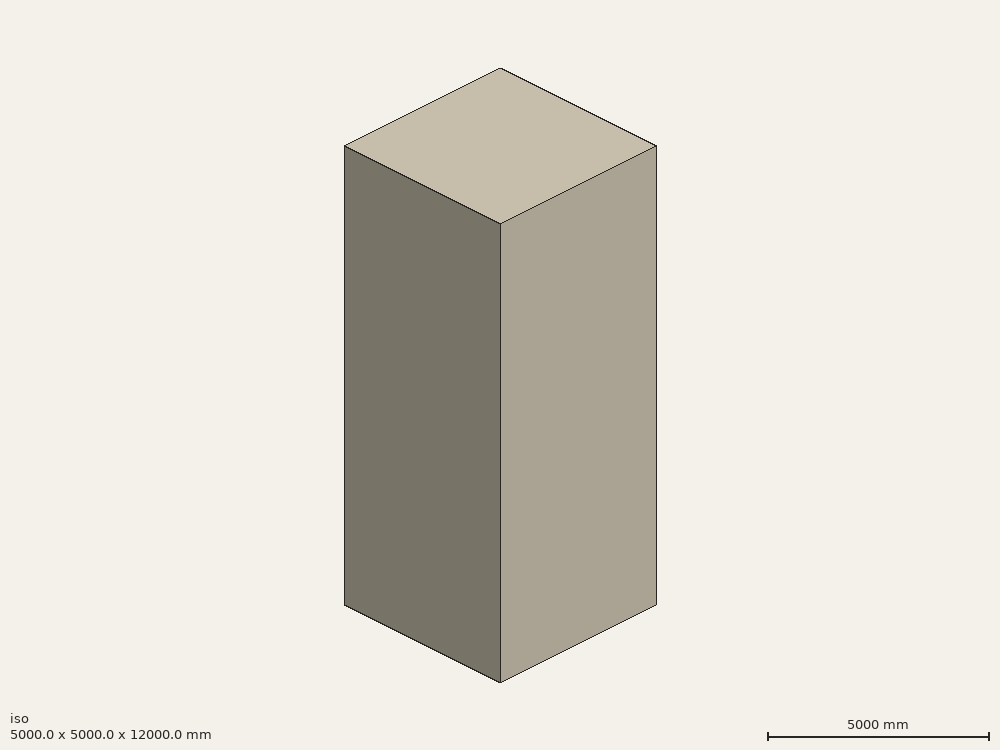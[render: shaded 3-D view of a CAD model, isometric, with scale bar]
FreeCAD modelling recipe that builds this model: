
FCSTD DOCUMENT  (FreeCAD 0.21R33694 (Git))
Label: revolveTester-7
License: All rights reserved
LicenseURL: http://en.wikipedia.org/wiki/All_rights_reserved
objects: App::DocumentObjectGroupPython×1248, Part::FeaturePython×2, App::Part×2, Sketcher::SketchObject×1, Part::Revolution×1, Part::Cylinder×1, Part::Mirroring×1, Part::Cut×1
note: 7 computed .brp shape members not serialized (recipe doc carries the construction recipe); baked Part::Feature solids carry a one-line shape summary decoded from their .brp

FEATURE [App::DocumentObjectGroupPython] HALFPI  # scripted group (container) (typed FeaturePython)
  name = HALFPI
  value = pi/2.
FEATURE [App::DocumentObjectGroupPython] PI  # scripted group (container) (typed FeaturePython)
  name = PI
  value = 1.*pi
FEATURE [App::DocumentObjectGroupPython] TWOPI  # scripted group (container) (typed FeaturePython)
  name = TWOPI
  value = 2.*pi
FEATURE [App::DocumentObjectGroupPython] Constants  # scripted group (container) (typed FeaturePython)
  Group = -> [HALFPI,PI,TWOPI]
FEATURE [App::DocumentObjectGroupPython] Variables  # scripted group (container) (typed FeaturePython)
FEATURE [App::DocumentObjectGroupPython] Quantities  # scripted group (container) (typed FeaturePython)
FEATURE [App::DocumentObjectGroupPython] Isotopes  # scripted group (container) (typed FeaturePython)
FEATURE [App::DocumentObjectGroupPython] Elements  # scripted group (container) (typed FeaturePython)
FEATURE [App::DocumentObjectGroupPython] G4Isotopes  # scripted group (container) (typed FeaturePython)
FEATURE [App::DocumentObjectGroupPython] H_element  # scripted group (container) (typed FeaturePython)
  Z = 1
  atom_value = 1.008
  formula = H
  name = H_element
FEATURE [App::DocumentObjectGroupPython] He_element  # scripted group (container) (typed FeaturePython)
  Z = 2
  atom_value = 4.0026
  formula = He
  name = He_element
FEATURE [App::DocumentObjectGroupPython] Li_element  # scripted group (container) (typed FeaturePython)
  Z = 3
  atom_value = 6.94
  formula = Li
  name = Li_element
FEATURE [App::DocumentObjectGroupPython] Be_element  # scripted group (container) (typed FeaturePython)
  Z = 4
  atom_value = 9.01218
  formula = Be
  name = Be_element
FEATURE [App::DocumentObjectGroupPython] B_element  # scripted group (container) (typed FeaturePython)
  Z = 5
  atom_value = 10.81
  formula = B
  name = B_element
FEATURE [App::DocumentObjectGroupPython] C_element  # scripted group (container) (typed FeaturePython)
  Z = 6
  atom_value = 12.011
  formula = C
  name = C_element
FEATURE [App::DocumentObjectGroupPython] N_element  # scripted group (container) (typed FeaturePython)
  Z = 7
  atom_value = 14.007
  formula = N
  name = N_element
FEATURE [App::DocumentObjectGroupPython] O_element  # scripted group (container) (typed FeaturePython)
  Z = 8
  atom_value = 15.999
  formula = O
  name = O_element
FEATURE [App::DocumentObjectGroupPython] F_element  # scripted group (container) (typed FeaturePython)
  Z = 9
  atom_value = 18.9984
  formula = F
  name = F_element
FEATURE [App::DocumentObjectGroupPython] Ne_element  # scripted group (container) (typed FeaturePython)
  Z = 10
  atom_value = 20.1797
  formula = Ne
  name = Ne_element
FEATURE [App::DocumentObjectGroupPython] Na_element  # scripted group (container) (typed FeaturePython)
  Z = 11
  atom_value = 22.9898
  formula = Na
  name = Na_element
FEATURE [App::DocumentObjectGroupPython] Mg_element  # scripted group (container) (typed FeaturePython)
  Z = 12
  atom_value = 24.305
  formula = Mg
  name = Mg_element
FEATURE [App::DocumentObjectGroupPython] Al_element  # scripted group (container) (typed FeaturePython)
  Z = 13
  atom_value = 26.9815
  formula = Al
  name = Al_element
FEATURE [App::DocumentObjectGroupPython] Si_element  # scripted group (container) (typed FeaturePython)
  Z = 14
  atom_value = 28.085
  formula = Si
  name = Si_element
FEATURE [App::DocumentObjectGroupPython] P_element  # scripted group (container) (typed FeaturePython)
  Z = 15
  atom_value = 30.9738
  formula = P
  name = P_element
FEATURE [App::DocumentObjectGroupPython] S_element  # scripted group (container) (typed FeaturePython)
  Z = 16
  atom_value = 32.06
  formula = S
  name = S_element
FEATURE [App::DocumentObjectGroupPython] Cl_element  # scripted group (container) (typed FeaturePython)
  Z = 17
  atom_value = 35.45
  formula = Cl
  name = Cl_element
FEATURE [App::DocumentObjectGroupPython] Ar_element  # scripted group (container) (typed FeaturePython)
  Z = 18
  atom_value = 39.95
  formula = Ar
  name = Ar_element
FEATURE [App::DocumentObjectGroupPython] K_element  # scripted group (container) (typed FeaturePython)
  Z = 19
  atom_value = 39.0983
  formula = K
  name = K_element
FEATURE [App::DocumentObjectGroupPython] Ca_element  # scripted group (container) (typed FeaturePython)
  Z = 20
  atom_value = 40.078
  formula = Ca
  name = Ca_element
FEATURE [App::DocumentObjectGroupPython] Sc_element  # scripted group (container) (typed FeaturePython)
  Z = 21
  atom_value = 44.9559
  formula = Sc
  name = Sc_element
FEATURE [App::DocumentObjectGroupPython] Ti_element  # scripted group (container) (typed FeaturePython)
  Z = 22
  atom_value = 47.867
  formula = Ti
  name = Ti_element
FEATURE [App::DocumentObjectGroupPython] V_element  # scripted group (container) (typed FeaturePython)
  Z = 23
  atom_value = 50.9415
  formula = V
  name = V_element
FEATURE [App::DocumentObjectGroupPython] Cr_element  # scripted group (container) (typed FeaturePython)
  Z = 24
  atom_value = 51.9961
  formula = Cr
  name = Cr_element
FEATURE [App::DocumentObjectGroupPython] Mn_element  # scripted group (container) (typed FeaturePython)
  Z = 25
  atom_value = 54.938
  formula = Mn
  name = Mn_element
FEATURE [App::DocumentObjectGroupPython] Fe_element  # scripted group (container) (typed FeaturePython)
  Z = 26
  atom_value = 55.845
  formula = Fe
  name = Fe_element
FEATURE [App::DocumentObjectGroupPython] Co_element  # scripted group (container) (typed FeaturePython)
  Z = 27
  atom_value = 58.9332
  formula = Co
  name = Co_element
FEATURE [App::DocumentObjectGroupPython] Ni_element  # scripted group (container) (typed FeaturePython)
  Z = 28
  atom_value = 58.6934
  formula = Ni
  name = Ni_element
FEATURE [App::DocumentObjectGroupPython] Cu_element  # scripted group (container) (typed FeaturePython)
  Z = 29
  atom_value = 63.546
  formula = Cu
  name = Cu_element
FEATURE [App::DocumentObjectGroupPython] Zn_element  # scripted group (container) (typed FeaturePython)
  Z = 30
  atom_value = 65.38
  formula = Zn
  name = Zn_element
FEATURE [App::DocumentObjectGroupPython] Ga_element  # scripted group (container) (typed FeaturePython)
  Z = 31
  atom_value = 69.723
  formula = Ga
  name = Ga_element
FEATURE [App::DocumentObjectGroupPython] Ge_element  # scripted group (container) (typed FeaturePython)
  Z = 32
  atom_value = 72.63
  formula = Ge
  name = Ge_element
FEATURE [App::DocumentObjectGroupPython] As_element  # scripted group (container) (typed FeaturePython)
  Z = 33
  atom_value = 74.9216
  formula = As
  name = As_element
FEATURE [App::DocumentObjectGroupPython] Se_element  # scripted group (container) (typed FeaturePython)
  Z = 34
  atom_value = 78.971
  formula = Se
  name = Se_element
FEATURE [App::DocumentObjectGroupPython] Br_element  # scripted group (container) (typed FeaturePython)
  Z = 35
  atom_value = 79.904
  formula = Br
  name = Br_element
FEATURE [App::DocumentObjectGroupPython] Kr_element  # scripted group (container) (typed FeaturePython)
  Z = 36
  atom_value = 83.798
  formula = Kr
  name = Kr_element
FEATURE [App::DocumentObjectGroupPython] Rb_element  # scripted group (container) (typed FeaturePython)
  Z = 37
  atom_value = 85.4678
  formula = Rb
  name = Rb_element
FEATURE [App::DocumentObjectGroupPython] Sr_element  # scripted group (container) (typed FeaturePython)
  Z = 38
  atom_value = 87.62
  formula = Sr
  name = Sr_element
FEATURE [App::DocumentObjectGroupPython] Y_element  # scripted group (container) (typed FeaturePython)
  Z = 39
  atom_value = 88.9058
  formula = Y
  name = Y_element
FEATURE [App::DocumentObjectGroupPython] Zr_element  # scripted group (container) (typed FeaturePython)
  Z = 40
  atom_value = 91.224
  formula = Zr
  name = Zr_element
FEATURE [App::DocumentObjectGroupPython] Nb_element  # scripted group (container) (typed FeaturePython)
  Z = 41
  atom_value = 92.9064
  formula = Nb
  name = Nb_element
FEATURE [App::DocumentObjectGroupPython] Mo_element  # scripted group (container) (typed FeaturePython)
  Z = 42
  atom_value = 95.95
  formula = Mo
  name = Mo_element
FEATURE [App::DocumentObjectGroupPython] Tc_element  # scripted group (container) (typed FeaturePython)
  Z = 43
  atom_value = 97
  formula = Tc
  name = Tc_element
FEATURE [App::DocumentObjectGroupPython] Ru_element  # scripted group (container) (typed FeaturePython)
  Z = 44
  atom_value = 101.07
  formula = Ru
  name = Ru_element
FEATURE [App::DocumentObjectGroupPython] Rh_element  # scripted group (container) (typed FeaturePython)
  Z = 45
  atom_value = 102.905
  formula = Rh
  name = Rh_element
FEATURE [App::DocumentObjectGroupPython] Pd_element  # scripted group (container) (typed FeaturePython)
  Z = 46
  atom_value = 106.42
  formula = Pd
  name = Pd_element
FEATURE [App::DocumentObjectGroupPython] Ag_element  # scripted group (container) (typed FeaturePython)
  Z = 47
  atom_value = 107.868
  formula = Ag
  name = Ag_element
FEATURE [App::DocumentObjectGroupPython] Cd_element  # scripted group (container) (typed FeaturePython)
  Z = 48
  atom_value = 112.414
  formula = Cd
  name = Cd_element
FEATURE [App::DocumentObjectGroupPython] In_element  # scripted group (container) (typed FeaturePython)
  Z = 49
  atom_value = 114.818
  formula = In
  name = In_element
FEATURE [App::DocumentObjectGroupPython] Sn_element  # scripted group (container) (typed FeaturePython)
  Z = 50
  atom_value = 118.71
  formula = Sn
  name = Sn_element
FEATURE [App::DocumentObjectGroupPython] Sb_element  # scripted group (container) (typed FeaturePython)
  Z = 51
  atom_value = 121.76
  formula = Sb
  name = Sb_element
FEATURE [App::DocumentObjectGroupPython] Te_element  # scripted group (container) (typed FeaturePython)
  Z = 52
  atom_value = 127.6
  formula = Te
  name = Te_element
FEATURE [App::DocumentObjectGroupPython] I_element  # scripted group (container) (typed FeaturePython)
  Z = 53
  atom_value = 126.904
  formula = I
  name = I_element
FEATURE [App::DocumentObjectGroupPython] Xe_element  # scripted group (container) (typed FeaturePython)
  Z = 54
  atom_value = 131.293
  formula = Xe
  name = Xe_element
FEATURE [App::DocumentObjectGroupPython] Cs_element  # scripted group (container) (typed FeaturePython)
  Z = 55
  atom_value = 132.905
  formula = Cs
  name = Cs_element
FEATURE [App::DocumentObjectGroupPython] Ba_element  # scripted group (container) (typed FeaturePython)
  Z = 56
  atom_value = 137.327
  formula = Ba
  name = Ba_element
FEATURE [App::DocumentObjectGroupPython] La_element  # scripted group (container) (typed FeaturePython)
  Z = 57
  atom_value = 138.905
  formula = La
  name = La_element
FEATURE [App::DocumentObjectGroupPython] Ce_element  # scripted group (container) (typed FeaturePython)
  Z = 58
  atom_value = 140.116
  formula = Ce
  name = Ce_element
FEATURE [App::DocumentObjectGroupPython] Pr_element  # scripted group (container) (typed FeaturePython)
  Z = 59
  atom_value = 140.908
  formula = Pr
  name = Pr_element
FEATURE [App::DocumentObjectGroupPython] Nd_element  # scripted group (container) (typed FeaturePython)
  Z = 60
  atom_value = 144.242
  formula = Nd
  name = Nd_element
FEATURE [App::DocumentObjectGroupPython] Pm_element  # scripted group (container) (typed FeaturePython)
  Z = 61
  atom_value = 145
  formula = Pm
  name = Pm_element
FEATURE [App::DocumentObjectGroupPython] Sm_element  # scripted group (container) (typed FeaturePython)
  Z = 62
  atom_value = 150.36
  formula = Sm
  name = Sm_element
FEATURE [App::DocumentObjectGroupPython] Eu_element  # scripted group (container) (typed FeaturePython)
  Z = 63
  atom_value = 151.964
  formula = Eu
  name = Eu_element
FEATURE [App::DocumentObjectGroupPython] Gd_element  # scripted group (container) (typed FeaturePython)
  Z = 64
  atom_value = 157.25
  formula = Gd
  name = Gd_element
FEATURE [App::DocumentObjectGroupPython] Tb_element  # scripted group (container) (typed FeaturePython)
  Z = 65
  atom_value = 158.925
  formula = Tb
  name = Tb_element
FEATURE [App::DocumentObjectGroupPython] Dy_element  # scripted group (container) (typed FeaturePython)
  Z = 66
  atom_value = 162.5
  formula = Dy
  name = Dy_element
FEATURE [App::DocumentObjectGroupPython] Ho_element  # scripted group (container) (typed FeaturePython)
  Z = 67
  atom_value = 164.93
  formula = Ho
  name = Ho_element
FEATURE [App::DocumentObjectGroupPython] Er_element  # scripted group (container) (typed FeaturePython)
  Z = 68
  atom_value = 167.259
  formula = Er
  name = Er_element
FEATURE [App::DocumentObjectGroupPython] Tm_element  # scripted group (container) (typed FeaturePython)
  Z = 69
  atom_value = 168.934
  formula = Tm
  name = Tm_element
FEATURE [App::DocumentObjectGroupPython] Yb_element  # scripted group (container) (typed FeaturePython)
  Z = 70
  atom_value = 173.045
  formula = Yb
  name = Yb_element
FEATURE [App::DocumentObjectGroupPython] Lu_element  # scripted group (container) (typed FeaturePython)
  Z = 71
  atom_value = 174.967
  formula = Lu
  name = Lu_element
FEATURE [App::DocumentObjectGroupPython] Hf_element  # scripted group (container) (typed FeaturePython)
  Z = 72
  atom_value = 178.49
  formula = Hf
  name = Hf_element
FEATURE [App::DocumentObjectGroupPython] Ta_element  # scripted group (container) (typed FeaturePython)
  Z = 73
  atom_value = 180.948
  formula = Ta
  name = Ta_element
FEATURE [App::DocumentObjectGroupPython] W_element  # scripted group (container) (typed FeaturePython)
  Z = 74
  atom_value = 183.84
  formula = W
  name = W_element
FEATURE [App::DocumentObjectGroupPython] Re_element  # scripted group (container) (typed FeaturePython)
  Z = 75
  atom_value = 186.207
  formula = Re
  name = Re_element
FEATURE [App::DocumentObjectGroupPython] Os_element  # scripted group (container) (typed FeaturePython)
  Z = 76
  atom_value = 190.23
  formula = Os
  name = Os_element
FEATURE [App::DocumentObjectGroupPython] Ir_element  # scripted group (container) (typed FeaturePython)
  Z = 77
  atom_value = 192.217
  formula = Ir
  name = Ir_element
FEATURE [App::DocumentObjectGroupPython] Pt_element  # scripted group (container) (typed FeaturePython)
  Z = 78
  atom_value = 195.084
  formula = Pt
  name = Pt_element
FEATURE [App::DocumentObjectGroupPython] Au_element  # scripted group (container) (typed FeaturePython)
  Z = 79
  atom_value = 196.967
  formula = Au
  name = Au_element
FEATURE [App::DocumentObjectGroupPython] Hg_element  # scripted group (container) (typed FeaturePython)
  Z = 80
  atom_value = 200.592
  formula = Hg
  name = Hg_element
FEATURE [App::DocumentObjectGroupPython] Tl_element  # scripted group (container) (typed FeaturePython)
  Z = 81
  atom_value = 204.38
  formula = Tl
  name = Tl_element
FEATURE [App::DocumentObjectGroupPython] Pb_element  # scripted group (container) (typed FeaturePython)
  Z = 82
  atom_value = 207.2
  formula = Pb
  name = Pb_element
FEATURE [App::DocumentObjectGroupPython] Bi_element  # scripted group (container) (typed FeaturePython)
  Z = 83
  atom_value = 208.98
  formula = Bi
  name = Bi_element
FEATURE [App::DocumentObjectGroupPython] Po_element  # scripted group (container) (typed FeaturePython)
  Z = 84
  atom_value = 209
  formula = Po
  name = Po_element
FEATURE [App::DocumentObjectGroupPython] At_element  # scripted group (container) (typed FeaturePython)
  Z = 85
  atom_value = 210
  formula = At
  name = At_element
FEATURE [App::DocumentObjectGroupPython] Rn_element  # scripted group (container) (typed FeaturePython)
  Z = 86
  atom_value = 222
  formula = Rn
  name = Rn_element
FEATURE [App::DocumentObjectGroupPython] Fr_element  # scripted group (container) (typed FeaturePython)
  Z = 87
  atom_value = 223
  formula = Fr
  name = Fr_element
FEATURE [App::DocumentObjectGroupPython] Ra_element  # scripted group (container) (typed FeaturePython)
  Z = 88
  atom_value = 226
  formula = Ra
  name = Ra_element
FEATURE [App::DocumentObjectGroupPython] Ac_element  # scripted group (container) (typed FeaturePython)
  Z = 89
  atom_value = 227
  formula = Ac
  name = Ac_element
FEATURE [App::DocumentObjectGroupPython] Th_element  # scripted group (container) (typed FeaturePython)
  Z = 90
  atom_value = 232.038
  formula = Th
  name = Th_element
FEATURE [App::DocumentObjectGroupPython] Pa_element  # scripted group (container) (typed FeaturePython)
  Z = 91
  atom_value = 231.036
  formula = Pa
  name = Pa_element
FEATURE [App::DocumentObjectGroupPython] U_element  # scripted group (container) (typed FeaturePython)
  Z = 92
  atom_value = 238.029
  formula = U
  name = U_element
FEATURE [App::DocumentObjectGroupPython] Np_element  # scripted group (container) (typed FeaturePython)
  Z = 93
  atom_value = 237
  formula = Np
  name = Np_element
FEATURE [App::DocumentObjectGroupPython] Pu_element  # scripted group (container) (typed FeaturePython)
  Z = 94
  atom_value = 244
  formula = Pu
  name = Pu_element
FEATURE [App::DocumentObjectGroupPython] Am_element  # scripted group (container) (typed FeaturePython)
  Z = 95
  atom_value = 243
  formula = Am
  name = Am_element
FEATURE [App::DocumentObjectGroupPython] Cm_element  # scripted group (container) (typed FeaturePython)
  Z = 96
  atom_value = 247
  formula = Cm
  name = Cm_element
FEATURE [App::DocumentObjectGroupPython] Bk_element  # scripted group (container) (typed FeaturePython)
  Z = 97
  atom_value = 247
  formula = Bk
  name = Bk_element
FEATURE [App::DocumentObjectGroupPython] Cf_element  # scripted group (container) (typed FeaturePython)
  Z = 98
  atom_value = 251
  formula = Cf
  name = Cf_element
FEATURE [App::DocumentObjectGroupPython] G4Elements  # scripted group (container) (typed FeaturePython)
  Group = -> [H_element,He_element,Li_element,Be_element,B_element,C_element,N_element,O_element,F_element,Ne_element,Na_element,Mg_element,Al_element,Si_element,P_element,S_element,Cl_element,Ar_element,K_element,Ca_element,Sc_element,Ti_element,V_element,Cr_element,Mn_element,Fe_element,Co_element,Ni_element,Cu_element,Zn_element,Ga_element,Ge_element,As_element,Se_element,Br_element,Kr_element,Rb_element,+61 more]
FEATURE [App::DocumentObjectGroupPython] H_element001  label="H_element : 0.101"  # scripted group (container) (typed FeaturePython)
  n = 0.101327
FEATURE [App::DocumentObjectGroupPython] C_element001  label="C_element : 0.775"  # scripted group (container) (typed FeaturePython)
  n = 0.7755
FEATURE [App::DocumentObjectGroupPython] N_element001  label="N_element : 0.035"  # scripted group (container) (typed FeaturePython)
  n = 0.035057
FEATURE [App::DocumentObjectGroupPython] O_element001  label="O_element : 0.052"  # scripted group (container) (typed FeaturePython)
  n = 0.0523159
FEATURE [App::DocumentObjectGroupPython] F_element001  label="F_element : 0.017"  # scripted group (container) (typed FeaturePython)
  n = 0.017422
FEATURE [App::DocumentObjectGroupPython] Ca_element001  label="Ca_element : 0.018"  # scripted group (container) (typed FeaturePython)
  n = 0.018378
FEATURE [App::DocumentObjectGroupPython] G4_A_150_TISSUE  label="G4_A-150_TISSUE"  # scripted group (container) (typed FeaturePython)
  Dunit = g/cm3
  Dvalue = 1.127
  Group = -> [H_element001,C_element001,N_element001,O_element001,F_element001,Ca_element001]
  conduct = 2
  density = 1
  expand = 3
  formula = G4_A-150_TISSUE
  name = G4_A-150_TISSUE
  specific = 4
FEATURE [App::DocumentObjectGroupPython] C_element002  label="C_element : 3"  # scripted group (container) (typed FeaturePython)
  n = 3
  ref = C_element
FEATURE [App::DocumentObjectGroupPython] H_element002  label="H_element : 6"  # scripted group (container) (typed FeaturePython)
  n = 6
  ref = H_element
FEATURE [App::DocumentObjectGroupPython] O_element002  label="O_element : 1"  # scripted group (container) (typed FeaturePython)
  n = 1
  ref = O_element
FEATURE [App::DocumentObjectGroupPython] G4_ACETONE  # scripted group (container) (typed FeaturePython)
  Dunit = g/cm3
  Dvalue = 0.7899
  Group = -> [C_element002,H_element002,O_element002]
  conduct = 2
  density = 1
  expand = 3
  formula = G4_ACETONE
  name = G4_ACETONE
  specific = 4
FEATURE [App::DocumentObjectGroupPython] C_element003  label="C_element : 2"  # scripted group (container) (typed FeaturePython)
  n = 2
  ref = C_element
FEATURE [App::DocumentObjectGroupPython] H_element003  label="H_element : 2"  # scripted group (container) (typed FeaturePython)
  n = 2
  ref = H_element
FEATURE [App::DocumentObjectGroupPython] G4_ACETYLENE  # scripted group (container) (typed FeaturePython)
  Dunit = g/cm3
  Dvalue = 0.0010967
  Group = -> [C_element003,H_element003]
  conduct = 2
  density = 1
  expand = 3
  formula = G4_ACETYLENE
  name = G4_ACETYLENE
  specific = 4
FEATURE [App::DocumentObjectGroupPython] C_element004  label="C_element : 5"  # scripted group (container) (typed FeaturePython)
  n = 5
  ref = C_element
FEATURE [App::DocumentObjectGroupPython] H_element004  label="H_element : 5"  # scripted group (container) (typed FeaturePython)
  n = 5
  ref = H_element
FEATURE [App::DocumentObjectGroupPython] N_element002  label="N_element : 5"  # scripted group (container) (typed FeaturePython)
  n = 5
  ref = N_element
FEATURE [App::DocumentObjectGroupPython] G4_ADENINE  # scripted group (container) (typed FeaturePython)
  Dunit = g/cm3
  Dvalue = 1.6
  Group = -> [C_element004,H_element004,N_element002]
  conduct = 2
  density = 1
  expand = 3
  formula = G4_ADENINE
  name = G4_ADENINE
  specific = 4
FEATURE [App::DocumentObjectGroupPython] H_element005  label="H_element : 0.114"  # scripted group (container) (typed FeaturePython)
  n = 0.114
FEATURE [App::DocumentObjectGroupPython] C_element005  label="C_element : 0.598"  # scripted group (container) (typed FeaturePython)
  n = 0.598
FEATURE [App::DocumentObjectGroupPython] N_element003  label="N_element : 0.007"  # scripted group (container) (typed FeaturePython)
  n = 0.007
FEATURE [App::DocumentObjectGroupPython] O_element003  label="O_element : 0.278"  # scripted group (container) (typed FeaturePython)
  n = 0.278
FEATURE [App::DocumentObjectGroupPython] Na_element001  label="Na_element : 0.001"  # scripted group (container) (typed FeaturePython)
  n = 0.001
FEATURE [App::DocumentObjectGroupPython] S_element001  label="S_element : 0.001"  # scripted group (container) (typed FeaturePython)
  n = 0.001
FEATURE [App::DocumentObjectGroupPython] Cl_element001  label="Cl_element : 0.001"  # scripted group (container) (typed FeaturePython)
  n = 0.001
FEATURE [App::DocumentObjectGroupPython] G4_ADIPOSE_TISSUE_ICRP  # scripted group (container) (typed FeaturePython)
  Dunit = g/cm3
  Dvalue = 0.95
  Group = -> [H_element005,C_element005,N_element003,O_element003,Na_element001,S_element001,Cl_element001]
  conduct = 2
  density = 1
  expand = 3
  formula = G4_ADIPOSE_TISSUE_ICRP
  name = G4_ADIPOSE_TISSUE_ICRP
  specific = 4
FEATURE [App::DocumentObjectGroupPython] C_element006  label="C_element : 0.000"  # scripted group (container) (typed FeaturePython)
  n = 0.000124
FEATURE [App::DocumentObjectGroupPython] N_element004  label="N_element : 0.755"  # scripted group (container) (typed FeaturePython)
  n = 0.755268
FEATURE [App::DocumentObjectGroupPython] O_element004  label="O_element : 0.232"  # scripted group (container) (typed FeaturePython)
  n = 0.231781
FEATURE [App::DocumentObjectGroupPython] Ar_element001  label="Ar_element : 0.013"  # scripted group (container) (typed FeaturePython)
  n = 0.012827
FEATURE [App::DocumentObjectGroupPython] G4_AIR  # scripted group (container) (typed FeaturePython)
  Dunit = g/cm3
  Dvalue = 0.00120479
  Group = -> [C_element006,N_element004,O_element004,Ar_element001]
  conduct = 2
  density = 1
  expand = 3
  formula = G4_AIR
  name = G4_AIR
  specific = 4
FEATURE [App::DocumentObjectGroupPython] C_element007  label="C_element : 006"  # scripted group (container) (typed FeaturePython)
  n = 3
  ref = C_element
FEATURE [App::DocumentObjectGroupPython] H_element006  label="H_element : 7"  # scripted group (container) (typed FeaturePython)
  n = 7
  ref = H_element
FEATURE [App::DocumentObjectGroupPython] N_element005  label="N_element : 1"  # scripted group (container) (typed FeaturePython)
  n = 1
  ref = N_element
FEATURE [App::DocumentObjectGroupPython] O_element005  label="O_element : 2"  # scripted group (container) (typed FeaturePython)
  n = 2
  ref = O_element
FEATURE [App::DocumentObjectGroupPython] G4_ALANINE  # scripted group (container) (typed FeaturePython)
  Dunit = g/cm3
  Dvalue = 1.42
  Group = -> [C_element007,H_element006,N_element005,O_element005]
  conduct = 2
  density = 1
  expand = 3
  formula = G4_ALANINE
  name = G4_ALANINE
  specific = 4
FEATURE [App::DocumentObjectGroupPython] Al_element001  label="Al_element : 2"  # scripted group (container) (typed FeaturePython)
  n = 2
  ref = Al_element
FEATURE [App::DocumentObjectGroupPython] O_element006  label="O_element : 3"  # scripted group (container) (typed FeaturePython)
  n = 3
  ref = O_element
FEATURE [App::DocumentObjectGroupPython] G4_ALUMINUM_OXIDE  # scripted group (container) (typed FeaturePython)
  Dunit = g/cm3
  Dvalue = 3.97
  Group = -> [Al_element001,O_element006]
  conduct = 2
  density = 1
  expand = 3
  formula = G4_ALUMINUM_OXIDE
  name = G4_ALUMINUM_OXIDE
  specific = 4
FEATURE [App::DocumentObjectGroupPython] H_element007  label="H_element : 0.106"  # scripted group (container) (typed FeaturePython)
  n = 0.10593
FEATURE [App::DocumentObjectGroupPython] C_element008  label="C_element : 0.789"  # scripted group (container) (typed FeaturePython)
  n = 0.788974
FEATURE [App::DocumentObjectGroupPython] O_element007  label="O_element : 0.105"  # scripted group (container) (typed FeaturePython)
  n = 0.105096
FEATURE [App::DocumentObjectGroupPython] G4_AMBER  # scripted group (container) (typed FeaturePython)
  Dunit = g/cm3
  Dvalue = 1.1
  Group = -> [H_element007,C_element008,O_element007]
  conduct = 2
  density = 1
  expand = 3
  formula = G4_AMBER
  name = G4_AMBER
  specific = 4
FEATURE [App::DocumentObjectGroupPython] N_element006  label="N_element : 006"  # scripted group (container) (typed FeaturePython)
  n = 1
  ref = N_element
FEATURE [App::DocumentObjectGroupPython] H_element008  label="H_element : 3"  # scripted group (container) (typed FeaturePython)
  n = 3
  ref = H_element
FEATURE [App::DocumentObjectGroupPython] G4_AMMONIA  # scripted group (container) (typed FeaturePython)
  Dunit = g/cm3
  Dvalue = 0.000826019
  Group = -> [N_element006,H_element008]
  conduct = 2
  density = 1
  expand = 3
  formula = G4_AMMONIA
  name = G4_AMMONIA
  specific = 4
FEATURE [App::DocumentObjectGroupPython] C_element009  label="C_element : 6"  # scripted group (container) (typed FeaturePython)
  n = 6
  ref = C_element
FEATURE [App::DocumentObjectGroupPython] H_element009  label="H_element : 008"  # scripted group (container) (typed FeaturePython)
  n = 7
  ref = H_element
FEATURE [App::DocumentObjectGroupPython] N_element007  label="N_element : 007"  # scripted group (container) (typed FeaturePython)
  n = 1
  ref = N_element
FEATURE [App::DocumentObjectGroupPython] G4_ANILINE  # scripted group (container) (typed FeaturePython)
  Dunit = g/cm3
  Dvalue = 1.0235
  Group = -> [C_element009,H_element009,N_element007]
  conduct = 2
  density = 1
  expand = 3
  formula = G4_ANILINE
  name = G4_ANILINE
  specific = 4
FEATURE [App::DocumentObjectGroupPython] C_element010  label="C_element : 14"  # scripted group (container) (typed FeaturePython)
  n = 14
  ref = C_element
FEATURE [App::DocumentObjectGroupPython] H_element010  label="H_element : 10"  # scripted group (container) (typed FeaturePython)
  n = 10
  ref = H_element
FEATURE [App::DocumentObjectGroupPython] G4_ANTHRACENE  # scripted group (container) (typed FeaturePython)
  Dunit = g/cm3
  Dvalue = 1.283
  Group = -> [C_element010,H_element010]
  conduct = 2
  density = 1
  expand = 3
  formula = G4_ANTHRACENE
  name = G4_ANTHRACENE
  specific = 4
FEATURE [App::DocumentObjectGroupPython] H_element011  label="H_element : 0.065"  # scripted group (container) (typed FeaturePython)
  n = 0.0654709
FEATURE [App::DocumentObjectGroupPython] C_element011  label="C_element : 0.537"  # scripted group (container) (typed FeaturePython)
  n = 0.536944
FEATURE [App::DocumentObjectGroupPython] N_element008  label="N_element : 0.021"  # scripted group (container) (typed FeaturePython)
  n = 0.0215
FEATURE [App::DocumentObjectGroupPython] O_element008  label="O_element : 0.032"  # scripted group (container) (typed FeaturePython)
  n = 0.032085
FEATURE [App::DocumentObjectGroupPython] F_element002  label="F_element : 0.167"  # scripted group (container) (typed FeaturePython)
  n = 0.167411
FEATURE [App::DocumentObjectGroupPython] Ca_element002  label="Ca_element : 0.177"  # scripted group (container) (typed FeaturePython)
  n = 0.176589
FEATURE [App::DocumentObjectGroupPython] G4_B_100_BONE  label="G4_B-100_BONE"  # scripted group (container) (typed FeaturePython)
  Dunit = g/cm3
  Dvalue = 1.45
  Group = -> [H_element011,C_element011,N_element008,O_element008,F_element002,Ca_element002]
  conduct = 2
  density = 1
  expand = 3
  formula = G4_B-100_BONE
  name = G4_B-100_BONE
  specific = 4
FEATURE [App::DocumentObjectGroupPython] H_element012  label="H_element : 0.057"  # scripted group (container) (typed FeaturePython)
  n = 0.057441
FEATURE [App::DocumentObjectGroupPython] C_element012  label="C_element : 0.790"  # scripted group (container) (typed FeaturePython)
  n = 0.774591
FEATURE [App::DocumentObjectGroupPython] O_element009  label="O_element : 0.168"  # scripted group (container) (typed FeaturePython)
  n = 0.167968
FEATURE [App::DocumentObjectGroupPython] G4_BAKELITE  # scripted group (container) (typed FeaturePython)
  Dunit = g/cm3
  Dvalue = 1.25
  Group = -> [H_element012,C_element012,O_element009]
  conduct = 2
  density = 1
  expand = 3
  formula = G4_BAKELITE
  name = G4_BAKELITE
  specific = 4
FEATURE [App::DocumentObjectGroupPython] Ba_element001  label="Ba_element : 1"  # scripted group (container) (typed FeaturePython)
  n = 1
  ref = Ba_element
FEATURE [App::DocumentObjectGroupPython] F_element003  label="F_element : 2"  # scripted group (container) (typed FeaturePython)
  n = 2
  ref = F_element
FEATURE [App::DocumentObjectGroupPython] G4_BARIUM_FLUORIDE  # scripted group (container) (typed FeaturePython)
  Dunit = g/cm3
  Dvalue = 4.89
  Group = -> [Ba_element001,F_element003]
  conduct = 2
  density = 1
  expand = 3
  formula = G4_BARIUM_FLUORIDE
  name = G4_BARIUM_FLUORIDE
  specific = 4
FEATURE [App::DocumentObjectGroupPython] Ba_element002  label="Ba_element : 002"  # scripted group (container) (typed FeaturePython)
  n = 1
  ref = Ba_element
FEATURE [App::DocumentObjectGroupPython] S_element002  label="S_element : 1"  # scripted group (container) (typed FeaturePython)
  n = 1
  ref = S_element
FEATURE [App::DocumentObjectGroupPython] O_element010  label="O_element : 4"  # scripted group (container) (typed FeaturePython)
  n = 4
  ref = O_element
FEATURE [App::DocumentObjectGroupPython] G4_BARIUM_SULFATE  # scripted group (container) (typed FeaturePython)
  Dunit = g/cm3
  Dvalue = 4.5
  Group = -> [Ba_element002,S_element002,O_element010]
  conduct = 2
  density = 1
  expand = 3
  formula = G4_BARIUM_SULFATE
  name = G4_BARIUM_SULFATE
  specific = 4
FEATURE [App::DocumentObjectGroupPython] C_element013  label="C_element : 007"  # scripted group (container) (typed FeaturePython)
  n = 6
  ref = C_element
FEATURE [App::DocumentObjectGroupPython] H_element013  label="H_element : 009"  # scripted group (container) (typed FeaturePython)
  n = 6
  ref = H_element
FEATURE [App::DocumentObjectGroupPython] G4_BENZENE  # scripted group (container) (typed FeaturePython)
  Dunit = g/cm3
  Dvalue = 0.87865
  Group = -> [C_element013,H_element013]
  conduct = 2
  density = 1
  expand = 3
  formula = G4_BENZENE
  name = G4_BENZENE
  specific = 4
FEATURE [App::DocumentObjectGroupPython] Be_element001  label="Be_element : 1"  # scripted group (container) (typed FeaturePython)
  n = 1
  ref = Be_element
FEATURE [App::DocumentObjectGroupPython] O_element011  label="O_element : 005"  # scripted group (container) (typed FeaturePython)
  n = 1
  ref = O_element
FEATURE [App::DocumentObjectGroupPython] G4_BERYLLIUM_OXIDE  # scripted group (container) (typed FeaturePython)
  Dunit = g/cm3
  Dvalue = 3.01
  Group = -> [Be_element001,O_element011]
  conduct = 2
  density = 1
  expand = 3
  formula = G4_BERYLLIUM_OXIDE
  name = G4_BERYLLIUM_OXIDE
  specific = 4
FEATURE [App::DocumentObjectGroupPython] Bi_element001  label="Bi_element : 4"  # scripted group (container) (typed FeaturePython)
  n = 4
  ref = Bi_element
FEATURE [App::DocumentObjectGroupPython] Ge_element001  label="Ge_element : 3"  # scripted group (container) (typed FeaturePython)
  n = 3
  ref = Ge_element
FEATURE [App::DocumentObjectGroupPython] O_element012  label="O_element : 12"  # scripted group (container) (typed FeaturePython)
  n = 12
  ref = O_element
FEATURE [App::DocumentObjectGroupPython] G4_BGO  # scripted group (container) (typed FeaturePython)
  Dunit = g/cm3
  Dvalue = 7.13
  Group = -> [Bi_element001,Ge_element001,O_element012]
  conduct = 2
  density = 1
  expand = 3
  formula = G4_BGO
  name = G4_BGO
  specific = 4
FEATURE [App::DocumentObjectGroupPython] H_element014  label="H_element : 0.102"  # scripted group (container) (typed FeaturePython)
  n = 0.102
FEATURE [App::DocumentObjectGroupPython] C_element014  label="C_element : 0.110"  # scripted group (container) (typed FeaturePython)
  n = 0.11
FEATURE [App::DocumentObjectGroupPython] N_element009  label="N_element : 0.033"  # scripted group (container) (typed FeaturePython)
  n = 0.033
FEATURE [App::DocumentObjectGroupPython] O_element013  label="O_element : 0.745"  # scripted group (container) (typed FeaturePython)
  n = 0.745
FEATURE [App::DocumentObjectGroupPython] Na_element002  label="Na_element : 0.002"  # scripted group (container) (typed FeaturePython)
  n = 0.001
FEATURE [App::DocumentObjectGroupPython] P_element001  label="P_element : 0.001"  # scripted group (container) (typed FeaturePython)
  n = 0.001
FEATURE [App::DocumentObjectGroupPython] S_element003  label="S_element : 0.002"  # scripted group (container) (typed FeaturePython)
  n = 0.002
FEATURE [App::DocumentObjectGroupPython] Cl_element002  label="Cl_element : 0.003"  # scripted group (container) (typed FeaturePython)
  n = 0.003
FEATURE [App::DocumentObjectGroupPython] K_element001  label="K_element : 0.002"  # scripted group (container) (typed FeaturePython)
  n = 0.002
FEATURE [App::DocumentObjectGroupPython] Fe_element001  label="Fe_element : 0.001"  # scripted group (container) (typed FeaturePython)
  n = 0.001
FEATURE [App::DocumentObjectGroupPython] G4_BLOOD_ICRP  # scripted group (container) (typed FeaturePython)
  Dunit = g/cm3
  Dvalue = 1.06
  Group = -> [H_element014,C_element014,N_element009,O_element013,Na_element002,P_element001,S_element003,Cl_element002,K_element001,Fe_element001]
  conduct = 2
  density = 1
  expand = 3
  formula = G4_BLOOD_ICRP
  name = G4_BLOOD_ICRP
  specific = 4
FEATURE [App::DocumentObjectGroupPython] H_element015  label="H_element : 0.064"  # scripted group (container) (typed FeaturePython)
  n = 0.064
FEATURE [App::DocumentObjectGroupPython] C_element015  label="C_element : 0.278"  # scripted group (container) (typed FeaturePython)
  n = 0.278
FEATURE [App::DocumentObjectGroupPython] N_element010  label="N_element : 0.027"  # scripted group (container) (typed FeaturePython)
  n = 0.027
FEATURE [App::DocumentObjectGroupPython] O_element014  label="O_element : 0.410"  # scripted group (container) (typed FeaturePython)
  n = 0.41
FEATURE [App::DocumentObjectGroupPython] Mg_element001  label="Mg_element : 0.002"  # scripted group (container) (typed FeaturePython)
  n = 0.002
FEATURE [App::DocumentObjectGroupPython] P_element002  label="P_element : 0.070"  # scripted group (container) (typed FeaturePython)
  n = 0.07
FEATURE [App::DocumentObjectGroupPython] S_element004  label="S_element : 0.003"  # scripted group (container) (typed FeaturePython)
  n = 0.002
FEATURE [App::DocumentObjectGroupPython] Ca_element003  label="Ca_element : 0.147"  # scripted group (container) (typed FeaturePython)
  n = 0.147
FEATURE [App::DocumentObjectGroupPython] G4_BONE_COMPACT_ICRU  # scripted group (container) (typed FeaturePython)
  Dunit = g/cm3
  Dvalue = 1.85
  Group = -> [H_element015,C_element015,N_element010,O_element014,Mg_element001,P_element002,S_element004,Ca_element003]
  conduct = 2
  density = 1
  expand = 3
  formula = G4_BONE_COMPACT_ICRU
  name = G4_BONE_COMPACT_ICRU
  specific = 4
FEATURE [App::DocumentObjectGroupPython] H_element016  label="H_element : 0.034"  # scripted group (container) (typed FeaturePython)
  n = 0.034
FEATURE [App::DocumentObjectGroupPython] C_element016  label="C_element : 0.155"  # scripted group (container) (typed FeaturePython)
  n = 0.155
FEATURE [App::DocumentObjectGroupPython] N_element011  label="N_element : 0.042"  # scripted group (container) (typed FeaturePython)
  n = 0.042
FEATURE [App::DocumentObjectGroupPython] O_element015  label="O_element : 0.435"  # scripted group (container) (typed FeaturePython)
  n = 0.435
FEATURE [App::DocumentObjectGroupPython] Na_element003  label="Na_element : 0.003"  # scripted group (container) (typed FeaturePython)
  n = 0.001
FEATURE [App::DocumentObjectGroupPython] Mg_element002  label="Mg_element : 0.003"  # scripted group (container) (typed FeaturePython)
  n = 0.002
FEATURE [App::DocumentObjectGroupPython] P_element003  label="P_element : 0.103"  # scripted group (container) (typed FeaturePython)
  n = 0.103
FEATURE [App::DocumentObjectGroupPython] S_element005  label="S_element : 0.004"  # scripted group (container) (typed FeaturePython)
  n = 0.003
FEATURE [App::DocumentObjectGroupPython] Ca_element004  label="Ca_element : 0.225"  # scripted group (container) (typed FeaturePython)
  n = 0.225
FEATURE [App::DocumentObjectGroupPython] G4_BONE_CORTICAL_ICRP  # scripted group (container) (typed FeaturePython)
  Dunit = g/cm3
  Dvalue = 1.92
  Group = -> [H_element016,C_element016,N_element011,O_element015,Na_element003,Mg_element002,P_element003,S_element005,Ca_element004]
  conduct = 2
  density = 1
  expand = 3
  formula = G4_BONE_CORTICAL_ICRP
  name = G4_BONE_CORTICAL_ICRP
  specific = 4
FEATURE [App::DocumentObjectGroupPython] B_element001  label="B_element : 4"  # scripted group (container) (typed FeaturePython)
  n = 4
  ref = B_element
FEATURE [App::DocumentObjectGroupPython] C_element017  label="C_element : 1"  # scripted group (container) (typed FeaturePython)
  n = 1
  ref = C_element
FEATURE [App::DocumentObjectGroupPython] G4_BORON_CARBIDE  # scripted group (container) (typed FeaturePython)
  Dunit = g/cm3
  Dvalue = 2.52
  Group = -> [B_element001,C_element017]
  conduct = 2
  density = 1
  expand = 3
  formula = G4_BORON_CARBIDE
  name = G4_BORON_CARBIDE
  specific = 4
FEATURE [App::DocumentObjectGroupPython] B_element002  label="B_element : 2"  # scripted group (container) (typed FeaturePython)
  n = 2
  ref = B_element
FEATURE [App::DocumentObjectGroupPython] O_element016  label="O_element : 006"  # scripted group (container) (typed FeaturePython)
  n = 3
  ref = O_element
FEATURE [App::DocumentObjectGroupPython] G4_BORON_OXIDE  # scripted group (container) (typed FeaturePython)
  Dunit = g/cm3
  Dvalue = 1.812
  Group = -> [B_element002,O_element016]
  conduct = 2
  density = 1
  expand = 3
  formula = G4_BORON_OXIDE
  name = G4_BORON_OXIDE
  specific = 4
FEATURE [App::DocumentObjectGroupPython] H_element017  label="H_element : 0.107"  # scripted group (container) (typed FeaturePython)
  n = 0.107
FEATURE [App::DocumentObjectGroupPython] C_element018  label="C_element : 0.145"  # scripted group (container) (typed FeaturePython)
  n = 0.145
FEATURE [App::DocumentObjectGroupPython] N_element012  label="N_element : 0.022"  # scripted group (container) (typed FeaturePython)
  n = 0.022
FEATURE [App::DocumentObjectGroupPython] O_element017  label="O_element : 0.712"  # scripted group (container) (typed FeaturePython)
  n = 0.712
FEATURE [App::DocumentObjectGroupPython] Na_element004  label="Na_element : 0.004"  # scripted group (container) (typed FeaturePython)
  n = 0.002
FEATURE [App::DocumentObjectGroupPython] P_element004  label="P_element : 0.004"  # scripted group (container) (typed FeaturePython)
  n = 0.004
FEATURE [App::DocumentObjectGroupPython] S_element006  label="S_element : 0.005"  # scripted group (container) (typed FeaturePython)
  n = 0.002
FEATURE [App::DocumentObjectGroupPython] Cl_element003  label="Cl_element : 0.004"  # scripted group (container) (typed FeaturePython)
  n = 0.003
FEATURE [App::DocumentObjectGroupPython] K_element002  label="K_element : 0.003"  # scripted group (container) (typed FeaturePython)
  n = 0.003
FEATURE [App::DocumentObjectGroupPython] G4_BRAIN_ICRP  # scripted group (container) (typed FeaturePython)
  Dunit = g/cm3
  Dvalue = 1.04
  Group = -> [H_element017,C_element018,N_element012,O_element017,Na_element004,P_element004,S_element006,Cl_element003,K_element002]
  conduct = 2
  density = 1
  expand = 3
  formula = G4_BRAIN_ICRP
  name = G4_BRAIN_ICRP
  specific = 4
FEATURE [App::DocumentObjectGroupPython] C_element019  label="C_element : 4"  # scripted group (container) (typed FeaturePython)
  n = 4
  ref = C_element
FEATURE [App::DocumentObjectGroupPython] H_element018  label="H_element : 010"  # scripted group (container) (typed FeaturePython)
  n = 10
  ref = H_element
FEATURE [App::DocumentObjectGroupPython] G4_BUTANE  # scripted group (container) (typed FeaturePython)
  Dunit = g/cm3
  Dvalue = 0.00249343
  Group = -> [C_element019,H_element018]
  conduct = 2
  density = 1
  expand = 3
  formula = G4_BUTANE
  name = G4_BUTANE
  specific = 4
FEATURE [App::DocumentObjectGroupPython] C_element020  label="C_element : 008"  # scripted group (container) (typed FeaturePython)
  n = 4
  ref = C_element
FEATURE [App::DocumentObjectGroupPython] H_element019  label="H_element : 011"  # scripted group (container) (typed FeaturePython)
  n = 10
  ref = H_element
FEATURE [App::DocumentObjectGroupPython] O_element018  label="O_element : 007"  # scripted group (container) (typed FeaturePython)
  n = 1
  ref = O_element
FEATURE [App::DocumentObjectGroupPython] G4_N_BUTYL_ALCOHOL  label="G4_N-BUTYL_ALCOHOL"  # scripted group (container) (typed FeaturePython)
  Dunit = g/cm3
  Dvalue = 0.8098
  Group = -> [C_element020,H_element019,O_element018]
  conduct = 2
  density = 1
  expand = 3
  formula = G4_N-BUTYL_ALCOHOL
  name = G4_N-BUTYL_ALCOHOL
  specific = 4
FEATURE [App::DocumentObjectGroupPython] H_element020  label="H_element : 0.025"  # scripted group (container) (typed FeaturePython)
  n = 0.02468
FEATURE [App::DocumentObjectGroupPython] C_element021  label="C_element : 0.502"  # scripted group (container) (typed FeaturePython)
  n = 0.501611
FEATURE [App::DocumentObjectGroupPython] O_element019  label="O_element : 0.005"  # scripted group (container) (typed FeaturePython)
  n = 0.004527
FEATURE [App::DocumentObjectGroupPython] F_element004  label="F_element : 0.465"  # scripted group (container) (typed FeaturePython)
  n = 0.465209
FEATURE [App::DocumentObjectGroupPython] Si_element001  label="Si_element : 0.004"  # scripted group (container) (typed FeaturePython)
  n = 0.003973
FEATURE [App::DocumentObjectGroupPython] G4_C_552  label="G4_C-552"  # scripted group (container) (typed FeaturePython)
  Dunit = g/cm3
  Dvalue = 1.76
  Group = -> [H_element020,C_element021,O_element019,F_element004,Si_element001]
  conduct = 2
  density = 1
  expand = 3
  formula = G4_C-552
  name = G4_C-552
  specific = 4
FEATURE [App::DocumentObjectGroupPython] Cd_element001  label="Cd_element : 1"  # scripted group (container) (typed FeaturePython)
  n = 1
  ref = Cd_element
FEATURE [App::DocumentObjectGroupPython] Te_element001  label="Te_element : 1"  # scripted group (container) (typed FeaturePython)
  n = 1
  ref = Te_element
FEATURE [App::DocumentObjectGroupPython] G4_CADMIUM_TELLURIDE  # scripted group (container) (typed FeaturePython)
  Dunit = g/cm3
  Dvalue = 6.2
  Group = -> [Cd_element001,Te_element001]
  conduct = 2
  density = 1
  expand = 3
  formula = G4_CADMIUM_TELLURIDE
  name = G4_CADMIUM_TELLURIDE
  specific = 4
FEATURE [App::DocumentObjectGroupPython] Cd_element002  label="Cd_element : 002"  # scripted group (container) (typed FeaturePython)
  n = 1
  ref = Cd_element
FEATURE [App::DocumentObjectGroupPython] W_element001  label="W_element : 1"  # scripted group (container) (typed FeaturePython)
  n = 1
  ref = W_element
FEATURE [App::DocumentObjectGroupPython] O_element020  label="O_element : 008"  # scripted group (container) (typed FeaturePython)
  n = 4
  ref = O_element
FEATURE [App::DocumentObjectGroupPython] G4_CADMIUM_TUNGSTATE  # scripted group (container) (typed FeaturePython)
  Dunit = g/cm3
  Dvalue = 7.9
  Group = -> [Cd_element002,W_element001,O_element020]
  conduct = 2
  density = 1
  expand = 3
  formula = G4_CADMIUM_TUNGSTATE
  name = G4_CADMIUM_TUNGSTATE
  specific = 4
FEATURE [App::DocumentObjectGroupPython] Ca_element005  label="Ca_element : 1"  # scripted group (container) (typed FeaturePython)
  n = 1
  ref = Ca_element
FEATURE [App::DocumentObjectGroupPython] C_element022  label="C_element : 009"  # scripted group (container) (typed FeaturePython)
  n = 1
  ref = C_element
FEATURE [App::DocumentObjectGroupPython] O_element021  label="O_element : 009"  # scripted group (container) (typed FeaturePython)
  n = 3
  ref = O_element
FEATURE [App::DocumentObjectGroupPython] G4_CALCIUM_CARBONATE  # scripted group (container) (typed FeaturePython)
  Dunit = g/cm3
  Dvalue = 2.8
  Group = -> [Ca_element005,C_element022,O_element021]
  conduct = 2
  density = 1
  expand = 3
  formula = G4_CALCIUM_CARBONATE
  name = G4_CALCIUM_CARBONATE
  specific = 4
FEATURE [App::DocumentObjectGroupPython] Ca_element006  label="Ca_element : 002"  # scripted group (container) (typed FeaturePython)
  n = 1
  ref = Ca_element
FEATURE [App::DocumentObjectGroupPython] F_element005  label="F_element : 003"  # scripted group (container) (typed FeaturePython)
  n = 2
  ref = F_element
FEATURE [App::DocumentObjectGroupPython] G4_CALCIUM_FLUORIDE  # scripted group (container) (typed FeaturePython)
  Dunit = g/cm3
  Dvalue = 3.18
  Group = -> [Ca_element006,F_element005]
  conduct = 2
  density = 1
  expand = 3
  formula = G4_CALCIUM_FLUORIDE
  name = G4_CALCIUM_FLUORIDE
  specific = 4
FEATURE [App::DocumentObjectGroupPython] Ca_element007  label="Ca_element : 003"  # scripted group (container) (typed FeaturePython)
  n = 1
  ref = Ca_element
FEATURE [App::DocumentObjectGroupPython] O_element022  label="O_element : 010"  # scripted group (container) (typed FeaturePython)
  n = 1
  ref = O_element
FEATURE [App::DocumentObjectGroupPython] G4_CALCIUM_OXIDE  # scripted group (container) (typed FeaturePython)
  Dunit = g/cm3
  Dvalue = 3.3
  Group = -> [Ca_element007,O_element022]
  conduct = 2
  density = 1
  expand = 3
  formula = G4_CALCIUM_OXIDE
  name = G4_CALCIUM_OXIDE
  specific = 4
FEATURE [App::DocumentObjectGroupPython] Ca_element008  label="Ca_element : 004"  # scripted group (container) (typed FeaturePython)
  n = 1
  ref = Ca_element
FEATURE [App::DocumentObjectGroupPython] S_element007  label="S_element : 002"  # scripted group (container) (typed FeaturePython)
  n = 1
  ref = S_element
FEATURE [App::DocumentObjectGroupPython] O_element023  label="O_element : 011"  # scripted group (container) (typed FeaturePython)
  n = 4
  ref = O_element
FEATURE [App::DocumentObjectGroupPython] G4_CALCIUM_SULFATE  # scripted group (container) (typed FeaturePython)
  Dunit = g/cm3
  Dvalue = 2.96
  Group = -> [Ca_element008,S_element007,O_element023]
  conduct = 2
  density = 1
  expand = 3
  formula = G4_CALCIUM_SULFATE
  name = G4_CALCIUM_SULFATE
  specific = 4
FEATURE [App::DocumentObjectGroupPython] Ca_element009  label="Ca_element : 005"  # scripted group (container) (typed FeaturePython)
  n = 1
  ref = Ca_element
FEATURE [App::DocumentObjectGroupPython] W_element002  label="W_element : 002"  # scripted group (container) (typed FeaturePython)
  n = 1
  ref = W_element
FEATURE [App::DocumentObjectGroupPython] O_element024  label="O_element : 012"  # scripted group (container) (typed FeaturePython)
  n = 4
  ref = O_element
FEATURE [App::DocumentObjectGroupPython] G4_CALCIUM_TUNGSTATE  # scripted group (container) (typed FeaturePython)
  Dunit = g/cm3
  Dvalue = 6.062
  Group = -> [Ca_element009,W_element002,O_element024]
  conduct = 2
  density = 1
  expand = 3
  formula = G4_CALCIUM_TUNGSTATE
  name = G4_CALCIUM_TUNGSTATE
  specific = 4
FEATURE [App::DocumentObjectGroupPython] C_element023  label="C_element : 010"  # scripted group (container) (typed FeaturePython)
  n = 1
  ref = C_element
FEATURE [App::DocumentObjectGroupPython] O_element025  label="O_element : 013"  # scripted group (container) (typed FeaturePython)
  n = 2
  ref = O_element
FEATURE [App::DocumentObjectGroupPython] G4_CARBON_DIOXIDE  # scripted group (container) (typed FeaturePython)
  Dunit = g/cm3
  Dvalue = 0.00184212
  Group = -> [C_element023,O_element025]
  conduct = 2
  density = 1
  expand = 3
  formula = G4_CARBON_DIOXIDE
  name = G4_CARBON_DIOXIDE
  specific = 4
FEATURE [App::DocumentObjectGroupPython] C_element024  label="C_element : 011"  # scripted group (container) (typed FeaturePython)
  n = 1
  ref = C_element
FEATURE [App::DocumentObjectGroupPython] Cl_element004  label="Cl_element : 4"  # scripted group (container) (typed FeaturePython)
  n = 4
  ref = Cl_element
FEATURE [App::DocumentObjectGroupPython] G4_CARBON_TETRACHLORIDE  # scripted group (container) (typed FeaturePython)
  Dunit = g/cm3
  Dvalue = 1.594
  Group = -> [C_element024,Cl_element004]
  conduct = 2
  density = 1
  expand = 3
  formula = G4_CARBON_TETRACHLORIDE
  name = G4_CARBON_TETRACHLORIDE
  specific = 4
FEATURE [App::DocumentObjectGroupPython] C_element025  label="C_element : 012"  # scripted group (container) (typed FeaturePython)
  n = 6
  ref = C_element
FEATURE [App::DocumentObjectGroupPython] H_element021  label="H_element : 012"  # scripted group (container) (typed FeaturePython)
  n = 10
  ref = H_element
FEATURE [App::DocumentObjectGroupPython] O_element026  label="O_element : 5"  # scripted group (container) (typed FeaturePython)
  n = 5
  ref = O_element
FEATURE [App::DocumentObjectGroupPython] G4_CELLULOSE_CELLOPHANE  # scripted group (container) (typed FeaturePython)
  Dunit = g/cm3
  Dvalue = 1.42
  Group = -> [C_element025,H_element021,O_element026]
  conduct = 2
  density = 1
  expand = 3
  formula = G4_CELLULOSE_CELLOPHANE
  name = G4_CELLULOSE_CELLOPHANE
  specific = 4
FEATURE [App::DocumentObjectGroupPython] H_element022  label="H_element : 0.067"  # scripted group (container) (typed FeaturePython)
  n = 0.067125
FEATURE [App::DocumentObjectGroupPython] C_element026  label="C_element : 0.545"  # scripted group (container) (typed FeaturePython)
  n = 0.545403
FEATURE [App::DocumentObjectGroupPython] O_element027  label="O_element : 0.387"  # scripted group (container) (typed FeaturePython)
  n = 0.387472
FEATURE [App::DocumentObjectGroupPython] G4_CELLULOSE_BUTYRATE  # scripted group (container) (typed FeaturePython)
  Dunit = g/cm3
  Dvalue = 1.2
  Group = -> [H_element022,C_element026,O_element027]
  conduct = 2
  density = 1
  expand = 3
  formula = G4_CELLULOSE_BUTYRATE
  name = G4_CELLULOSE_BUTYRATE
  specific = 4
FEATURE [App::DocumentObjectGroupPython] H_element023  label="H_element : 0.029"  # scripted group (container) (typed FeaturePython)
  n = 0.029216
FEATURE [App::DocumentObjectGroupPython] C_element027  label="C_element : 0.271"  # scripted group (container) (typed FeaturePython)
  n = 0.271296
FEATURE [App::DocumentObjectGroupPython] N_element013  label="N_element : 0.121"  # scripted group (container) (typed FeaturePython)
  n = 0.121276
FEATURE [App::DocumentObjectGroupPython] O_element028  label="O_element : 0.578"  # scripted group (container) (typed FeaturePython)
  n = 0.578212
FEATURE [App::DocumentObjectGroupPython] G4_CELLULOSE_NITRATE  # scripted group (container) (typed FeaturePython)
  Dunit = g/cm3
  Dvalue = 1.49
  Group = -> [H_element023,C_element027,N_element013,O_element028]
  conduct = 2
  density = 1
  expand = 3
  formula = G4_CELLULOSE_NITRATE
  name = G4_CELLULOSE_NITRATE
  specific = 4
FEATURE [App::DocumentObjectGroupPython] H_element024  label="H_element : 0.108"  # scripted group (container) (typed FeaturePython)
  n = 0.107596
FEATURE [App::DocumentObjectGroupPython] N_element014  label="N_element : 0.001"  # scripted group (container) (typed FeaturePython)
  n = 0.0008
FEATURE [App::DocumentObjectGroupPython] O_element029  label="O_element : 0.875"  # scripted group (container) (typed FeaturePython)
  n = 0.874976
FEATURE [App::DocumentObjectGroupPython] S_element008  label="S_element : 0.015"  # scripted group (container) (typed FeaturePython)
  n = 0.014627
FEATURE [App::DocumentObjectGroupPython] Ce_element001  label="Ce_element : 0.002"  # scripted group (container) (typed FeaturePython)
  n = 0.002001
FEATURE [App::DocumentObjectGroupPython] G4_CERIC_SULFATE  # scripted group (container) (typed FeaturePython)
  Dunit = g/cm3
  Dvalue = 1.03
  Group = -> [H_element024,N_element014,O_element029,S_element008,Ce_element001]
  conduct = 2
  density = 1
  expand = 3
  formula = G4_CERIC_SULFATE
  name = G4_CERIC_SULFATE
  specific = 4
FEATURE [App::DocumentObjectGroupPython] Cs_element001  label="Cs_element : 1"  # scripted group (container) (typed FeaturePython)
  n = 1
  ref = Cs_element
FEATURE [App::DocumentObjectGroupPython] F_element006  label="F_element : 1"  # scripted group (container) (typed FeaturePython)
  n = 1
  ref = F_element
FEATURE [App::DocumentObjectGroupPython] G4_CESIUM_FLUORIDE  # scripted group (container) (typed FeaturePython)
  Dunit = g/cm3
  Dvalue = 4.115
  Group = -> [Cs_element001,F_element006]
  conduct = 2
  density = 1
  expand = 3
  formula = G4_CESIUM_FLUORIDE
  name = G4_CESIUM_FLUORIDE
  specific = 4
FEATURE [App::DocumentObjectGroupPython] Cs_element002  label="Cs_element : 002"  # scripted group (container) (typed FeaturePython)
  n = 1
  ref = Cs_element
FEATURE [App::DocumentObjectGroupPython] I_element001  label="I_element : 1"  # scripted group (container) (typed FeaturePython)
  n = 1
  ref = I_element
FEATURE [App::DocumentObjectGroupPython] G4_CESIUM_IODIDE  # scripted group (container) (typed FeaturePython)
  Dunit = g/cm3
  Dvalue = 4.51
  Group = -> [Cs_element002,I_element001]
  conduct = 2
  density = 1
  expand = 3
  formula = G4_CESIUM_IODIDE
  name = G4_CESIUM_IODIDE
  specific = 4
FEATURE [App::DocumentObjectGroupPython] C_element028  label="C_element : 013"  # scripted group (container) (typed FeaturePython)
  n = 6
  ref = C_element
FEATURE [App::DocumentObjectGroupPython] H_element025  label="H_element : 013"  # scripted group (container) (typed FeaturePython)
  n = 5
  ref = H_element
FEATURE [App::DocumentObjectGroupPython] Cl_element005  label="Cl_element : 1"  # scripted group (container) (typed FeaturePython)
  n = 1
  ref = Cl_element
FEATURE [App::DocumentObjectGroupPython] G4_CHLOROBENZENE  # scripted group (container) (typed FeaturePython)
  Dunit = g/cm3
  Dvalue = 1.1058
  Group = -> [C_element028,H_element025,Cl_element005]
  conduct = 2
  density = 1
  expand = 3
  formula = G4_CHLOROBENZENE
  name = G4_CHLOROBENZENE
  specific = 4
FEATURE [App::DocumentObjectGroupPython] C_element029  label="C_element : 014"  # scripted group (container) (typed FeaturePython)
  n = 1
  ref = C_element
FEATURE [App::DocumentObjectGroupPython] H_element026  label="H_element : 1"  # scripted group (container) (typed FeaturePython)
  n = 1
  ref = H_element
FEATURE [App::DocumentObjectGroupPython] Cl_element006  label="Cl_element : 3"  # scripted group (container) (typed FeaturePython)
  n = 3
  ref = Cl_element
FEATURE [App::DocumentObjectGroupPython] G4_CHLOROFORM  # scripted group (container) (typed FeaturePython)
  Dunit = g/cm3
  Dvalue = 1.4832
  Group = -> [C_element029,H_element026,Cl_element006]
  conduct = 2
  density = 1
  expand = 3
  formula = G4_CHLOROFORM
  name = G4_CHLOROFORM
  specific = 4
FEATURE [App::DocumentObjectGroupPython] H_element027  label="H_element : 0.010"  # scripted group (container) (typed FeaturePython)
  n = 0.01
FEATURE [App::DocumentObjectGroupPython] C_element030  label="C_element : 0.001"  # scripted group (container) (typed FeaturePython)
  n = 0.001
FEATURE [App::DocumentObjectGroupPython] O_element030  label="O_element : 0.529"  # scripted group (container) (typed FeaturePython)
  n = 0.529107
FEATURE [App::DocumentObjectGroupPython] Na_element005  label="Na_element : 0.016"  # scripted group (container) (typed FeaturePython)
  n = 0.016
FEATURE [App::DocumentObjectGroupPython] Mg_element003  label="Mg_element : 0.004"  # scripted group (container) (typed FeaturePython)
  n = 0.002
FEATURE [App::DocumentObjectGroupPython] Al_element002  label="Al_element : 0.034"  # scripted group (container) (typed FeaturePython)
  n = 0.033872
FEATURE [App::DocumentObjectGroupPython] Si_element002  label="Si_element : 0.337"  # scripted group (container) (typed FeaturePython)
  n = 0.337021
FEATURE [App::DocumentObjectGroupPython] K_element003  label="K_element : 0.013"  # scripted group (container) (typed FeaturePython)
  n = 0.013
FEATURE [App::DocumentObjectGroupPython] Ca_element010  label="Ca_element : 0.044"  # scripted group (container) (typed FeaturePython)
  n = 0.044
FEATURE [App::DocumentObjectGroupPython] Fe_element002  label="Fe_element : 0.014"  # scripted group (container) (typed FeaturePython)
  n = 0.014
FEATURE [App::DocumentObjectGroupPython] G4_CONCRETE  # scripted group (container) (typed FeaturePython)
  Dunit = g/cm3
  Dvalue = 2.3
  Group = -> [H_element027,C_element030,O_element030,Na_element005,Mg_element003,Al_element002,Si_element002,K_element003,Ca_element010,Fe_element002]
  conduct = 2
  density = 1
  expand = 3
  formula = G4_CONCRETE
  name = G4_CONCRETE
  specific = 4
FEATURE [App::DocumentObjectGroupPython] C_element031  label="C_element : 015"  # scripted group (container) (typed FeaturePython)
  n = 6
  ref = C_element
FEATURE [App::DocumentObjectGroupPython] H_element028  label="H_element : 12"  # scripted group (container) (typed FeaturePython)
  n = 12
  ref = H_element
FEATURE [App::DocumentObjectGroupPython] G4_CYCLOHEXANE  # scripted group (container) (typed FeaturePython)
  Dunit = g/cm3
  Dvalue = 0.779
  Group = -> [C_element031,H_element028]
  conduct = 2
  density = 1
  expand = 3
  formula = G4_CYCLOHEXANE
  name = G4_CYCLOHEXANE
  specific = 4
FEATURE [App::DocumentObjectGroupPython] C_element032  label="C_element : 016"  # scripted group (container) (typed FeaturePython)
  n = 6
  ref = C_element
FEATURE [App::DocumentObjectGroupPython] H_element029  label="H_element : 4"  # scripted group (container) (typed FeaturePython)
  n = 4
  ref = H_element
FEATURE [App::DocumentObjectGroupPython] Cl_element007  label="Cl_element : 2"  # scripted group (container) (typed FeaturePython)
  n = 2
  ref = Cl_element
FEATURE [App::DocumentObjectGroupPython] G4_1_2_DICHLOROBENZENE  label="G4_1.2-DICHLOROBENZENE"  # scripted group (container) (typed FeaturePython)
  Dunit = g/cm3
  Dvalue = 1.3048
  Group = -> [C_element032,H_element029,Cl_element007]
  conduct = 2
  density = 1
  expand = 3
  formula = G4_1.2-DICHLOROBENZENE
  name = G4_1.2-DICHLOROBENZENE
  specific = 4
FEATURE [App::DocumentObjectGroupPython] C_element033  label="C_element : 017"  # scripted group (container) (typed FeaturePython)
  n = 4
  ref = C_element
FEATURE [App::DocumentObjectGroupPython] H_element030  label="H_element : 8"  # scripted group (container) (typed FeaturePython)
  n = 8
  ref = H_element
FEATURE [App::DocumentObjectGroupPython] O_element031  label="O_element : 014"  # scripted group (container) (typed FeaturePython)
  n = 1
  ref = O_element
FEATURE [App::DocumentObjectGroupPython] Cl_element008  label="Cl_element : 005"  # scripted group (container) (typed FeaturePython)
  n = 2
  ref = Cl_element
FEATURE [App::DocumentObjectGroupPython] G4_DICHLORODIETHYL_ETHER  # scripted group (container) (typed FeaturePython)
  Dunit = g/cm3
  Dvalue = 1.2199
  Group = -> [C_element033,H_element030,O_element031,Cl_element008]
  conduct = 2
  density = 1
  expand = 3
  formula = G4_DICHLORODIETHYL_ETHER
  name = G4_DICHLORODIETHYL_ETHER
  specific = 4
FEATURE [App::DocumentObjectGroupPython] C_element034  label="C_element : 018"  # scripted group (container) (typed FeaturePython)
  n = 2
  ref = C_element
FEATURE [App::DocumentObjectGroupPython] H_element031  label="H_element : 014"  # scripted group (container) (typed FeaturePython)
  n = 4
  ref = H_element
FEATURE [App::DocumentObjectGroupPython] Cl_element009  label="Cl_element : 006"  # scripted group (container) (typed FeaturePython)
  n = 2
  ref = Cl_element
FEATURE [App::DocumentObjectGroupPython] G4_1_2_DICHLOROETHANE  label="G4_1.2-DICHLOROETHANE"  # scripted group (container) (typed FeaturePython)
  Dunit = g/cm3
  Dvalue = 1.2351
  Group = -> [C_element034,H_element031,Cl_element009]
  conduct = 2
  density = 1
  expand = 3
  formula = G4_1.2-DICHLOROETHANE
  name = G4_1.2-DICHLOROETHANE
  specific = 4
FEATURE [App::DocumentObjectGroupPython] C_element035  label="C_element : 019"  # scripted group (container) (typed FeaturePython)
  n = 4
  ref = C_element
FEATURE [App::DocumentObjectGroupPython] H_element032  label="H_element : 015"  # scripted group (container) (typed FeaturePython)
  n = 10
  ref = H_element
FEATURE [App::DocumentObjectGroupPython] O_element032  label="O_element : 015"  # scripted group (container) (typed FeaturePython)
  n = 1
  ref = O_element
FEATURE [App::DocumentObjectGroupPython] G4_DIETHYL_ETHER  # scripted group (container) (typed FeaturePython)
  Dunit = g/cm3
  Dvalue = 0.71378
  Group = -> [C_element035,H_element032,O_element032]
  conduct = 2
  density = 1
  expand = 3
  formula = G4_DIETHYL_ETHER
  name = G4_DIETHYL_ETHER
  specific = 4
FEATURE [App::DocumentObjectGroupPython] C_element036  label="C_element : 020"  # scripted group (container) (typed FeaturePython)
  n = 3
  ref = C_element
FEATURE [App::DocumentObjectGroupPython] H_element033  label="H_element : 016"  # scripted group (container) (typed FeaturePython)
  n = 7
  ref = H_element
FEATURE [App::DocumentObjectGroupPython] N_element015  label="N_element : 008"  # scripted group (container) (typed FeaturePython)
  n = 1
  ref = N_element
FEATURE [App::DocumentObjectGroupPython] O_element033  label="O_element : 016"  # scripted group (container) (typed FeaturePython)
  n = 1
  ref = O_element
FEATURE [App::DocumentObjectGroupPython] G4_N_N_DIMETHYL_FORMAMIDE  label="G4_N.N-DIMETHYL_FORMAMIDE"  # scripted group (container) (typed FeaturePython)
  Dunit = g/cm3
  Dvalue = 0.9487
  Group = -> [C_element036,H_element033,N_element015,O_element033]
  conduct = 2
  density = 1
  expand = 3
  formula = G4_N.N-DIMETHYL_FORMAMIDE
  name = G4_N.N-DIMETHYL_FORMAMIDE
  specific = 4
FEATURE [App::DocumentObjectGroupPython] C_element037  label="C_element : 021"  # scripted group (container) (typed FeaturePython)
  n = 2
  ref = C_element
FEATURE [App::DocumentObjectGroupPython] H_element034  label="H_element : 017"  # scripted group (container) (typed FeaturePython)
  n = 6
  ref = H_element
FEATURE [App::DocumentObjectGroupPython] O_element034  label="O_element : 017"  # scripted group (container) (typed FeaturePython)
  n = 1
  ref = O_element
FEATURE [App::DocumentObjectGroupPython] S_element009  label="S_element : 003"  # scripted group (container) (typed FeaturePython)
  n = 1
  ref = S_element
FEATURE [App::DocumentObjectGroupPython] G4_DIMETHYL_SULFOXIDE  # scripted group (container) (typed FeaturePython)
  Dunit = g/cm3
  Dvalue = 1.1014
  Group = -> [C_element037,H_element034,O_element034,S_element009]
  conduct = 2
  density = 1
  expand = 3
  formula = G4_DIMETHYL_SULFOXIDE
  name = G4_DIMETHYL_SULFOXIDE
  specific = 4
FEATURE [App::DocumentObjectGroupPython] C_element038  label="C_element : 022"  # scripted group (container) (typed FeaturePython)
  n = 2
  ref = C_element
FEATURE [App::DocumentObjectGroupPython] H_element035  label="H_element : 018"  # scripted group (container) (typed FeaturePython)
  n = 6
  ref = H_element
FEATURE [App::DocumentObjectGroupPython] G4_ETHANE  # scripted group (container) (typed FeaturePython)
  Dunit = g/cm3
  Dvalue = 0.00125324
  Group = -> [C_element038,H_element035]
  conduct = 2
  density = 1
  expand = 3
  formula = G4_ETHANE
  name = G4_ETHANE
  specific = 4
FEATURE [App::DocumentObjectGroupPython] C_element039  label="C_element : 023"  # scripted group (container) (typed FeaturePython)
  n = 2
  ref = C_element
FEATURE [App::DocumentObjectGroupPython] H_element036  label="H_element : 019"  # scripted group (container) (typed FeaturePython)
  n = 6
  ref = H_element
FEATURE [App::DocumentObjectGroupPython] O_element035  label="O_element : 018"  # scripted group (container) (typed FeaturePython)
  n = 1
  ref = O_element
FEATURE [App::DocumentObjectGroupPython] G4_ETHYL_ALCOHOL  # scripted group (container) (typed FeaturePython)
  Dunit = g/cm3
  Dvalue = 0.7893
  Group = -> [C_element039,H_element036,O_element035]
  conduct = 2
  density = 1
  expand = 3
  formula = G4_ETHYL_ALCOHOL
  name = G4_ETHYL_ALCOHOL
  specific = 4
FEATURE [App::DocumentObjectGroupPython] H_element037  label="H_element : 0.090"  # scripted group (container) (typed FeaturePython)
  n = 0.090027
FEATURE [App::DocumentObjectGroupPython] C_element040  label="C_element : 0.585"  # scripted group (container) (typed FeaturePython)
  n = 0.585182
FEATURE [App::DocumentObjectGroupPython] O_element036  label="O_element : 0.325"  # scripted group (container) (typed FeaturePython)
  n = 0.324791
FEATURE [App::DocumentObjectGroupPython] G4_ETHYL_CELLULOSE  # scripted group (container) (typed FeaturePython)
  Dunit = g/cm3
  Dvalue = 1.13
  Group = -> [H_element037,C_element040,O_element036]
  conduct = 2
  density = 1
  expand = 3
  formula = G4_ETHYL_CELLULOSE
  name = G4_ETHYL_CELLULOSE
  specific = 4
FEATURE [App::DocumentObjectGroupPython] C_element041  label="C_element : 024"  # scripted group (container) (typed FeaturePython)
  n = 2
  ref = C_element
FEATURE [App::DocumentObjectGroupPython] H_element038  label="H_element : 020"  # scripted group (container) (typed FeaturePython)
  n = 4
  ref = H_element
FEATURE [App::DocumentObjectGroupPython] G4_ETHYLENE  # scripted group (container) (typed FeaturePython)
  Dunit = g/cm3
  Dvalue = 0.00117497
  Group = -> [C_element041,H_element038]
  conduct = 2
  density = 1
  expand = 3
  formula = G4_ETHYLENE
  name = G4_ETHYLENE
  specific = 4
FEATURE [App::DocumentObjectGroupPython] H_element039  label="H_element : 0.096"  # scripted group (container) (typed FeaturePython)
  n = 0.096
FEATURE [App::DocumentObjectGroupPython] C_element042  label="C_element : 0.195"  # scripted group (container) (typed FeaturePython)
  n = 0.195
FEATURE [App::DocumentObjectGroupPython] N_element016  label="N_element : 0.057"  # scripted group (container) (typed FeaturePython)
  n = 0.057
FEATURE [App::DocumentObjectGroupPython] O_element037  label="O_element : 0.646"  # scripted group (container) (typed FeaturePython)
  n = 0.646
FEATURE [App::DocumentObjectGroupPython] Na_element006  label="Na_element : 0.017"  # scripted group (container) (typed FeaturePython)
  n = 0.001
FEATURE [App::DocumentObjectGroupPython] P_element005  label="P_element : 0.104"  # scripted group (container) (typed FeaturePython)
  n = 0.001
FEATURE [App::DocumentObjectGroupPython] S_element010  label="S_element : 0.016"  # scripted group (container) (typed FeaturePython)
  n = 0.003
FEATURE [App::DocumentObjectGroupPython] Cl_element010  label="Cl_element : 0.005"  # scripted group (container) (typed FeaturePython)
  n = 0.001
FEATURE [App::DocumentObjectGroupPython] G4_EYE_LENS_ICRP  # scripted group (container) (typed FeaturePython)
  Dunit = g/cm3
  Dvalue = 1.07
  Group = -> [H_element039,C_element042,N_element016,O_element037,Na_element006,P_element005,S_element010,Cl_element010]
  conduct = 2
  density = 1
  expand = 3
  formula = G4_EYE_LENS_ICRP
  name = G4_EYE_LENS_ICRP
  specific = 4
FEATURE [App::DocumentObjectGroupPython] Fe_element003  label="Fe_element : 2"  # scripted group (container) (typed FeaturePython)
  n = 2
  ref = Fe_element
FEATURE [App::DocumentObjectGroupPython] O_element038  label="O_element : 019"  # scripted group (container) (typed FeaturePython)
  n = 3
  ref = O_element
FEATURE [App::DocumentObjectGroupPython] G4_FERRIC_OXIDE  # scripted group (container) (typed FeaturePython)
  Dunit = g/cm3
  Dvalue = 5.2
  Group = -> [Fe_element003,O_element038]
  conduct = 2
  density = 1
  expand = 3
  formula = G4_FERRIC_OXIDE
  name = G4_FERRIC_OXIDE
  specific = 4
FEATURE [App::DocumentObjectGroupPython] Fe_element004  label="Fe_element : 1"  # scripted group (container) (typed FeaturePython)
  n = 1
  ref = Fe_element
FEATURE [App::DocumentObjectGroupPython] B_element003  label="B_element : 1"  # scripted group (container) (typed FeaturePython)
  n = 1
  ref = B_element
FEATURE [App::DocumentObjectGroupPython] G4_FERROBORIDE  # scripted group (container) (typed FeaturePython)
  Dunit = g/cm3
  Dvalue = 7.15
  Group = -> [Fe_element004,B_element003]
  conduct = 2
  density = 1
  expand = 3
  formula = G4_FERROBORIDE
  name = G4_FERROBORIDE
  specific = 4
FEATURE [App::DocumentObjectGroupPython] Fe_element005  label="Fe_element : 003"  # scripted group (container) (typed FeaturePython)
  n = 1
  ref = Fe_element
FEATURE [App::DocumentObjectGroupPython] O_element039  label="O_element : 020"  # scripted group (container) (typed FeaturePython)
  n = 1
  ref = O_element
FEATURE [App::DocumentObjectGroupPython] G4_FERROUS_OXIDE  # scripted group (container) (typed FeaturePython)
  Dunit = g/cm3
  Dvalue = 5.7
  Group = -> [Fe_element005,O_element039]
  conduct = 2
  density = 1
  expand = 3
  formula = G4_FERROUS_OXIDE
  name = G4_FERROUS_OXIDE
  specific = 4
FEATURE [App::DocumentObjectGroupPython] H_element040  label="H_element : 0.115"  # scripted group (container) (typed FeaturePython)
  n = 0.108259
FEATURE [App::DocumentObjectGroupPython] N_element017  label="N_element : 0.000"  # scripted group (container) (typed FeaturePython)
  n = 2.7e-05
FEATURE [App::DocumentObjectGroupPython] O_element040  label="O_element : 0.879"  # scripted group (container) (typed FeaturePython)
  n = 0.878636
FEATURE [App::DocumentObjectGroupPython] Na_element007  label="Na_element : 0.000"  # scripted group (container) (typed FeaturePython)
  n = 2.2e-05
FEATURE [App::DocumentObjectGroupPython] S_element011  label="S_element : 0.013"  # scripted group (container) (typed FeaturePython)
  n = 0.012968
FEATURE [App::DocumentObjectGroupPython] Cl_element011  label="Cl_element : 0.000"  # scripted group (container) (typed FeaturePython)
  n = 3.4e-05
FEATURE [App::DocumentObjectGroupPython] Fe_element006  label="Fe_element : 0.000"  # scripted group (container) (typed FeaturePython)
  n = 5.4e-05
FEATURE [App::DocumentObjectGroupPython] G4_FERROUS_SULFATE  # scripted group (container) (typed FeaturePython)
  Dunit = g/cm3
  Dvalue = 1.024
  Group = -> [H_element040,N_element017,O_element040,Na_element007,S_element011,Cl_element011,Fe_element006]
  conduct = 2
  density = 1
  expand = 3
  formula = G4_FERROUS_SULFATE
  name = G4_FERROUS_SULFATE
  specific = 4
FEATURE [App::DocumentObjectGroupPython] C_element043  label="C_element : 0.099"  # scripted group (container) (typed FeaturePython)
  n = 0.099335
FEATURE [App::DocumentObjectGroupPython] F_element007  label="F_element : 0.314"  # scripted group (container) (typed FeaturePython)
  n = 0.314247
FEATURE [App::DocumentObjectGroupPython] Cl_element012  label="Cl_element : 0.586"  # scripted group (container) (typed FeaturePython)
  n = 0.586418
FEATURE [App::DocumentObjectGroupPython] G4_FREON_12  label="G4_FREON-12"  # scripted group (container) (typed FeaturePython)
  Dunit = g/cm3
  Dvalue = 1.12
  Group = -> [C_element043,F_element007,Cl_element012]
  conduct = 2
  density = 1
  expand = 3
  formula = G4_FREON-12
  name = G4_FREON-12
  specific = 4
FEATURE [App::DocumentObjectGroupPython] C_element044  label="C_element : 0.057"  # scripted group (container) (typed FeaturePython)
  n = 0.057245
FEATURE [App::DocumentObjectGroupPython] F_element008  label="F_element : 0.181"  # scripted group (container) (typed FeaturePython)
  n = 0.181096
FEATURE [App::DocumentObjectGroupPython] Br_element001  label="Br_element : 0.762"  # scripted group (container) (typed FeaturePython)
  n = 0.761659
FEATURE [App::DocumentObjectGroupPython] G4_FREON_12B2  label="G4_FREON-12B2"  # scripted group (container) (typed FeaturePython)
  Dunit = g/cm3
  Dvalue = 1.8
  Group = -> [C_element044,F_element008,Br_element001]
  conduct = 2
  density = 1
  expand = 3
  formula = G4_FREON-12B2
  name = G4_FREON-12B2
  specific = 4
FEATURE [App::DocumentObjectGroupPython] C_element045  label="C_element : 0.115"  # scripted group (container) (typed FeaturePython)
  n = 0.114983
FEATURE [App::DocumentObjectGroupPython] F_element009  label="F_element : 0.546"  # scripted group (container) (typed FeaturePython)
  n = 0.545621
FEATURE [App::DocumentObjectGroupPython] Cl_element013  label="Cl_element : 0.339"  # scripted group (container) (typed FeaturePython)
  n = 0.339396
FEATURE [App::DocumentObjectGroupPython] G4_FREON_13  label="G4_FREON-13"  # scripted group (container) (typed FeaturePython)
  Dunit = g/cm3
  Dvalue = 0.95
  Group = -> [C_element045,F_element009,Cl_element013]
  conduct = 2
  density = 1
  expand = 3
  formula = G4_FREON-13
  name = G4_FREON-13
  specific = 4
FEATURE [App::DocumentObjectGroupPython] C_element046  label="C_element : 025"  # scripted group (container) (typed FeaturePython)
  n = 1
  ref = C_element
FEATURE [App::DocumentObjectGroupPython] F_element010  label="F_element : 3"  # scripted group (container) (typed FeaturePython)
  n = 3
  ref = F_element
FEATURE [App::DocumentObjectGroupPython] Br_element002  label="Br_element : 1"  # scripted group (container) (typed FeaturePython)
  n = 1
  ref = Br_element
FEATURE [App::DocumentObjectGroupPython] G4_FREON_13B1  label="G4_FREON-13B1"  # scripted group (container) (typed FeaturePython)
  Dunit = g/cm3
  Dvalue = 1.5
  Group = -> [C_element046,F_element010,Br_element002]
  conduct = 2
  density = 1
  expand = 3
  formula = G4_FREON-13B1
  name = G4_FREON-13B1
  specific = 4
FEATURE [App::DocumentObjectGroupPython] C_element047  label="C_element : 0.061"  # scripted group (container) (typed FeaturePython)
  n = 0.061309
FEATURE [App::DocumentObjectGroupPython] F_element011  label="F_element : 0.291"  # scripted group (container) (typed FeaturePython)
  n = 0.290924
FEATURE [App::DocumentObjectGroupPython] I_element002  label="I_element : 0.648"  # scripted group (container) (typed FeaturePython)
  n = 0.647767
FEATURE [App::DocumentObjectGroupPython] G4_FREON_13I1  label="G4_FREON-13I1"  # scripted group (container) (typed FeaturePython)
  Dunit = g/cm3
  Dvalue = 1.8
  Group = -> [C_element047,F_element011,I_element002]
  conduct = 2
  density = 1
  expand = 3
  formula = G4_FREON-13I1
  name = G4_FREON-13I1
  specific = 4
FEATURE [App::DocumentObjectGroupPython] Gd_element001  label="Gd_element : 2"  # scripted group (container) (typed FeaturePython)
  n = 2
  ref = Gd_element
FEATURE [App::DocumentObjectGroupPython] O_element041  label="O_element : 021"  # scripted group (container) (typed FeaturePython)
  n = 2
  ref = O_element
FEATURE [App::DocumentObjectGroupPython] S_element012  label="S_element : 004"  # scripted group (container) (typed FeaturePython)
  n = 1
  ref = S_element
FEATURE [App::DocumentObjectGroupPython] G4_GADOLINIUM_OXYSULFIDE  # scripted group (container) (typed FeaturePython)
  Dunit = g/cm3
  Dvalue = 7.44
  Group = -> [Gd_element001,O_element041,S_element012]
  conduct = 2
  density = 1
  expand = 3
  formula = G4_GADOLINIUM_OXYSULFIDE
  name = G4_GADOLINIUM_OXYSULFIDE
  specific = 4
FEATURE [App::DocumentObjectGroupPython] Ga_element001  label="Ga_element : 1"  # scripted group (container) (typed FeaturePython)
  n = 1
  ref = Ga_element
FEATURE [App::DocumentObjectGroupPython] As_element001  label="As_element : 1"  # scripted group (container) (typed FeaturePython)
  n = 1
  ref = As_element
FEATURE [App::DocumentObjectGroupPython] G4_GALLIUM_ARSENIDE  # scripted group (container) (typed FeaturePython)
  Dunit = g/cm3
  Dvalue = 5.31
  Group = -> [Ga_element001,As_element001]
  conduct = 2
  density = 1
  expand = 3
  formula = G4_GALLIUM_ARSENIDE
  name = G4_GALLIUM_ARSENIDE
  specific = 4
FEATURE [App::DocumentObjectGroupPython] H_element041  label="H_element : 0.081"  # scripted group (container) (typed FeaturePython)
  n = 0.08118
FEATURE [App::DocumentObjectGroupPython] C_element048  label="C_element : 0.416"  # scripted group (container) (typed FeaturePython)
  n = 0.41606
FEATURE [App::DocumentObjectGroupPython] N_element018  label="N_element : 0.111"  # scripted group (container) (typed FeaturePython)
  n = 0.11124
FEATURE [App::DocumentObjectGroupPython] O_element042  label="O_element : 0.381"  # scripted group (container) (typed FeaturePython)
  n = 0.38064
FEATURE [App::DocumentObjectGroupPython] S_element013  label="S_element : 0.011"  # scripted group (container) (typed FeaturePython)
  n = 0.01088
FEATURE [App::DocumentObjectGroupPython] G4_GEL_PHOTO_EMULSION  # scripted group (container) (typed FeaturePython)
  Dunit = g/cm3
  Dvalue = 1.2914
  Group = -> [H_element041,C_element048,N_element018,O_element042,S_element013]
  conduct = 2
  density = 1
  expand = 3
  formula = G4_GEL_PHOTO_EMULSION
  name = G4_GEL_PHOTO_EMULSION
  specific = 4
FEATURE [App::DocumentObjectGroupPython] B_element004  label="B_element : 0.040"  # scripted group (container) (typed FeaturePython)
  n = 0.0400639
FEATURE [App::DocumentObjectGroupPython] O_element043  label="O_element : 0.540"  # scripted group (container) (typed FeaturePython)
  n = 0.539561
FEATURE [App::DocumentObjectGroupPython] Na_element008  label="Na_element : 0.028"  # scripted group (container) (typed FeaturePython)
  n = 0.0281909
FEATURE [App::DocumentObjectGroupPython] Al_element003  label="Al_element : 0.012"  # scripted group (container) (typed FeaturePython)
  n = 0.011644
FEATURE [App::DocumentObjectGroupPython] Si_element003  label="Si_element : 0.377"  # scripted group (container) (typed FeaturePython)
  n = 0.377219
FEATURE [App::DocumentObjectGroupPython] K_element004  label="K_element : 0.014"  # scripted group (container) (typed FeaturePython)
  n = 0.00332099
FEATURE [App::DocumentObjectGroupPython] G4_Pyrex_Glass  # scripted group (container) (typed FeaturePython)
  Dunit = g/cm3
  Dvalue = 2.23
  Group = -> [B_element004,O_element043,Na_element008,Al_element003,Si_element003,K_element004]
  conduct = 2
  density = 1
  expand = 3
  formula = G4_Pyrex_Glass
  name = G4_Pyrex_Glass
  specific = 4
FEATURE [App::DocumentObjectGroupPython] O_element044  label="O_element : 0.156"  # scripted group (container) (typed FeaturePython)
  n = 0.156453
FEATURE [App::DocumentObjectGroupPython] Si_element004  label="Si_element : 0.081"  # scripted group (container) (typed FeaturePython)
  n = 0.080866
FEATURE [App::DocumentObjectGroupPython] Ti_element001  label="Ti_element : 0.008"  # scripted group (container) (typed FeaturePython)
  n = 0.008092
FEATURE [App::DocumentObjectGroupPython] As_element002  label="As_element : 0.003"  # scripted group (container) (typed FeaturePython)
  n = 0.002651
FEATURE [App::DocumentObjectGroupPython] Pb_element001  label="Pb_element : 0.752"  # scripted group (container) (typed FeaturePython)
  n = 0.751938
FEATURE [App::DocumentObjectGroupPython] G4_GLASS_LEAD  # scripted group (container) (typed FeaturePython)
  Dunit = g/cm3
  Dvalue = 6.22
  Group = -> [O_element044,Si_element004,Ti_element001,As_element002,Pb_element001]
  conduct = 2
  density = 1
  expand = 3
  formula = G4_GLASS_LEAD
  name = G4_GLASS_LEAD
  specific = 4
FEATURE [App::DocumentObjectGroupPython] O_element045  label="O_element : 0.460"  # scripted group (container) (typed FeaturePython)
  n = 0.4598
FEATURE [App::DocumentObjectGroupPython] Na_element009  label="Na_element : 0.096"  # scripted group (container) (typed FeaturePython)
  n = 0.0964411
FEATURE [App::DocumentObjectGroupPython] Si_element005  label="Si_element : 0.378"  # scripted group (container) (typed FeaturePython)
  n = 0.336553
FEATURE [App::DocumentObjectGroupPython] Ca_element011  label="Ca_element : 0.107"  # scripted group (container) (typed FeaturePython)
  n = 0.107205
FEATURE [App::DocumentObjectGroupPython] G4_GLASS_PLATE  # scripted group (container) (typed FeaturePython)
  Dunit = g/cm3
  Dvalue = 2.4
  Group = -> [O_element045,Na_element009,Si_element005,Ca_element011]
  conduct = 2
  density = 1
  expand = 3
  formula = G4_GLASS_PLATE
  name = G4_GLASS_PLATE
  specific = 4
FEATURE [App::DocumentObjectGroupPython] C_element049  label="C_element : 026"  # scripted group (container) (typed FeaturePython)
  n = 5
  ref = C_element
FEATURE [App::DocumentObjectGroupPython] H_element042  label="H_element : 021"  # scripted group (container) (typed FeaturePython)
  n = 10
  ref = H_element
FEATURE [App::DocumentObjectGroupPython] N_element019  label="N_element : 2"  # scripted group (container) (typed FeaturePython)
  n = 2
  ref = N_element
FEATURE [App::DocumentObjectGroupPython] O_element046  label="O_element : 022"  # scripted group (container) (typed FeaturePython)
  n = 3
  ref = O_element
FEATURE [App::DocumentObjectGroupPython] G4_GLUTAMINE  # scripted group (container) (typed FeaturePython)
  Dunit = g/cm3
  Dvalue = 1.46
  Group = -> [C_element049,H_element042,N_element019,O_element046]
  conduct = 2
  density = 1
  expand = 3
  formula = G4_GLUTAMINE
  name = G4_GLUTAMINE
  specific = 4
FEATURE [App::DocumentObjectGroupPython] C_element050  label="C_element : 027"  # scripted group (container) (typed FeaturePython)
  n = 3
  ref = C_element
FEATURE [App::DocumentObjectGroupPython] H_element043  label="H_element : 022"  # scripted group (container) (typed FeaturePython)
  n = 8
  ref = H_element
FEATURE [App::DocumentObjectGroupPython] O_element047  label="O_element : 023"  # scripted group (container) (typed FeaturePython)
  n = 3
  ref = O_element
FEATURE [App::DocumentObjectGroupPython] G4_GLYCEROL  # scripted group (container) (typed FeaturePython)
  Dunit = g/cm3
  Dvalue = 1.2613
  Group = -> [C_element050,H_element043,O_element047]
  conduct = 2
  density = 1
  expand = 3
  formula = G4_GLYCEROL
  name = G4_GLYCEROL
  specific = 4
FEATURE [App::DocumentObjectGroupPython] C_element051  label="C_element : 028"  # scripted group (container) (typed FeaturePython)
  n = 5
  ref = C_element
FEATURE [App::DocumentObjectGroupPython] H_element044  label="H_element : 023"  # scripted group (container) (typed FeaturePython)
  n = 5
  ref = H_element
FEATURE [App::DocumentObjectGroupPython] N_element020  label="N_element : 009"  # scripted group (container) (typed FeaturePython)
  n = 5
  ref = N_element
FEATURE [App::DocumentObjectGroupPython] O_element048  label="O_element : 024"  # scripted group (container) (typed FeaturePython)
  n = 1
  ref = O_element
FEATURE [App::DocumentObjectGroupPython] G4_GUANINE  # scripted group (container) (typed FeaturePython)
  Dunit = g/cm3
  Dvalue = 2.2
  Group = -> [C_element051,H_element044,N_element020,O_element048]
  conduct = 2
  density = 1
  expand = 3
  formula = G4_GUANINE
  name = G4_GUANINE
  specific = 4
FEATURE [App::DocumentObjectGroupPython] Ca_element012  label="Ca_element : 006"  # scripted group (container) (typed FeaturePython)
  n = 1
  ref = Ca_element
FEATURE [App::DocumentObjectGroupPython] S_element014  label="S_element : 005"  # scripted group (container) (typed FeaturePython)
  n = 1
  ref = S_element
FEATURE [App::DocumentObjectGroupPython] O_element049  label="O_element : 6"  # scripted group (container) (typed FeaturePython)
  n = 6
  ref = O_element
FEATURE [App::DocumentObjectGroupPython] H_element045  label="H_element : 024"  # scripted group (container) (typed FeaturePython)
  n = 4
  ref = H_element
FEATURE [App::DocumentObjectGroupPython] G4_GYPSUM  # scripted group (container) (typed FeaturePython)
  Dunit = g/cm3
  Dvalue = 2.32
  Group = -> [Ca_element012,S_element014,O_element049,H_element045]
  conduct = 2
  density = 1
  expand = 3
  formula = G4_GYPSUM
  name = G4_GYPSUM
  specific = 4
FEATURE [App::DocumentObjectGroupPython] C_element052  label="C_element : 7"  # scripted group (container) (typed FeaturePython)
  n = 7
  ref = C_element
FEATURE [App::DocumentObjectGroupPython] H_element046  label="H_element : 16"  # scripted group (container) (typed FeaturePython)
  n = 16
  ref = H_element
FEATURE [App::DocumentObjectGroupPython] G4_N_HEPTANE  label="G4_N-HEPTANE"  # scripted group (container) (typed FeaturePython)
  Dunit = g/cm3
  Dvalue = 0.68376
  Group = -> [C_element052,H_element046]
  conduct = 2
  density = 1
  expand = 3
  formula = G4_N-HEPTANE
  name = G4_N-HEPTANE
  specific = 4
FEATURE [App::DocumentObjectGroupPython] C_element053  label="C_element : 029"  # scripted group (container) (typed FeaturePython)
  n = 6
  ref = C_element
FEATURE [App::DocumentObjectGroupPython] H_element047  label="H_element : 14"  # scripted group (container) (typed FeaturePython)
  n = 14
  ref = H_element
FEATURE [App::DocumentObjectGroupPython] G4_N_HEXANE  label="G4_N-HEXANE"  # scripted group (container) (typed FeaturePython)
  Dunit = g/cm3
  Dvalue = 0.6603
  Group = -> [C_element053,H_element047]
  conduct = 2
  density = 1
  expand = 3
  formula = G4_N-HEXANE
  name = G4_N-HEXANE
  specific = 4
FEATURE [App::DocumentObjectGroupPython] C_element054  label="C_element : 22"  # scripted group (container) (typed FeaturePython)
  n = 22
  ref = C_element
FEATURE [App::DocumentObjectGroupPython] H_element048  label="H_element : 025"  # scripted group (container) (typed FeaturePython)
  n = 10
  ref = H_element
FEATURE [App::DocumentObjectGroupPython] N_element021  label="N_element : 010"  # scripted group (container) (typed FeaturePython)
  n = 2
  ref = N_element
FEATURE [App::DocumentObjectGroupPython] O_element050  label="O_element : 025"  # scripted group (container) (typed FeaturePython)
  n = 5
  ref = O_element
FEATURE [App::DocumentObjectGroupPython] G4_KAPTON  # scripted group (container) (typed FeaturePython)
  Dunit = g/cm3
  Dvalue = 1.42
  Group = -> [C_element054,H_element048,N_element021,O_element050]
  conduct = 2
  density = 1
  expand = 3
  formula = G4_KAPTON
  name = G4_KAPTON
  specific = 4
FEATURE [App::DocumentObjectGroupPython] La_element001  label="La_element : 1"  # scripted group (container) (typed FeaturePython)
  n = 1
  ref = La_element
FEATURE [App::DocumentObjectGroupPython] Br_element003  label="Br_element : 002"  # scripted group (container) (typed FeaturePython)
  n = 1
  ref = Br_element
FEATURE [App::DocumentObjectGroupPython] O_element051  label="O_element : 026"  # scripted group (container) (typed FeaturePython)
  n = 1
  ref = O_element
FEATURE [App::DocumentObjectGroupPython] G4_LANTHANUM_OXYBROMIDE  # scripted group (container) (typed FeaturePython)
  Dunit = g/cm3
  Dvalue = 6.28
  Group = -> [La_element001,Br_element003,O_element051]
  conduct = 2
  density = 1
  expand = 3
  formula = G4_LANTHANUM_OXYBROMIDE
  name = G4_LANTHANUM_OXYBROMIDE
  specific = 4
FEATURE [App::DocumentObjectGroupPython] La_element002  label="La_element : 2"  # scripted group (container) (typed FeaturePython)
  n = 2
  ref = La_element
FEATURE [App::DocumentObjectGroupPython] O_element052  label="O_element : 027"  # scripted group (container) (typed FeaturePython)
  n = 2
  ref = O_element
FEATURE [App::DocumentObjectGroupPython] S_element015  label="S_element : 006"  # scripted group (container) (typed FeaturePython)
  n = 1
  ref = S_element
FEATURE [App::DocumentObjectGroupPython] G4_LANTHANUM_OXYSULFIDE  # scripted group (container) (typed FeaturePython)
  Dunit = g/cm3
  Dvalue = 5.86
  Group = -> [La_element002,O_element052,S_element015]
  conduct = 2
  density = 1
  expand = 3
  formula = G4_LANTHANUM_OXYSULFIDE
  name = G4_LANTHANUM_OXYSULFIDE
  specific = 4
FEATURE [App::DocumentObjectGroupPython] O_element053  label="O_element : 0.072"  # scripted group (container) (typed FeaturePython)
  n = 0.071682
FEATURE [App::DocumentObjectGroupPython] Pb_element002  label="Pb_element : 0.928"  # scripted group (container) (typed FeaturePython)
  n = 0.928318
FEATURE [App::DocumentObjectGroupPython] G4_LEAD_OXIDE  # scripted group (container) (typed FeaturePython)
  Dunit = g/cm3
  Dvalue = 9.53
  Group = -> [O_element053,Pb_element002]
  conduct = 2
  density = 1
  expand = 3
  formula = G4_LEAD_OXIDE
  name = G4_LEAD_OXIDE
  specific = 4
FEATURE [App::DocumentObjectGroupPython] Li_element001  label="Li_element : 1"  # scripted group (container) (typed FeaturePython)
  n = 1
  ref = Li_element
FEATURE [App::DocumentObjectGroupPython] N_element022  label="N_element : 011"  # scripted group (container) (typed FeaturePython)
  n = 1
  ref = N_element
FEATURE [App::DocumentObjectGroupPython] H_element049  label="H_element : 026"  # scripted group (container) (typed FeaturePython)
  n = 2
  ref = H_element
FEATURE [App::DocumentObjectGroupPython] G4_LITHIUM_AMIDE  # scripted group (container) (typed FeaturePython)
  Dunit = g/cm3
  Dvalue = 1.178
  Group = -> [Li_element001,N_element022,H_element049]
  conduct = 2
  density = 1
  expand = 3
  formula = G4_LITHIUM_AMIDE
  name = G4_LITHIUM_AMIDE
  specific = 4
FEATURE [App::DocumentObjectGroupPython] Li_element002  label="Li_element : 2"  # scripted group (container) (typed FeaturePython)
  n = 2
  ref = Li_element
FEATURE [App::DocumentObjectGroupPython] C_element055  label="C_element : 030"  # scripted group (container) (typed FeaturePython)
  n = 1
  ref = C_element
FEATURE [App::DocumentObjectGroupPython] O_element054  label="O_element : 028"  # scripted group (container) (typed FeaturePython)
  n = 3
  ref = O_element
FEATURE [App::DocumentObjectGroupPython] G4_LITHIUM_CARBONATE  # scripted group (container) (typed FeaturePython)
  Dunit = g/cm3
  Dvalue = 2.11
  Group = -> [Li_element002,C_element055,O_element054]
  conduct = 2
  density = 1
  expand = 3
  formula = G4_LITHIUM_CARBONATE
  name = G4_LITHIUM_CARBONATE
  specific = 4
FEATURE [App::DocumentObjectGroupPython] Li_element003  label="Li_element : 003"  # scripted group (container) (typed FeaturePython)
  n = 1
  ref = Li_element
FEATURE [App::DocumentObjectGroupPython] F_element012  label="F_element : 004"  # scripted group (container) (typed FeaturePython)
  n = 1
  ref = F_element
FEATURE [App::DocumentObjectGroupPython] G4_LITHIUM_FLUORIDE  # scripted group (container) (typed FeaturePython)
  Dunit = g/cm3
  Dvalue = 2.635
  Group = -> [Li_element003,F_element012]
  conduct = 2
  density = 1
  expand = 3
  formula = G4_LITHIUM_FLUORIDE
  name = G4_LITHIUM_FLUORIDE
  specific = 4
FEATURE [App::DocumentObjectGroupPython] Li_element004  label="Li_element : 004"  # scripted group (container) (typed FeaturePython)
  n = 1
  ref = Li_element
FEATURE [App::DocumentObjectGroupPython] H_element050  label="H_element : 027"  # scripted group (container) (typed FeaturePython)
  n = 1
  ref = H_element
FEATURE [App::DocumentObjectGroupPython] G4_LITHIUM_HYDRIDE  # scripted group (container) (typed FeaturePython)
  Dunit = g/cm3
  Dvalue = 0.82
  Group = -> [Li_element004,H_element050]
  conduct = 2
  density = 1
  expand = 3
  formula = G4_LITHIUM_HYDRIDE
  name = G4_LITHIUM_HYDRIDE
  specific = 4
FEATURE [App::DocumentObjectGroupPython] Li_element005  label="Li_element : 005"  # scripted group (container) (typed FeaturePython)
  n = 1
  ref = Li_element
FEATURE [App::DocumentObjectGroupPython] I_element003  label="I_element : 002"  # scripted group (container) (typed FeaturePython)
  n = 1
  ref = I_element
FEATURE [App::DocumentObjectGroupPython] G4_LITHIUM_IODIDE  # scripted group (container) (typed FeaturePython)
  Dunit = g/cm3
  Dvalue = 3.494
  Group = -> [Li_element005,I_element003]
  conduct = 2
  density = 1
  expand = 3
  formula = G4_LITHIUM_IODIDE
  name = G4_LITHIUM_IODIDE
  specific = 4
FEATURE [App::DocumentObjectGroupPython] Li_element006  label="Li_element : 006"  # scripted group (container) (typed FeaturePython)
  n = 2
  ref = Li_element
FEATURE [App::DocumentObjectGroupPython] O_element055  label="O_element : 029"  # scripted group (container) (typed FeaturePython)
  n = 1
  ref = O_element
FEATURE [App::DocumentObjectGroupPython] G4_LITHIUM_OXIDE  # scripted group (container) (typed FeaturePython)
  Dunit = g/cm3
  Dvalue = 2.013
  Group = -> [Li_element006,O_element055]
  conduct = 2
  density = 1
  expand = 3
  formula = G4_LITHIUM_OXIDE
  name = G4_LITHIUM_OXIDE
  specific = 4
FEATURE [App::DocumentObjectGroupPython] Li_element007  label="Li_element : 007"  # scripted group (container) (typed FeaturePython)
  n = 2
  ref = Li_element
FEATURE [App::DocumentObjectGroupPython] B_element005  label="B_element : 005"  # scripted group (container) (typed FeaturePython)
  n = 4
  ref = B_element
FEATURE [App::DocumentObjectGroupPython] O_element056  label="O_element : 7"  # scripted group (container) (typed FeaturePython)
  n = 7
  ref = O_element
FEATURE [App::DocumentObjectGroupPython] G4_LITHIUM_TETRABORATE  # scripted group (container) (typed FeaturePython)
  Dunit = g/cm3
  Dvalue = 2.44
  Group = -> [Li_element007,B_element005,O_element056]
  conduct = 2
  density = 1
  expand = 3
  formula = G4_LITHIUM_TETRABORATE
  name = G4_LITHIUM_TETRABORATE
  specific = 4
FEATURE [App::DocumentObjectGroupPython] H_element051  label="H_element : 0.105"  # scripted group (container) (typed FeaturePython)
  n = 0.105
FEATURE [App::DocumentObjectGroupPython] C_element056  label="C_element : 0.083"  # scripted group (container) (typed FeaturePython)
  n = 0.083
FEATURE [App::DocumentObjectGroupPython] N_element023  label="N_element : 0.023"  # scripted group (container) (typed FeaturePython)
  n = 0.023
FEATURE [App::DocumentObjectGroupPython] O_element057  label="O_element : 0.779"  # scripted group (container) (typed FeaturePython)
  n = 0.779
FEATURE [App::DocumentObjectGroupPython] Na_element010  label="Na_element : 0.097"  # scripted group (container) (typed FeaturePython)
  n = 0.002
FEATURE [App::DocumentObjectGroupPython] P_element006  label="P_element : 0.105"  # scripted group (container) (typed FeaturePython)
  n = 0.001
FEATURE [App::DocumentObjectGroupPython] S_element016  label="S_element : 0.017"  # scripted group (container) (typed FeaturePython)
  n = 0.002
FEATURE [App::DocumentObjectGroupPython] Cl_element014  label="Cl_element : 0.587"  # scripted group (container) (typed FeaturePython)
  n = 0.003
FEATURE [App::DocumentObjectGroupPython] K_element005  label="K_element : 0.015"  # scripted group (container) (typed FeaturePython)
  n = 0.002
FEATURE [App::DocumentObjectGroupPython] G4_LUNG_ICRP  # scripted group (container) (typed FeaturePython)
  Dunit = g/cm3
  Dvalue = 1.04
  Group = -> [H_element051,C_element056,N_element023,O_element057,Na_element010,P_element006,S_element016,Cl_element014,K_element005]
  conduct = 2
  density = 1
  expand = 3
  formula = G4_LUNG_ICRP
  name = G4_LUNG_ICRP
  specific = 4
FEATURE [App::DocumentObjectGroupPython] H_element052  label="H_element : 0.116"  # scripted group (container) (typed FeaturePython)
  n = 0.114318
FEATURE [App::DocumentObjectGroupPython] C_element057  label="C_element : 0.656"  # scripted group (container) (typed FeaturePython)
  n = 0.655824
FEATURE [App::DocumentObjectGroupPython] O_element058  label="O_element : 0.092"  # scripted group (container) (typed FeaturePython)
  n = 0.0921831
FEATURE [App::DocumentObjectGroupPython] Mg_element004  label="Mg_element : 0.135"  # scripted group (container) (typed FeaturePython)
  n = 0.134792
FEATURE [App::DocumentObjectGroupPython] Ca_element013  label="Ca_element : 0.003"  # scripted group (container) (typed FeaturePython)
  n = 0.002883
FEATURE [App::DocumentObjectGroupPython] G4_M3_WAX  # scripted group (container) (typed FeaturePython)
  Dunit = g/cm3
  Dvalue = 1.05
  Group = -> [H_element052,C_element057,O_element058,Mg_element004,Ca_element013]
  conduct = 2
  density = 1
  expand = 3
  formula = G4_M3_WAX
  name = G4_M3_WAX
  specific = 4
FEATURE [App::DocumentObjectGroupPython] Mg_element005  label="Mg_element : 1"  # scripted group (container) (typed FeaturePython)
  n = 1
  ref = Mg_element
FEATURE [App::DocumentObjectGroupPython] C_element058  label="C_element : 031"  # scripted group (container) (typed FeaturePython)
  n = 1
  ref = C_element
FEATURE [App::DocumentObjectGroupPython] O_element059  label="O_element : 030"  # scripted group (container) (typed FeaturePython)
  n = 3
  ref = O_element
FEATURE [App::DocumentObjectGroupPython] G4_MAGNESIUM_CARBONATE  # scripted group (container) (typed FeaturePython)
  Dunit = g/cm3
  Dvalue = 2.958
  Group = -> [Mg_element005,C_element058,O_element059]
  conduct = 2
  density = 1
  expand = 3
  formula = G4_MAGNESIUM_CARBONATE
  name = G4_MAGNESIUM_CARBONATE
  specific = 4
FEATURE [App::DocumentObjectGroupPython] Mg_element006  label="Mg_element : 002"  # scripted group (container) (typed FeaturePython)
  n = 1
  ref = Mg_element
FEATURE [App::DocumentObjectGroupPython] F_element013  label="F_element : 005"  # scripted group (container) (typed FeaturePython)
  n = 2
  ref = F_element
FEATURE [App::DocumentObjectGroupPython] G4_MAGNESIUM_FLUORIDE  # scripted group (container) (typed FeaturePython)
  Dunit = g/cm3
  Dvalue = 3
  Group = -> [Mg_element006,F_element013]
  conduct = 2
  density = 1
  expand = 3
  formula = G4_MAGNESIUM_FLUORIDE
  name = G4_MAGNESIUM_FLUORIDE
  specific = 4
FEATURE [App::DocumentObjectGroupPython] Mg_element007  label="Mg_element : 003"  # scripted group (container) (typed FeaturePython)
  n = 1
  ref = Mg_element
FEATURE [App::DocumentObjectGroupPython] O_element060  label="O_element : 031"  # scripted group (container) (typed FeaturePython)
  n = 1
  ref = O_element
FEATURE [App::DocumentObjectGroupPython] G4_MAGNESIUM_OXIDE  # scripted group (container) (typed FeaturePython)
  Dunit = g/cm3
  Dvalue = 3.58
  Group = -> [Mg_element007,O_element060]
  conduct = 2
  density = 1
  expand = 3
  formula = G4_MAGNESIUM_OXIDE
  name = G4_MAGNESIUM_OXIDE
  specific = 4
FEATURE [App::DocumentObjectGroupPython] Mg_element008  label="Mg_element : 004"  # scripted group (container) (typed FeaturePython)
  n = 1
  ref = Mg_element
FEATURE [App::DocumentObjectGroupPython] B_element006  label="B_element : 006"  # scripted group (container) (typed FeaturePython)
  n = 4
  ref = B_element
FEATURE [App::DocumentObjectGroupPython] O_element061  label="O_element : 032"  # scripted group (container) (typed FeaturePython)
  n = 7
  ref = O_element
FEATURE [App::DocumentObjectGroupPython] G4_MAGNESIUM_TETRABORATE  # scripted group (container) (typed FeaturePython)
  Dunit = g/cm3
  Dvalue = 2.53
  Group = -> [Mg_element008,B_element006,O_element061]
  conduct = 2
  density = 1
  expand = 3
  formula = G4_MAGNESIUM_TETRABORATE
  name = G4_MAGNESIUM_TETRABORATE
  specific = 4
FEATURE [App::DocumentObjectGroupPython] Hg_element001  label="Hg_element : 1"  # scripted group (container) (typed FeaturePython)
  n = 1
  ref = Hg_element
FEATURE [App::DocumentObjectGroupPython] I_element004  label="I_element : 2"  # scripted group (container) (typed FeaturePython)
  n = 2
  ref = I_element
FEATURE [App::DocumentObjectGroupPython] G4_MERCURIC_IODIDE  # scripted group (container) (typed FeaturePython)
  Dunit = g/cm3
  Dvalue = 6.36
  Group = -> [Hg_element001,I_element004]
  conduct = 2
  density = 1
  expand = 3
  formula = G4_MERCURIC_IODIDE
  name = G4_MERCURIC_IODIDE
  specific = 4
FEATURE [App::DocumentObjectGroupPython] C_element059  label="C_element : 032"  # scripted group (container) (typed FeaturePython)
  n = 1
  ref = C_element
FEATURE [App::DocumentObjectGroupPython] H_element053  label="H_element : 028"  # scripted group (container) (typed FeaturePython)
  n = 4
  ref = H_element
FEATURE [App::DocumentObjectGroupPython] G4_METHANE  # scripted group (container) (typed FeaturePython)
  Dunit = g/cm3
  Dvalue = 0.000667151
  Group = -> [C_element059,H_element053]
  conduct = 2
  density = 1
  expand = 3
  formula = G4_METHANE
  name = G4_METHANE
  specific = 4
FEATURE [App::DocumentObjectGroupPython] C_element060  label="C_element : 033"  # scripted group (container) (typed FeaturePython)
  n = 1
  ref = C_element
FEATURE [App::DocumentObjectGroupPython] H_element054  label="H_element : 029"  # scripted group (container) (typed FeaturePython)
  n = 4
  ref = H_element
FEATURE [App::DocumentObjectGroupPython] O_element062  label="O_element : 033"  # scripted group (container) (typed FeaturePython)
  n = 1
  ref = O_element
FEATURE [App::DocumentObjectGroupPython] G4_METHANOL  # scripted group (container) (typed FeaturePython)
  Dunit = g/cm3
  Dvalue = 0.7914
  Group = -> [C_element060,H_element054,O_element062]
  conduct = 2
  density = 1
  expand = 3
  formula = G4_METHANOL
  name = G4_METHANOL
  specific = 4
FEATURE [App::DocumentObjectGroupPython] H_element055  label="H_element : 0.134"  # scripted group (container) (typed FeaturePython)
  n = 0.13404
FEATURE [App::DocumentObjectGroupPython] C_element061  label="C_element : 0.778"  # scripted group (container) (typed FeaturePython)
  n = 0.77796
FEATURE [App::DocumentObjectGroupPython] O_element063  label="O_element : 0.035"  # scripted group (container) (typed FeaturePython)
  n = 0.03502
FEATURE [App::DocumentObjectGroupPython] Mg_element009  label="Mg_element : 0.039"  # scripted group (container) (typed FeaturePython)
  n = 0.038594
FEATURE [App::DocumentObjectGroupPython] Ti_element002  label="Ti_element : 0.014"  # scripted group (container) (typed FeaturePython)
  n = 0.014386
FEATURE [App::DocumentObjectGroupPython] G4_MIX_D_WAX  # scripted group (container) (typed FeaturePython)
  Dunit = g/cm3
  Dvalue = 0.99
  Group = -> [H_element055,C_element061,O_element063,Mg_element009,Ti_element002]
  conduct = 2
  density = 1
  expand = 3
  formula = G4_MIX_D_WAX
  name = G4_MIX_D_WAX
  specific = 4
FEATURE [App::DocumentObjectGroupPython] H_element056  label="H_element : 0.135"  # scripted group (container) (typed FeaturePython)
  n = 0.081192
FEATURE [App::DocumentObjectGroupPython] C_element062  label="C_element : 0.583"  # scripted group (container) (typed FeaturePython)
  n = 0.583442
FEATURE [App::DocumentObjectGroupPython] N_element024  label="N_element : 0.018"  # scripted group (container) (typed FeaturePython)
  n = 0.017798
FEATURE [App::DocumentObjectGroupPython] O_element064  label="O_element : 0.186"  # scripted group (container) (typed FeaturePython)
  n = 0.186381
FEATURE [App::DocumentObjectGroupPython] Mg_element010  label="Mg_element : 0.130"  # scripted group (container) (typed FeaturePython)
  n = 0.130287
FEATURE [App::DocumentObjectGroupPython] Cl_element015  label="Cl_element : 0.588"  # scripted group (container) (typed FeaturePython)
  n = 0.0009
FEATURE [App::DocumentObjectGroupPython] G4_MS20_TISSUE  # scripted group (container) (typed FeaturePython)
  Dunit = g/cm3
  Dvalue = 1
  Group = -> [H_element056,C_element062,N_element024,O_element064,Mg_element010,Cl_element015]
  conduct = 2
  density = 1
  expand = 3
  formula = G4_MS20_TISSUE
  name = G4_MS20_TISSUE
  specific = 4
FEATURE [App::DocumentObjectGroupPython] H_element057  label="H_element : 0.136"  # scripted group (container) (typed FeaturePython)
  n = 0.102
FEATURE [App::DocumentObjectGroupPython] C_element063  label="C_element : 0.143"  # scripted group (container) (typed FeaturePython)
  n = 0.143
FEATURE [App::DocumentObjectGroupPython] N_element025  label="N_element : 0.034"  # scripted group (container) (typed FeaturePython)
  n = 0.034
FEATURE [App::DocumentObjectGroupPython] O_element065  label="O_element : 0.710"  # scripted group (container) (typed FeaturePython)
  n = 0.71
FEATURE [App::DocumentObjectGroupPython] Na_element011  label="Na_element : 0.098"  # scripted group (container) (typed FeaturePython)
  n = 0.001
FEATURE [App::DocumentObjectGroupPython] P_element007  label="P_element : 0.002"  # scripted group (container) (typed FeaturePython)
  n = 0.002
FEATURE [App::DocumentObjectGroupPython] S_element017  label="S_element : 0.018"  # scripted group (container) (typed FeaturePython)
  n = 0.003
FEATURE [App::DocumentObjectGroupPython] Cl_element016  label="Cl_element : 0.589"  # scripted group (container) (typed FeaturePython)
  n = 0.001
FEATURE [App::DocumentObjectGroupPython] K_element006  label="K_element : 0.004"  # scripted group (container) (typed FeaturePython)
  n = 0.004
FEATURE [App::DocumentObjectGroupPython] G4_MUSCLE_SKELETAL_ICRP  # scripted group (container) (typed FeaturePython)
  Dunit = g/cm3
  Dvalue = 1.05
  Group = -> [H_element057,C_element063,N_element025,O_element065,Na_element011,P_element007,S_element017,Cl_element016,K_element006]
  conduct = 2
  density = 1
  expand = 3
  formula = G4_MUSCLE_SKELETAL_ICRP
  name = G4_MUSCLE_SKELETAL_ICRP
  specific = 4
FEATURE [App::DocumentObjectGroupPython] H_element058  label="H_element : 0.137"  # scripted group (container) (typed FeaturePython)
  n = 0.102102
FEATURE [App::DocumentObjectGroupPython] C_element064  label="C_element : 0.123"  # scripted group (container) (typed FeaturePython)
  n = 0.123123
FEATURE [App::DocumentObjectGroupPython] N_element026  label="N_element : 0.756"  # scripted group (container) (typed FeaturePython)
  n = 0.035035
FEATURE [App::DocumentObjectGroupPython] O_element066  label="O_element : 0.730"  # scripted group (container) (typed FeaturePython)
  n = 0.72973
FEATURE [App::DocumentObjectGroupPython] Na_element012  label="Na_element : 0.099"  # scripted group (container) (typed FeaturePython)
  n = 0.001001
FEATURE [App::DocumentObjectGroupPython] P_element008  label="P_element : 0.106"  # scripted group (container) (typed FeaturePython)
  n = 0.002002
FEATURE [App::DocumentObjectGroupPython] S_element018  label="S_element : 0.019"  # scripted group (container) (typed FeaturePython)
  n = 0.004004
FEATURE [App::DocumentObjectGroupPython] K_element007  label="K_element : 0.016"  # scripted group (container) (typed FeaturePython)
  n = 0.003003
FEATURE [App::DocumentObjectGroupPython] G4_MUSCLE_STRIATED_ICRU  # scripted group (container) (typed FeaturePython)
  Dunit = g/cm3
  Dvalue = 1.04
  Group = -> [H_element058,C_element064,N_element026,O_element066,Na_element012,P_element008,S_element018,K_element007]
  conduct = 2
  density = 1
  expand = 3
  formula = G4_MUSCLE_STRIATED_ICRU
  name = G4_MUSCLE_STRIATED_ICRU
  specific = 4
FEATURE [App::DocumentObjectGroupPython] H_element059  label="H_element : 0.098"  # scripted group (container) (typed FeaturePython)
  n = 0.0982341
FEATURE [App::DocumentObjectGroupPython] C_element065  label="C_element : 0.156"  # scripted group (container) (typed FeaturePython)
  n = 0.156214
FEATURE [App::DocumentObjectGroupPython] N_element027  label="N_element : 0.757"  # scripted group (container) (typed FeaturePython)
  n = 0.035451
FEATURE [App::DocumentObjectGroupPython] O_element067  label="O_element : 0.880"  # scripted group (container) (typed FeaturePython)
  n = 0.710101
FEATURE [App::DocumentObjectGroupPython] G4_MUSCLE_WITH_SUCROSE  # scripted group (container) (typed FeaturePython)
  Dunit = g/cm3
  Dvalue = 1.11
  Group = -> [H_element059,C_element065,N_element027,O_element067]
  conduct = 2
  density = 1
  expand = 3
  formula = G4_MUSCLE_WITH_SUCROSE
  name = G4_MUSCLE_WITH_SUCROSE
  specific = 4
FEATURE [App::DocumentObjectGroupPython] H_element060  label="H_element : 0.138"  # scripted group (container) (typed FeaturePython)
  n = 0.101969
FEATURE [App::DocumentObjectGroupPython] C_element066  label="C_element : 0.120"  # scripted group (container) (typed FeaturePython)
  n = 0.120058
FEATURE [App::DocumentObjectGroupPython] N_element028  label="N_element : 0.758"  # scripted group (container) (typed FeaturePython)
  n = 0.035451
FEATURE [App::DocumentObjectGroupPython] O_element068  label="O_element : 0.743"  # scripted group (container) (typed FeaturePython)
  n = 0.742522
FEATURE [App::DocumentObjectGroupPython] G4_MUSCLE_WITHOUT_SUCROSE  # scripted group (container) (typed FeaturePython)
  Dunit = g/cm3
  Dvalue = 1.07
  Group = -> [H_element060,C_element066,N_element028,O_element068]
  conduct = 2
  density = 1
  expand = 3
  formula = G4_MUSCLE_WITHOUT_SUCROSE
  name = G4_MUSCLE_WITHOUT_SUCROSE
  specific = 4
FEATURE [App::DocumentObjectGroupPython] C_element067  label="C_element : 10"  # scripted group (container) (typed FeaturePython)
  n = 10
  ref = C_element
FEATURE [App::DocumentObjectGroupPython] H_element061  label="H_element : 030"  # scripted group (container) (typed FeaturePython)
  n = 8
  ref = H_element
FEATURE [App::DocumentObjectGroupPython] G4_NAPHTHALENE  # scripted group (container) (typed FeaturePython)
  Dunit = g/cm3
  Dvalue = 1.145
  Group = -> [C_element067,H_element061]
  conduct = 2
  density = 1
  expand = 3
  formula = G4_NAPHTHALENE
  name = G4_NAPHTHALENE
  specific = 4
FEATURE [App::DocumentObjectGroupPython] C_element068  label="C_element : 034"  # scripted group (container) (typed FeaturePython)
  n = 6
  ref = C_element
FEATURE [App::DocumentObjectGroupPython] H_element062  label="H_element : 031"  # scripted group (container) (typed FeaturePython)
  n = 5
  ref = H_element
FEATURE [App::DocumentObjectGroupPython] N_element029  label="N_element : 012"  # scripted group (container) (typed FeaturePython)
  n = 1
  ref = N_element
FEATURE [App::DocumentObjectGroupPython] O_element069  label="O_element : 034"  # scripted group (container) (typed FeaturePython)
  n = 2
  ref = O_element
FEATURE [App::DocumentObjectGroupPython] G4_NITROBENZENE  # scripted group (container) (typed FeaturePython)
  Dunit = g/cm3
  Dvalue = 1.19867
  Group = -> [C_element068,H_element062,N_element029,O_element069]
  conduct = 2
  density = 1
  expand = 3
  formula = G4_NITROBENZENE
  name = G4_NITROBENZENE
  specific = 4
FEATURE [App::DocumentObjectGroupPython] N_element030  label="N_element : 013"  # scripted group (container) (typed FeaturePython)
  n = 2
  ref = N_element
FEATURE [App::DocumentObjectGroupPython] O_element070  label="O_element : 035"  # scripted group (container) (typed FeaturePython)
  n = 1
  ref = O_element
FEATURE [App::DocumentObjectGroupPython] G4_NITROUS_OXIDE  # scripted group (container) (typed FeaturePython)
  Dunit = g/cm3
  Dvalue = 0.00183094
  Group = -> [N_element030,O_element070]
  conduct = 2
  density = 1
  expand = 3
  formula = G4_NITROUS_OXIDE
  name = G4_NITROUS_OXIDE
  specific = 4
FEATURE [App::DocumentObjectGroupPython] H_element063  label="H_element : 0.104"  # scripted group (container) (typed FeaturePython)
  n = 0.103509
FEATURE [App::DocumentObjectGroupPython] C_element069  label="C_element : 0.648"  # scripted group (container) (typed FeaturePython)
  n = 0.648416
FEATURE [App::DocumentObjectGroupPython] N_element031  label="N_element : 0.100"  # scripted group (container) (typed FeaturePython)
  n = 0.0995361
FEATURE [App::DocumentObjectGroupPython] O_element071  label="O_element : 0.149"  # scripted group (container) (typed FeaturePython)
  n = 0.148539
FEATURE [App::DocumentObjectGroupPython] G4_NYLON_8062  label="G4_NYLON-8062"  # scripted group (container) (typed FeaturePython)
  Dunit = g/cm3
  Dvalue = 1.08
  Group = -> [H_element063,C_element069,N_element031,O_element071]
  conduct = 2
  density = 1
  expand = 3
  formula = G4_NYLON-8062
  name = G4_NYLON-8062
  specific = 4
FEATURE [App::DocumentObjectGroupPython] C_element070  label="C_element : 035"  # scripted group (container) (typed FeaturePython)
  n = 6
  ref = C_element
FEATURE [App::DocumentObjectGroupPython] H_element064  label="H_element : 11"  # scripted group (container) (typed FeaturePython)
  n = 11
  ref = H_element
FEATURE [App::DocumentObjectGroupPython] N_element032  label="N_element : 014"  # scripted group (container) (typed FeaturePython)
  n = 1
  ref = N_element
FEATURE [App::DocumentObjectGroupPython] O_element072  label="O_element : 036"  # scripted group (container) (typed FeaturePython)
  n = 1
  ref = O_element
FEATURE [App::DocumentObjectGroupPython] G4_NYLON_6_6  label="G4_NYLON-6-6"  # scripted group (container) (typed FeaturePython)
  Dunit = g/cm3
  Dvalue = 1.14
  Group = -> [C_element070,H_element064,N_element032,O_element072]
  conduct = 2
  density = 1
  expand = 3
  formula = G4_NYLON-6-6
  name = G4_NYLON-6-6
  specific = 4
FEATURE [App::DocumentObjectGroupPython] H_element065  label="H_element : 0.139"  # scripted group (container) (typed FeaturePython)
  n = 0.107062
FEATURE [App::DocumentObjectGroupPython] C_element071  label="C_element : 0.680"  # scripted group (container) (typed FeaturePython)
  n = 0.680449
FEATURE [App::DocumentObjectGroupPython] N_element033  label="N_element : 0.099"  # scripted group (container) (typed FeaturePython)
  n = 0.099189
FEATURE [App::DocumentObjectGroupPython] O_element073  label="O_element : 0.113"  # scripted group (container) (typed FeaturePython)
  n = 0.1133
FEATURE [App::DocumentObjectGroupPython] G4_NYLON_6_10  label="G4_NYLON-6-10"  # scripted group (container) (typed FeaturePython)
  Dunit = g/cm3
  Dvalue = 1.14
  Group = -> [H_element065,C_element071,N_element033,O_element073]
  conduct = 2
  density = 1
  expand = 3
  formula = G4_NYLON-6-10
  name = G4_NYLON-6-10
  specific = 4
FEATURE [App::DocumentObjectGroupPython] H_element066  label="H_element : 0.140"  # scripted group (container) (typed FeaturePython)
  n = 0.115476
FEATURE [App::DocumentObjectGroupPython] C_element072  label="C_element : 0.721"  # scripted group (container) (typed FeaturePython)
  n = 0.720818
FEATURE [App::DocumentObjectGroupPython] N_element034  label="N_element : 0.076"  # scripted group (container) (typed FeaturePython)
  n = 0.0764169
FEATURE [App::DocumentObjectGroupPython] O_element074  label="O_element : 0.087"  # scripted group (container) (typed FeaturePython)
  n = 0.0872889
FEATURE [App::DocumentObjectGroupPython] G4_NYLON_11_RILSAN  label="G4_NYLON-11_RILSAN"  # scripted group (container) (typed FeaturePython)
  Dunit = g/cm3
  Dvalue = 1.425
  Group = -> [H_element066,C_element072,N_element034,O_element074]
  conduct = 2
  density = 1
  expand = 3
  formula = G4_NYLON-11_RILSAN
  name = G4_NYLON-11_RILSAN
  specific = 4
FEATURE [App::DocumentObjectGroupPython] C_element073  label="C_element : 8"  # scripted group (container) (typed FeaturePython)
  n = 8
  ref = C_element
FEATURE [App::DocumentObjectGroupPython] H_element067  label="H_element : 18"  # scripted group (container) (typed FeaturePython)
  n = 18
  ref = H_element
FEATURE [App::DocumentObjectGroupPython] G4_OCTANE  # scripted group (container) (typed FeaturePython)
  Dunit = g/cm3
  Dvalue = 0.7026
  Group = -> [C_element073,H_element067]
  conduct = 2
  density = 1
  expand = 3
  formula = G4_OCTANE
  name = G4_OCTANE
  specific = 4
FEATURE [App::DocumentObjectGroupPython] C_element074  label="C_element : 25"  # scripted group (container) (typed FeaturePython)
  n = 25
  ref = C_element
FEATURE [App::DocumentObjectGroupPython] H_element068  label="H_element : 52"  # scripted group (container) (typed FeaturePython)
  n = 52
  ref = H_element
FEATURE [App::DocumentObjectGroupPython] G4_PARAFFIN  # scripted group (container) (typed FeaturePython)
  Dunit = g/cm3
  Dvalue = 0.93
  Group = -> [C_element074,H_element068]
  conduct = 2
  density = 1
  expand = 3
  formula = G4_PARAFFIN
  name = G4_PARAFFIN
  specific = 4
FEATURE [App::DocumentObjectGroupPython] C_element075  label="C_element : 036"  # scripted group (container) (typed FeaturePython)
  n = 5
  ref = C_element
FEATURE [App::DocumentObjectGroupPython] H_element069  label="H_element : 032"  # scripted group (container) (typed FeaturePython)
  n = 12
  ref = H_element
FEATURE [App::DocumentObjectGroupPython] G4_N_PENTANE  label="G4_N-PENTANE"  # scripted group (container) (typed FeaturePython)
  Dunit = g/cm3
  Dvalue = 0.6262
  Group = -> [C_element075,H_element069]
  conduct = 2
  density = 1
  expand = 3
  formula = G4_N-PENTANE
  name = G4_N-PENTANE
  specific = 4
FEATURE [App::DocumentObjectGroupPython] H_element070  label="H_element : 0.014"  # scripted group (container) (typed FeaturePython)
  n = 0.0141
FEATURE [App::DocumentObjectGroupPython] C_element076  label="C_element : 0.072"  # scripted group (container) (typed FeaturePython)
  n = 0.072261
FEATURE [App::DocumentObjectGroupPython] N_element035  label="N_element : 0.019"  # scripted group (container) (typed FeaturePython)
  n = 0.01932
FEATURE [App::DocumentObjectGroupPython] O_element075  label="O_element : 0.066"  # scripted group (container) (typed FeaturePython)
  n = 0.066101
FEATURE [App::DocumentObjectGroupPython] S_element019  label="S_element : 0.020"  # scripted group (container) (typed FeaturePython)
  n = 0.00189
FEATURE [App::DocumentObjectGroupPython] Br_element004  label="Br_element : 0.349"  # scripted group (container) (typed FeaturePython)
  n = 0.349103
FEATURE [App::DocumentObjectGroupPython] Ag_element001  label="Ag_element : 0.474"  # scripted group (container) (typed FeaturePython)
  n = 0.474105
FEATURE [App::DocumentObjectGroupPython] I_element005  label="I_element : 0.003"  # scripted group (container) (typed FeaturePython)
  n = 0.00312
FEATURE [App::DocumentObjectGroupPython] G4_PHOTO_EMULSION  # scripted group (container) (typed FeaturePython)
  Dunit = g/cm3
  Dvalue = 3.815
  Group = -> [H_element070,C_element076,N_element035,O_element075,S_element019,Br_element004,Ag_element001,I_element005]
  conduct = 2
  density = 1
  expand = 3
  formula = G4_PHOTO_EMULSION
  name = G4_PHOTO_EMULSION
  specific = 4
FEATURE [App::DocumentObjectGroupPython] C_element077  label="C_element : 9"  # scripted group (container) (typed FeaturePython)
  n = 9
  ref = C_element
FEATURE [App::DocumentObjectGroupPython] H_element071  label="H_element : 033"  # scripted group (container) (typed FeaturePython)
  n = 10
  ref = H_element
FEATURE [App::DocumentObjectGroupPython] G4_PLASTIC_SC_VINYLTOLUENE  # scripted group (container) (typed FeaturePython)
  Dunit = g/cm3
  Dvalue = 1.032
  Group = -> [C_element077,H_element071]
  conduct = 2
  density = 1
  expand = 3
  formula = G4_PLASTIC_SC_VINYLTOLUENE
  name = G4_PLASTIC_SC_VINYLTOLUENE
  specific = 4
FEATURE [App::DocumentObjectGroupPython] Pu_element001  label="Pu_element : 1"  # scripted group (container) (typed FeaturePython)
  n = 1
  ref = Pu_element
FEATURE [App::DocumentObjectGroupPython] O_element076  label="O_element : 037"  # scripted group (container) (typed FeaturePython)
  n = 2
  ref = O_element
FEATURE [App::DocumentObjectGroupPython] G4_PLUTONIUM_DIOXIDE  # scripted group (container) (typed FeaturePython)
  Dunit = g/cm3
  Dvalue = 11.46
  Group = -> [Pu_element001,O_element076]
  conduct = 2
  density = 1
  expand = 3
  formula = G4_PLUTONIUM_DIOXIDE
  name = G4_PLUTONIUM_DIOXIDE
  specific = 4
FEATURE [App::DocumentObjectGroupPython] C_element078  label="C_element : 037"  # scripted group (container) (typed FeaturePython)
  n = 3
  ref = C_element
FEATURE [App::DocumentObjectGroupPython] H_element072  label="H_element : 034"  # scripted group (container) (typed FeaturePython)
  n = 3
  ref = H_element
FEATURE [App::DocumentObjectGroupPython] N_element036  label="N_element : 015"  # scripted group (container) (typed FeaturePython)
  n = 1
  ref = N_element
FEATURE [App::DocumentObjectGroupPython] G4_POLYACRYLONITRILE  # scripted group (container) (typed FeaturePython)
  Dunit = g/cm3
  Dvalue = 1.17
  Group = -> [C_element078,H_element072,N_element036]
  conduct = 2
  density = 1
  expand = 3
  formula = G4_POLYACRYLONITRILE
  name = G4_POLYACRYLONITRILE
  specific = 4
FEATURE [App::DocumentObjectGroupPython] C_element079  label="C_element : 16"  # scripted group (container) (typed FeaturePython)
  n = 16
  ref = C_element
FEATURE [App::DocumentObjectGroupPython] H_element073  label="H_element : 035"  # scripted group (container) (typed FeaturePython)
  n = 14
  ref = H_element
FEATURE [App::DocumentObjectGroupPython] O_element077  label="O_element : 038"  # scripted group (container) (typed FeaturePython)
  n = 3
  ref = O_element
FEATURE [App::DocumentObjectGroupPython] G4_POLYCARBONATE  # scripted group (container) (typed FeaturePython)
  Dunit = g/cm3
  Dvalue = 1.2
  Group = -> [C_element079,H_element073,O_element077]
  conduct = 2
  density = 1
  expand = 3
  formula = G4_POLYCARBONATE
  name = G4_POLYCARBONATE
  specific = 4
FEATURE [App::DocumentObjectGroupPython] C_element080  label="C_element : 038"  # scripted group (container) (typed FeaturePython)
  n = 8
  ref = C_element
FEATURE [App::DocumentObjectGroupPython] H_element074  label="H_element : 036"  # scripted group (container) (typed FeaturePython)
  n = 7
  ref = H_element
FEATURE [App::DocumentObjectGroupPython] Cl_element017  label="Cl_element : 007"  # scripted group (container) (typed FeaturePython)
  n = 1
  ref = Cl_element
FEATURE [App::DocumentObjectGroupPython] G4_POLYCHLOROSTYRENE  # scripted group (container) (typed FeaturePython)
  Dunit = g/cm3
  Dvalue = 1.3
  Group = -> [C_element080,H_element074,Cl_element017]
  conduct = 2
  density = 1
  expand = 3
  formula = G4_POLYCHLOROSTYRENE
  name = G4_POLYCHLOROSTYRENE
  specific = 4
FEATURE [App::DocumentObjectGroupPython] C_element081  label="C_element : 039"  # scripted group (container) (typed FeaturePython)
  n = 1
  ref = C_element
FEATURE [App::DocumentObjectGroupPython] H_element075  label="H_element : 037"  # scripted group (container) (typed FeaturePython)
  n = 2
  ref = H_element
FEATURE [App::DocumentObjectGroupPython] G4_POLYETHYLENE  # scripted group (container) (typed FeaturePython)
  Dunit = g/cm3
  Dvalue = 0.94
  Group = -> [C_element081,H_element075]
  conduct = 2
  density = 1
  expand = 3
  formula = G4_POLYETHYLENE
  name = G4_POLYETHYLENE
  specific = 4
FEATURE [App::DocumentObjectGroupPython] C_element082  label="C_element : 040"  # scripted group (container) (typed FeaturePython)
  n = 10
  ref = C_element
FEATURE [App::DocumentObjectGroupPython] H_element076  label="H_element : 038"  # scripted group (container) (typed FeaturePython)
  n = 8
  ref = H_element
FEATURE [App::DocumentObjectGroupPython] O_element078  label="O_element : 039"  # scripted group (container) (typed FeaturePython)
  n = 4
  ref = O_element
FEATURE [App::DocumentObjectGroupPython] G4_MYLAR  # scripted group (container) (typed FeaturePython)
  Dunit = g/cm3
  Dvalue = 1.4
  Group = -> [C_element082,H_element076,O_element078]
  conduct = 2
  density = 1
  expand = 3
  formula = G4_MYLAR
  name = G4_MYLAR
  specific = 4
FEATURE [App::DocumentObjectGroupPython] C_element083  label="C_element : 041"  # scripted group (container) (typed FeaturePython)
  n = 5
  ref = C_element
FEATURE [App::DocumentObjectGroupPython] H_element077  label="H_element : 039"  # scripted group (container) (typed FeaturePython)
  n = 8
  ref = H_element
FEATURE [App::DocumentObjectGroupPython] O_element079  label="O_element : 040"  # scripted group (container) (typed FeaturePython)
  n = 2
  ref = O_element
FEATURE [App::DocumentObjectGroupPython] G4_PLEXIGLASS  # scripted group (container) (typed FeaturePython)
  Dunit = g/cm3
  Dvalue = 1.19
  Group = -> [C_element083,H_element077,O_element079]
  conduct = 2
  density = 1
  expand = 3
  formula = G4_PLEXIGLASS
  name = G4_PLEXIGLASS
  specific = 4
FEATURE [App::DocumentObjectGroupPython] C_element084  label="C_element : 042"  # scripted group (container) (typed FeaturePython)
  n = 1
  ref = C_element
FEATURE [App::DocumentObjectGroupPython] H_element078  label="H_element : 040"  # scripted group (container) (typed FeaturePython)
  n = 2
  ref = H_element
FEATURE [App::DocumentObjectGroupPython] O_element080  label="O_element : 041"  # scripted group (container) (typed FeaturePython)
  n = 1
  ref = O_element
FEATURE [App::DocumentObjectGroupPython] G4_POLYOXYMETHYLENE  # scripted group (container) (typed FeaturePython)
  Dunit = g/cm3
  Dvalue = 1.425
  Group = -> [C_element084,H_element078,O_element080]
  conduct = 2
  density = 1
  expand = 3
  formula = G4_POLYOXYMETHYLENE
  name = G4_POLYOXYMETHYLENE
  specific = 4
FEATURE [App::DocumentObjectGroupPython] C_element085  label="C_element : 043"  # scripted group (container) (typed FeaturePython)
  n = 2
  ref = C_element
FEATURE [App::DocumentObjectGroupPython] H_element079  label="H_element : 041"  # scripted group (container) (typed FeaturePython)
  n = 4
  ref = H_element
FEATURE [App::DocumentObjectGroupPython] G4_POLYPROPYLENE  # scripted group (container) (typed FeaturePython)
  Dunit = g/cm3
  Dvalue = 0.9
  Group = -> [C_element085,H_element079]
  conduct = 2
  density = 1
  expand = 3
  formula = G4_POLYPROPYLENE
  name = G4_POLYPROPYLENE
  specific = 4
FEATURE [App::DocumentObjectGroupPython] C_element086  label="C_element : 044"  # scripted group (container) (typed FeaturePython)
  n = 8
  ref = C_element
FEATURE [App::DocumentObjectGroupPython] H_element080  label="H_element : 042"  # scripted group (container) (typed FeaturePython)
  n = 8
  ref = H_element
FEATURE [App::DocumentObjectGroupPython] G4_POLYSTYRENE  # scripted group (container) (typed FeaturePython)
  Dunit = g/cm3
  Dvalue = 1.06
  Group = -> [C_element086,H_element080]
  conduct = 2
  density = 1
  expand = 3
  formula = G4_POLYSTYRENE
  name = G4_POLYSTYRENE
  specific = 4
FEATURE [App::DocumentObjectGroupPython] C_element087  label="C_element : 045"  # scripted group (container) (typed FeaturePython)
  n = 2
  ref = C_element
FEATURE [App::DocumentObjectGroupPython] F_element014  label="F_element : 4"  # scripted group (container) (typed FeaturePython)
  n = 4
  ref = F_element
FEATURE [App::DocumentObjectGroupPython] G4_TEFLON  # scripted group (container) (typed FeaturePython)
  Dunit = g/cm3
  Dvalue = 2.2
  Group = -> [C_element087,F_element014]
  conduct = 2
  density = 1
  expand = 3
  formula = G4_TEFLON
  name = G4_TEFLON
  specific = 4
FEATURE [App::DocumentObjectGroupPython] C_element088  label="C_element : 046"  # scripted group (container) (typed FeaturePython)
  n = 2
  ref = C_element
FEATURE [App::DocumentObjectGroupPython] F_element015  label="F_element : 006"  # scripted group (container) (typed FeaturePython)
  n = 3
  ref = F_element
FEATURE [App::DocumentObjectGroupPython] Cl_element018  label="Cl_element : 008"  # scripted group (container) (typed FeaturePython)
  n = 1
  ref = Cl_element
FEATURE [App::DocumentObjectGroupPython] G4_POLYTRIFLUOROCHLOROETHYLENE  # scripted group (container) (typed FeaturePython)
  Dunit = g/cm3
  Dvalue = 2.1
  Group = -> [C_element088,F_element015,Cl_element018]
  conduct = 2
  density = 1
  expand = 3
  formula = G4_POLYTRIFLUOROCHLOROETHYLENE
  name = G4_POLYTRIFLUOROCHLOROETHYLENE
  specific = 4
FEATURE [App::DocumentObjectGroupPython] C_element089  label="C_element : 047"  # scripted group (container) (typed FeaturePython)
  n = 4
  ref = C_element
FEATURE [App::DocumentObjectGroupPython] H_element081  label="H_element : 043"  # scripted group (container) (typed FeaturePython)
  n = 6
  ref = H_element
FEATURE [App::DocumentObjectGroupPython] O_element081  label="O_element : 042"  # scripted group (container) (typed FeaturePython)
  n = 2
  ref = O_element
FEATURE [App::DocumentObjectGroupPython] G4_POLYVINYL_ACETATE  # scripted group (container) (typed FeaturePython)
  Dunit = g/cm3
  Dvalue = 1.19
  Group = -> [C_element089,H_element081,O_element081]
  conduct = 2
  density = 1
  expand = 3
  formula = G4_POLYVINYL_ACETATE
  name = G4_POLYVINYL_ACETATE
  specific = 4
FEATURE [App::DocumentObjectGroupPython] C_element090  label="C_element : 048"  # scripted group (container) (typed FeaturePython)
  n = 2
  ref = C_element
FEATURE [App::DocumentObjectGroupPython] H_element082  label="H_element : 044"  # scripted group (container) (typed FeaturePython)
  n = 4
  ref = H_element
FEATURE [App::DocumentObjectGroupPython] O_element082  label="O_element : 043"  # scripted group (container) (typed FeaturePython)
  n = 1
  ref = O_element
FEATURE [App::DocumentObjectGroupPython] G4_POLYVINYL_ALCOHOL  # scripted group (container) (typed FeaturePython)
  Dunit = g/cm3
  Dvalue = 1.3
  Group = -> [C_element090,H_element082,O_element082]
  conduct = 2
  density = 1
  expand = 3
  formula = G4_POLYVINYL_ALCOHOL
  name = G4_POLYVINYL_ALCOHOL
  specific = 4
FEATURE [App::DocumentObjectGroupPython] C_element091  label="C_element : 049"  # scripted group (container) (typed FeaturePython)
  n = 8
  ref = C_element
FEATURE [App::DocumentObjectGroupPython] H_element083  label="H_element : 045"  # scripted group (container) (typed FeaturePython)
  n = 14
  ref = H_element
FEATURE [App::DocumentObjectGroupPython] O_element083  label="O_element : 044"  # scripted group (container) (typed FeaturePython)
  n = 2
  ref = O_element
FEATURE [App::DocumentObjectGroupPython] G4_POLYVINYL_BUTYRAL  # scripted group (container) (typed FeaturePython)
  Dunit = g/cm3
  Dvalue = 1.12
  Group = -> [C_element091,H_element083,O_element083]
  conduct = 2
  density = 1
  expand = 3
  formula = G4_POLYVINYL_BUTYRAL
  name = G4_POLYVINYL_BUTYRAL
  specific = 4
FEATURE [App::DocumentObjectGroupPython] C_element092  label="C_element : 050"  # scripted group (container) (typed FeaturePython)
  n = 2
  ref = C_element
FEATURE [App::DocumentObjectGroupPython] H_element084  label="H_element : 046"  # scripted group (container) (typed FeaturePython)
  n = 3
  ref = H_element
FEATURE [App::DocumentObjectGroupPython] Cl_element019  label="Cl_element : 009"  # scripted group (container) (typed FeaturePython)
  n = 1
  ref = Cl_element
FEATURE [App::DocumentObjectGroupPython] G4_POLYVINYL_CHLORIDE  # scripted group (container) (typed FeaturePython)
  Dunit = g/cm3
  Dvalue = 1.3
  Group = -> [C_element092,H_element084,Cl_element019]
  conduct = 2
  density = 1
  expand = 3
  formula = G4_POLYVINYL_CHLORIDE
  name = G4_POLYVINYL_CHLORIDE
  specific = 4
FEATURE [App::DocumentObjectGroupPython] C_element093  label="C_element : 051"  # scripted group (container) (typed FeaturePython)
  n = 2
  ref = C_element
FEATURE [App::DocumentObjectGroupPython] H_element085  label="H_element : 047"  # scripted group (container) (typed FeaturePython)
  n = 2
  ref = H_element
FEATURE [App::DocumentObjectGroupPython] Cl_element020  label="Cl_element : 010"  # scripted group (container) (typed FeaturePython)
  n = 2
  ref = Cl_element
FEATURE [App::DocumentObjectGroupPython] G4_POLYVINYLIDENE_CHLORIDE  # scripted group (container) (typed FeaturePython)
  Dunit = g/cm3
  Dvalue = 1.7
  Group = -> [C_element093,H_element085,Cl_element020]
  conduct = 2
  density = 1
  expand = 3
  formula = G4_POLYVINYLIDENE_CHLORIDE
  name = G4_POLYVINYLIDENE_CHLORIDE
  specific = 4
FEATURE [App::DocumentObjectGroupPython] C_element094  label="C_element : 052"  # scripted group (container) (typed FeaturePython)
  n = 2
  ref = C_element
FEATURE [App::DocumentObjectGroupPython] H_element086  label="H_element : 048"  # scripted group (container) (typed FeaturePython)
  n = 2
  ref = H_element
FEATURE [App::DocumentObjectGroupPython] F_element016  label="F_element : 007"  # scripted group (container) (typed FeaturePython)
  n = 2
  ref = F_element
FEATURE [App::DocumentObjectGroupPython] G4_POLYVINYLIDENE_FLUORIDE  # scripted group (container) (typed FeaturePython)
  Dunit = g/cm3
  Dvalue = 1.76
  Group = -> [C_element094,H_element086,F_element016]
  conduct = 2
  density = 1
  expand = 3
  formula = G4_POLYVINYLIDENE_FLUORIDE
  name = G4_POLYVINYLIDENE_FLUORIDE
  specific = 4
FEATURE [App::DocumentObjectGroupPython] C_element095  label="C_element : 053"  # scripted group (container) (typed FeaturePython)
  n = 6
  ref = C_element
FEATURE [App::DocumentObjectGroupPython] H_element087  label="H_element : 9"  # scripted group (container) (typed FeaturePython)
  n = 9
  ref = H_element
FEATURE [App::DocumentObjectGroupPython] N_element037  label="N_element : 016"  # scripted group (container) (typed FeaturePython)
  n = 1
  ref = N_element
FEATURE [App::DocumentObjectGroupPython] O_element084  label="O_element : 045"  # scripted group (container) (typed FeaturePython)
  n = 1
  ref = O_element
FEATURE [App::DocumentObjectGroupPython] G4_POLYVINYL_PYRROLIDONE  # scripted group (container) (typed FeaturePython)
  Dunit = g/cm3
  Dvalue = 1.25
  Group = -> [C_element095,H_element087,N_element037,O_element084]
  conduct = 2
  density = 1
  expand = 3
  formula = G4_POLYVINYL_PYRROLIDONE
  name = G4_POLYVINYL_PYRROLIDONE
  specific = 4
FEATURE [App::DocumentObjectGroupPython] K_element008  label="K_element : 1"  # scripted group (container) (typed FeaturePython)
  n = 1
  ref = K_element
FEATURE [App::DocumentObjectGroupPython] I_element006  label="I_element : 003"  # scripted group (container) (typed FeaturePython)
  n = 1
  ref = I_element
FEATURE [App::DocumentObjectGroupPython] G4_POTASSIUM_IODIDE  # scripted group (container) (typed FeaturePython)
  Dunit = g/cm3
  Dvalue = 3.13
  Group = -> [K_element008,I_element006]
  conduct = 2
  density = 1
  expand = 3
  formula = G4_POTASSIUM_IODIDE
  name = G4_POTASSIUM_IODIDE
  specific = 4
FEATURE [App::DocumentObjectGroupPython] K_element009  label="K_element : 2"  # scripted group (container) (typed FeaturePython)
  n = 2
  ref = K_element
FEATURE [App::DocumentObjectGroupPython] O_element085  label="O_element : 046"  # scripted group (container) (typed FeaturePython)
  n = 1
  ref = O_element
FEATURE [App::DocumentObjectGroupPython] G4_POTASSIUM_OXIDE  # scripted group (container) (typed FeaturePython)
  Dunit = g/cm3
  Dvalue = 2.32
  Group = -> [K_element009,O_element085]
  conduct = 2
  density = 1
  expand = 3
  formula = G4_POTASSIUM_OXIDE
  name = G4_POTASSIUM_OXIDE
  specific = 4
FEATURE [App::DocumentObjectGroupPython] C_element096  label="C_element : 054"  # scripted group (container) (typed FeaturePython)
  n = 3
  ref = C_element
FEATURE [App::DocumentObjectGroupPython] H_element088  label="H_element : 049"  # scripted group (container) (typed FeaturePython)
  n = 8
  ref = H_element
FEATURE [App::DocumentObjectGroupPython] G4_PROPANE  # scripted group (container) (typed FeaturePython)
  Dunit = g/cm3
  Dvalue = 0.00187939
  Group = -> [C_element096,H_element088]
  conduct = 2
  density = 1
  expand = 3
  formula = G4_PROPANE
  name = G4_PROPANE
  specific = 4
FEATURE [App::DocumentObjectGroupPython] C_element097  label="C_element : 055"  # scripted group (container) (typed FeaturePython)
  n = 3
  ref = C_element
FEATURE [App::DocumentObjectGroupPython] H_element089  label="H_element : 050"  # scripted group (container) (typed FeaturePython)
  n = 8
  ref = H_element
FEATURE [App::DocumentObjectGroupPython] G4_lPROPANE  # scripted group (container) (typed FeaturePython)
  Dunit = g/cm3
  Dvalue = 0.43
  Group = -> [C_element097,H_element089]
  conduct = 2
  density = 1
  expand = 3
  formula = G4_lPROPANE
  name = G4_lPROPANE
  specific = 4
FEATURE [App::DocumentObjectGroupPython] C_element098  label="C_element : 056"  # scripted group (container) (typed FeaturePython)
  n = 3
  ref = C_element
FEATURE [App::DocumentObjectGroupPython] H_element090  label="H_element : 051"  # scripted group (container) (typed FeaturePython)
  n = 8
  ref = H_element
FEATURE [App::DocumentObjectGroupPython] O_element086  label="O_element : 047"  # scripted group (container) (typed FeaturePython)
  n = 1
  ref = O_element
FEATURE [App::DocumentObjectGroupPython] G4_N_PROPYL_ALCOHOL  label="G4_N-PROPYL_ALCOHOL"  # scripted group (container) (typed FeaturePython)
  Dunit = g/cm3
  Dvalue = 0.8035
  Group = -> [C_element098,H_element090,O_element086]
  conduct = 2
  density = 1
  expand = 3
  formula = G4_N-PROPYL_ALCOHOL
  name = G4_N-PROPYL_ALCOHOL
  specific = 4
FEATURE [App::DocumentObjectGroupPython] C_element099  label="C_element : 057"  # scripted group (container) (typed FeaturePython)
  n = 5
  ref = C_element
FEATURE [App::DocumentObjectGroupPython] H_element091  label="H_element : 052"  # scripted group (container) (typed FeaturePython)
  n = 5
  ref = H_element
FEATURE [App::DocumentObjectGroupPython] N_element038  label="N_element : 017"  # scripted group (container) (typed FeaturePython)
  n = 1
  ref = N_element
FEATURE [App::DocumentObjectGroupPython] G4_PYRIDINE  # scripted group (container) (typed FeaturePython)
  Dunit = g/cm3
  Dvalue = 0.9819
  Group = -> [C_element099,H_element091,N_element038]
  conduct = 2
  density = 1
  expand = 3
  formula = G4_PYRIDINE
  name = G4_PYRIDINE
  specific = 4
FEATURE [App::DocumentObjectGroupPython] H_element092  label="H_element : 0.144"  # scripted group (container) (typed FeaturePython)
  n = 0.143711
FEATURE [App::DocumentObjectGroupPython] C_element100  label="C_element : 0.856"  # scripted group (container) (typed FeaturePython)
  n = 0.856289
FEATURE [App::DocumentObjectGroupPython] G4_RUBBER_BUTYL  # scripted group (container) (typed FeaturePython)
  Dunit = g/cm3
  Dvalue = 0.92
  Group = -> [H_element092,C_element100]
  conduct = 2
  density = 1
  expand = 3
  formula = G4_RUBBER_BUTYL
  name = G4_RUBBER_BUTYL
  specific = 4
FEATURE [App::DocumentObjectGroupPython] H_element093  label="H_element : 0.118"  # scripted group (container) (typed FeaturePython)
  n = 0.118371
FEATURE [App::DocumentObjectGroupPython] C_element101  label="C_element : 0.882"  # scripted group (container) (typed FeaturePython)
  n = 0.881629
FEATURE [App::DocumentObjectGroupPython] G4_RUBBER_NATURAL  # scripted group (container) (typed FeaturePython)
  Dunit = g/cm3
  Dvalue = 0.92
  Group = -> [H_element093,C_element101]
  conduct = 2
  density = 1
  expand = 3
  formula = G4_RUBBER_NATURAL
  name = G4_RUBBER_NATURAL
  specific = 4
FEATURE [App::DocumentObjectGroupPython] H_element094  label="H_element : 0.145"  # scripted group (container) (typed FeaturePython)
  n = 0.05692
FEATURE [App::DocumentObjectGroupPython] C_element102  label="C_element : 0.543"  # scripted group (container) (typed FeaturePython)
  n = 0.542646
FEATURE [App::DocumentObjectGroupPython] Cl_element021  label="Cl_element : 0.400"  # scripted group (container) (typed FeaturePython)
  n = 0.400434
FEATURE [App::DocumentObjectGroupPython] G4_RUBBER_NEOPRENE  # scripted group (container) (typed FeaturePython)
  Dunit = g/cm3
  Dvalue = 1.23
  Group = -> [H_element094,C_element102,Cl_element021]
  conduct = 2
  density = 1
  expand = 3
  formula = G4_RUBBER_NEOPRENE
  name = G4_RUBBER_NEOPRENE
  specific = 4
FEATURE [App::DocumentObjectGroupPython] Si_element006  label="Si_element : 1"  # scripted group (container) (typed FeaturePython)
  n = 1
  ref = Si_element
FEATURE [App::DocumentObjectGroupPython] O_element087  label="O_element : 048"  # scripted group (container) (typed FeaturePython)
  n = 2
  ref = O_element
FEATURE [App::DocumentObjectGroupPython] G4_SILICON_DIOXIDE  # scripted group (container) (typed FeaturePython)
  Dunit = g/cm3
  Dvalue = 2.32
  Group = -> [Si_element006,O_element087]
  conduct = 2
  density = 1
  expand = 3
  formula = G4_SILICON_DIOXIDE
  name = G4_SILICON_DIOXIDE
  specific = 4
FEATURE [App::DocumentObjectGroupPython] Ag_element002  label="Ag_element : 1"  # scripted group (container) (typed FeaturePython)
  n = 1
  ref = Ag_element
FEATURE [App::DocumentObjectGroupPython] Br_element005  label="Br_element : 003"  # scripted group (container) (typed FeaturePython)
  n = 1
  ref = Br_element
FEATURE [App::DocumentObjectGroupPython] G4_SILVER_BROMIDE  # scripted group (container) (typed FeaturePython)
  Dunit = g/cm3
  Dvalue = 6.473
  Group = -> [Ag_element002,Br_element005]
  conduct = 2
  density = 1
  expand = 3
  formula = G4_SILVER_BROMIDE
  name = G4_SILVER_BROMIDE
  specific = 4
FEATURE [App::DocumentObjectGroupPython] Ag_element003  label="Ag_element : 002"  # scripted group (container) (typed FeaturePython)
  n = 1
  ref = Ag_element
FEATURE [App::DocumentObjectGroupPython] Cl_element022  label="Cl_element : 011"  # scripted group (container) (typed FeaturePython)
  n = 1
  ref = Cl_element
FEATURE [App::DocumentObjectGroupPython] G4_SILVER_CHLORIDE  # scripted group (container) (typed FeaturePython)
  Dunit = g/cm3
  Dvalue = 5.56
  Group = -> [Ag_element003,Cl_element022]
  conduct = 2
  density = 1
  expand = 3
  formula = G4_SILVER_CHLORIDE
  name = G4_SILVER_CHLORIDE
  specific = 4
FEATURE [App::DocumentObjectGroupPython] Br_element006  label="Br_element : 0.423"  # scripted group (container) (typed FeaturePython)
  n = 0.422895
FEATURE [App::DocumentObjectGroupPython] Ag_element004  label="Ag_element : 0.574"  # scripted group (container) (typed FeaturePython)
  n = 0.573748
FEATURE [App::DocumentObjectGroupPython] I_element007  label="I_element : 0.649"  # scripted group (container) (typed FeaturePython)
  n = 0.003357
FEATURE [App::DocumentObjectGroupPython] G4_SILVER_HALIDES  # scripted group (container) (typed FeaturePython)
  Dunit = g/cm3
  Dvalue = 6.47
  Group = -> [Br_element006,Ag_element004,I_element007]
  conduct = 2
  density = 1
  expand = 3
  formula = G4_SILVER_HALIDES
  name = G4_SILVER_HALIDES
  specific = 4
FEATURE [App::DocumentObjectGroupPython] Ag_element005  label="Ag_element : 003"  # scripted group (container) (typed FeaturePython)
  n = 1
  ref = Ag_element
FEATURE [App::DocumentObjectGroupPython] I_element008  label="I_element : 004"  # scripted group (container) (typed FeaturePython)
  n = 1
  ref = I_element
FEATURE [App::DocumentObjectGroupPython] G4_SILVER_IODIDE  # scripted group (container) (typed FeaturePython)
  Dunit = g/cm3
  Dvalue = 6.01
  Group = -> [Ag_element005,I_element008]
  conduct = 2
  density = 1
  expand = 3
  formula = G4_SILVER_IODIDE
  name = G4_SILVER_IODIDE
  specific = 4
FEATURE [App::DocumentObjectGroupPython] H_element095  label="H_element : 0.100"  # scripted group (container) (typed FeaturePython)
  n = 0.1
FEATURE [App::DocumentObjectGroupPython] C_element103  label="C_element : 0.204"  # scripted group (container) (typed FeaturePython)
  n = 0.204
FEATURE [App::DocumentObjectGroupPython] N_element039  label="N_element : 0.759"  # scripted group (container) (typed FeaturePython)
  n = 0.042
FEATURE [App::DocumentObjectGroupPython] O_element088  label="O_element : 0.645"  # scripted group (container) (typed FeaturePython)
  n = 0.645
FEATURE [App::DocumentObjectGroupPython] Na_element013  label="Na_element : 0.100"  # scripted group (container) (typed FeaturePython)
  n = 0.002
FEATURE [App::DocumentObjectGroupPython] P_element009  label="P_element : 0.107"  # scripted group (container) (typed FeaturePython)
  n = 0.001
FEATURE [App::DocumentObjectGroupPython] S_element020  label="S_element : 0.021"  # scripted group (container) (typed FeaturePython)
  n = 0.002
FEATURE [App::DocumentObjectGroupPython] Cl_element023  label="Cl_element : 0.590"  # scripted group (container) (typed FeaturePython)
  n = 0.003
FEATURE [App::DocumentObjectGroupPython] K_element010  label="K_element : 0.001"  # scripted group (container) (typed FeaturePython)
  n = 0.001
FEATURE [App::DocumentObjectGroupPython] G4_SKIN_ICRP  # scripted group (container) (typed FeaturePython)
  Dunit = g/cm3
  Dvalue = 1.09
  Group = -> [H_element095,C_element103,N_element039,O_element088,Na_element013,P_element009,S_element020,Cl_element023,K_element010]
  conduct = 2
  density = 1
  expand = 3
  formula = G4_SKIN_ICRP
  name = G4_SKIN_ICRP
  specific = 4
FEATURE [App::DocumentObjectGroupPython] Na_element014  label="Na_element : 2"  # scripted group (container) (typed FeaturePython)
  n = 2
  ref = Na_element
FEATURE [App::DocumentObjectGroupPython] C_element104  label="C_element : 058"  # scripted group (container) (typed FeaturePython)
  n = 1
  ref = C_element
FEATURE [App::DocumentObjectGroupPython] O_element089  label="O_element : 049"  # scripted group (container) (typed FeaturePython)
  n = 3
  ref = O_element
FEATURE [App::DocumentObjectGroupPython] G4_SODIUM_CARBONATE  # scripted group (container) (typed FeaturePython)
  Dunit = g/cm3
  Dvalue = 2.532
  Group = -> [Na_element014,C_element104,O_element089]
  conduct = 2
  density = 1
  expand = 3
  formula = G4_SODIUM_CARBONATE
  name = G4_SODIUM_CARBONATE
  specific = 4
FEATURE [App::DocumentObjectGroupPython] Na_element015  label="Na_element : 1"  # scripted group (container) (typed FeaturePython)
  n = 1
  ref = Na_element
FEATURE [App::DocumentObjectGroupPython] I_element009  label="I_element : 005"  # scripted group (container) (typed FeaturePython)
  n = 1
  ref = I_element
FEATURE [App::DocumentObjectGroupPython] G4_SODIUM_IODIDE  # scripted group (container) (typed FeaturePython)
  Dunit = g/cm3
  Dvalue = 3.667
  Group = -> [Na_element015,I_element009]
  conduct = 2
  density = 1
  expand = 3
  formula = G4_SODIUM_IODIDE
  name = G4_SODIUM_IODIDE
  specific = 4
FEATURE [App::DocumentObjectGroupPython] Na_element016  label="Na_element : 003"  # scripted group (container) (typed FeaturePython)
  n = 2
  ref = Na_element
FEATURE [App::DocumentObjectGroupPython] O_element090  label="O_element : 050"  # scripted group (container) (typed FeaturePython)
  n = 1
  ref = O_element
FEATURE [App::DocumentObjectGroupPython] G4_SODIUM_MONOXIDE  # scripted group (container) (typed FeaturePython)
  Dunit = g/cm3
  Dvalue = 2.27
  Group = -> [Na_element016,O_element090]
  conduct = 2
  density = 1
  expand = 3
  formula = G4_SODIUM_MONOXIDE
  name = G4_SODIUM_MONOXIDE
  specific = 4
FEATURE [App::DocumentObjectGroupPython] Na_element017  label="Na_element : 004"  # scripted group (container) (typed FeaturePython)
  n = 1
  ref = Na_element
FEATURE [App::DocumentObjectGroupPython] N_element040  label="N_element : 018"  # scripted group (container) (typed FeaturePython)
  n = 1
  ref = N_element
FEATURE [App::DocumentObjectGroupPython] O_element091  label="O_element : 051"  # scripted group (container) (typed FeaturePython)
  n = 3
  ref = O_element
FEATURE [App::DocumentObjectGroupPython] G4_SODIUM_NITRATE  # scripted group (container) (typed FeaturePython)
  Dunit = g/cm3
  Dvalue = 2.261
  Group = -> [Na_element017,N_element040,O_element091]
  conduct = 2
  density = 1
  expand = 3
  formula = G4_SODIUM_NITRATE
  name = G4_SODIUM_NITRATE
  specific = 4
FEATURE [App::DocumentObjectGroupPython] C_element105  label="C_element : 059"  # scripted group (container) (typed FeaturePython)
  n = 14
  ref = C_element
FEATURE [App::DocumentObjectGroupPython] H_element096  label="H_element : 053"  # scripted group (container) (typed FeaturePython)
  n = 12
  ref = H_element
FEATURE [App::DocumentObjectGroupPython] G4_STILBENE  # scripted group (container) (typed FeaturePython)
  Dunit = g/cm3
  Dvalue = 0.9707
  Group = -> [C_element105,H_element096]
  conduct = 2
  density = 1
  expand = 3
  formula = G4_STILBENE
  name = G4_STILBENE
  specific = 4
FEATURE [App::DocumentObjectGroupPython] C_element106  label="C_element : 12"  # scripted group (container) (typed FeaturePython)
  n = 12
  ref = C_element
FEATURE [App::DocumentObjectGroupPython] H_element097  label="H_element : 22"  # scripted group (container) (typed FeaturePython)
  n = 22
  ref = H_element
FEATURE [App::DocumentObjectGroupPython] O_element092  label="O_element : 11"  # scripted group (container) (typed FeaturePython)
  n = 11
  ref = O_element
FEATURE [App::DocumentObjectGroupPython] G4_SUCROSE  # scripted group (container) (typed FeaturePython)
  Dunit = g/cm3
  Dvalue = 1.5805
  Group = -> [C_element106,H_element097,O_element092]
  conduct = 2
  density = 1
  expand = 3
  formula = G4_SUCROSE
  name = G4_SUCROSE
  specific = 4
FEATURE [App::DocumentObjectGroupPython] C_element107  label="C_element : 18"  # scripted group (container) (typed FeaturePython)
  n = 18
  ref = C_element
FEATURE [App::DocumentObjectGroupPython] H_element098  label="H_element : 054"  # scripted group (container) (typed FeaturePython)
  n = 14
  ref = H_element
FEATURE [App::DocumentObjectGroupPython] G4_TERPHENYL  # scripted group (container) (typed FeaturePython)
  Dunit = g/cm3
  Dvalue = 1.24
  Group = -> [C_element107,H_element098]
  conduct = 2
  density = 1
  expand = 3
  formula = G4_TERPHENYL
  name = G4_TERPHENYL
  specific = 4
FEATURE [App::DocumentObjectGroupPython] H_element099  label="H_element : 0.146"  # scripted group (container) (typed FeaturePython)
  n = 0.106
FEATURE [App::DocumentObjectGroupPython] C_element108  label="C_element : 0.883"  # scripted group (container) (typed FeaturePython)
  n = 0.099
FEATURE [App::DocumentObjectGroupPython] N_element041  label="N_element : 0.020"  # scripted group (container) (typed FeaturePython)
  n = 0.02
FEATURE [App::DocumentObjectGroupPython] O_element093  label="O_element : 0.766"  # scripted group (container) (typed FeaturePython)
  n = 0.766
FEATURE [App::DocumentObjectGroupPython] Na_element018  label="Na_element : 0.101"  # scripted group (container) (typed FeaturePython)
  n = 0.002
FEATURE [App::DocumentObjectGroupPython] P_element010  label="P_element : 0.108"  # scripted group (container) (typed FeaturePython)
  n = 0.001
FEATURE [App::DocumentObjectGroupPython] S_element021  label="S_element : 0.022"  # scripted group (container) (typed FeaturePython)
  n = 0.002
FEATURE [App::DocumentObjectGroupPython] Cl_element024  label="Cl_element : 0.002"  # scripted group (container) (typed FeaturePython)
  n = 0.002
FEATURE [App::DocumentObjectGroupPython] K_element011  label="K_element : 0.017"  # scripted group (container) (typed FeaturePython)
  n = 0.002
FEATURE [App::DocumentObjectGroupPython] G4_TESTIS_ICRP  # scripted group (container) (typed FeaturePython)
  Dunit = g/cm3
  Dvalue = 1.04
  Group = -> [H_element099,C_element108,N_element041,O_element093,Na_element018,P_element010,S_element021,Cl_element024,K_element011]
  conduct = 2
  density = 1
  expand = 3
  formula = G4_TESTIS_ICRP
  name = G4_TESTIS_ICRP
  specific = 4
FEATURE [App::DocumentObjectGroupPython] C_element109  label="C_element : 060"  # scripted group (container) (typed FeaturePython)
  n = 2
  ref = C_element
FEATURE [App::DocumentObjectGroupPython] Cl_element025  label="Cl_element : 012"  # scripted group (container) (typed FeaturePython)
  n = 4
  ref = Cl_element
FEATURE [App::DocumentObjectGroupPython] G4_TETRACHLOROETHYLENE  # scripted group (container) (typed FeaturePython)
  Dunit = g/cm3
  Dvalue = 1.625
  Group = -> [C_element109,Cl_element025]
  conduct = 2
  density = 1
  expand = 3
  formula = G4_TETRACHLOROETHYLENE
  name = G4_TETRACHLOROETHYLENE
  specific = 4
FEATURE [App::DocumentObjectGroupPython] Tl_element001  label="Tl_element : 1"  # scripted group (container) (typed FeaturePython)
  n = 1
  ref = Tl_element
FEATURE [App::DocumentObjectGroupPython] Cl_element026  label="Cl_element : 013"  # scripted group (container) (typed FeaturePython)
  n = 1
  ref = Cl_element
FEATURE [App::DocumentObjectGroupPython] G4_THALLIUM_CHLORIDE  # scripted group (container) (typed FeaturePython)
  Dunit = g/cm3
  Dvalue = 7.004
  Group = -> [Tl_element001,Cl_element026]
  conduct = 2
  density = 1
  expand = 3
  formula = G4_THALLIUM_CHLORIDE
  name = G4_THALLIUM_CHLORIDE
  specific = 4
FEATURE [App::DocumentObjectGroupPython] H_element100  label="H_element : 0.147"  # scripted group (container) (typed FeaturePython)
  n = 0.105
FEATURE [App::DocumentObjectGroupPython] C_element110  label="C_element : 0.256"  # scripted group (container) (typed FeaturePython)
  n = 0.256
FEATURE [App::DocumentObjectGroupPython] N_element042  label="N_element : 0.760"  # scripted group (container) (typed FeaturePython)
  n = 0.027
FEATURE [App::DocumentObjectGroupPython] O_element094  label="O_element : 0.602"  # scripted group (container) (typed FeaturePython)
  n = 0.602
FEATURE [App::DocumentObjectGroupPython] Na_element019  label="Na_element : 0.102"  # scripted group (container) (typed FeaturePython)
  n = 0.001
FEATURE [App::DocumentObjectGroupPython] P_element011  label="P_element : 0.109"  # scripted group (container) (typed FeaturePython)
  n = 0.002
FEATURE [App::DocumentObjectGroupPython] S_element022  label="S_element : 0.023"  # scripted group (container) (typed FeaturePython)
  n = 0.003
FEATURE [App::DocumentObjectGroupPython] Cl_element027  label="Cl_element : 0.591"  # scripted group (container) (typed FeaturePython)
  n = 0.002
FEATURE [App::DocumentObjectGroupPython] K_element012  label="K_element : 0.018"  # scripted group (container) (typed FeaturePython)
  n = 0.002
FEATURE [App::DocumentObjectGroupPython] G4_TISSUE_SOFT_ICRP  # scripted group (container) (typed FeaturePython)
  Dunit = g/cm3
  Dvalue = 1.03
  Group = -> [H_element100,C_element110,N_element042,O_element094,Na_element019,P_element011,S_element022,Cl_element027,K_element012]
  conduct = 2
  density = 1
  expand = 3
  formula = G4_TISSUE_SOFT_ICRP
  name = G4_TISSUE_SOFT_ICRP
  specific = 4
FEATURE [App::DocumentObjectGroupPython] H_element101  label="H_element : 0.148"  # scripted group (container) (typed FeaturePython)
  n = 0.101
FEATURE [App::DocumentObjectGroupPython] C_element111  label="C_element : 0.111"  # scripted group (container) (typed FeaturePython)
  n = 0.111
FEATURE [App::DocumentObjectGroupPython] N_element043  label="N_element : 0.026"  # scripted group (container) (typed FeaturePython)
  n = 0.026
FEATURE [App::DocumentObjectGroupPython] O_element095  label="O_element : 0.762"  # scripted group (container) (typed FeaturePython)
  n = 0.762
FEATURE [App::DocumentObjectGroupPython] G4_TISSUE_SOFT_ICRU_4  label="G4_TISSUE_SOFT_ICRU-4"  # scripted group (container) (typed FeaturePython)
  Dunit = g/cm3
  Dvalue = 1
  Group = -> [H_element101,C_element111,N_element043,O_element095]
  conduct = 2
  density = 1
  expand = 3
  formula = G4_TISSUE_SOFT_ICRU-4
  name = G4_TISSUE_SOFT_ICRU-4
  specific = 4
FEATURE [App::DocumentObjectGroupPython] H_element102  label="H_element : 0.149"  # scripted group (container) (typed FeaturePython)
  n = 0.101869
FEATURE [App::DocumentObjectGroupPython] C_element112  label="C_element : 0.456"  # scripted group (container) (typed FeaturePython)
  n = 0.456179
FEATURE [App::DocumentObjectGroupPython] N_element044  label="N_element : 0.761"  # scripted group (container) (typed FeaturePython)
  n = 0.035172
FEATURE [App::DocumentObjectGroupPython] O_element096  label="O_element : 0.407"  # scripted group (container) (typed FeaturePython)
  n = 0.40678
FEATURE [App::DocumentObjectGroupPython] G4_TISSUE_METHANE  label="G4_TISSUE-METHANE"  # scripted group (container) (typed FeaturePython)
  Dunit = g/cm3
  Dvalue = 0.00106409
  Group = -> [H_element102,C_element112,N_element044,O_element096]
  conduct = 2
  density = 1
  expand = 3
  formula = G4_TISSUE-METHANE
  name = G4_TISSUE-METHANE
  specific = 4
FEATURE [App::DocumentObjectGroupPython] H_element103  label="H_element : 0.103"  # scripted group (container) (typed FeaturePython)
  n = 0.102672
FEATURE [App::DocumentObjectGroupPython] C_element113  label="C_element : 0.569"  # scripted group (container) (typed FeaturePython)
  n = 0.56894
FEATURE [App::DocumentObjectGroupPython] N_element045  label="N_element : 0.762"  # scripted group (container) (typed FeaturePython)
  n = 0.035022
FEATURE [App::DocumentObjectGroupPython] O_element097  label="O_element : 0.293"  # scripted group (container) (typed FeaturePython)
  n = 0.293366
FEATURE [App::DocumentObjectGroupPython] G4_TISSUE_PROPANE  label="G4_TISSUE-PROPANE"  # scripted group (container) (typed FeaturePython)
  Dunit = g/cm3
  Dvalue = 0.00182628
  Group = -> [H_element103,C_element113,N_element045,O_element097]
  conduct = 2
  density = 1
  expand = 3
  formula = G4_TISSUE-PROPANE
  name = G4_TISSUE-PROPANE
  specific = 4
FEATURE [App::DocumentObjectGroupPython] Ti_element003  label="Ti_element : 1"  # scripted group (container) (typed FeaturePython)
  n = 1
  ref = Ti_element
FEATURE [App::DocumentObjectGroupPython] O_element098  label="O_element : 052"  # scripted group (container) (typed FeaturePython)
  n = 2
  ref = O_element
FEATURE [App::DocumentObjectGroupPython] G4_TITANIUM_DIOXIDE  # scripted group (container) (typed FeaturePython)
  Dunit = g/cm3
  Dvalue = 4.26
  Group = -> [Ti_element003,O_element098]
  conduct = 2
  density = 1
  expand = 3
  formula = G4_TITANIUM_DIOXIDE
  name = G4_TITANIUM_DIOXIDE
  specific = 4
FEATURE [App::DocumentObjectGroupPython] C_element114  label="C_element : 061"  # scripted group (container) (typed FeaturePython)
  n = 7
  ref = C_element
FEATURE [App::DocumentObjectGroupPython] H_element104  label="H_element : 055"  # scripted group (container) (typed FeaturePython)
  n = 8
  ref = H_element
FEATURE [App::DocumentObjectGroupPython] G4_TOLUENE  # scripted group (container) (typed FeaturePython)
  Dunit = g/cm3
  Dvalue = 0.8669
  Group = -> [C_element114,H_element104]
  conduct = 2
  density = 1
  expand = 3
  formula = G4_TOLUENE
  name = G4_TOLUENE
  specific = 4
FEATURE [App::DocumentObjectGroupPython] C_element115  label="C_element : 062"  # scripted group (container) (typed FeaturePython)
  n = 2
  ref = C_element
FEATURE [App::DocumentObjectGroupPython] H_element105  label="H_element : 056"  # scripted group (container) (typed FeaturePython)
  n = 1
  ref = H_element
FEATURE [App::DocumentObjectGroupPython] Cl_element028  label="Cl_element : 014"  # scripted group (container) (typed FeaturePython)
  n = 3
  ref = Cl_element
FEATURE [App::DocumentObjectGroupPython] G4_TRICHLOROETHYLENE  # scripted group (container) (typed FeaturePython)
  Dunit = g/cm3
  Dvalue = 1.46
  Group = -> [C_element115,H_element105,Cl_element028]
  conduct = 2
  density = 1
  expand = 3
  formula = G4_TRICHLOROETHYLENE
  name = G4_TRICHLOROETHYLENE
  specific = 4
FEATURE [App::DocumentObjectGroupPython] C_element116  label="C_element : 063"  # scripted group (container) (typed FeaturePython)
  n = 6
  ref = C_element
FEATURE [App::DocumentObjectGroupPython] H_element106  label="H_element : 15"  # scripted group (container) (typed FeaturePython)
  n = 15
  ref = H_element
FEATURE [App::DocumentObjectGroupPython] O_element099  label="O_element : 053"  # scripted group (container) (typed FeaturePython)
  n = 4
  ref = O_element
FEATURE [App::DocumentObjectGroupPython] P_element012  label="P_element : 1"  # scripted group (container) (typed FeaturePython)
  n = 1
  ref = P_element
FEATURE [App::DocumentObjectGroupPython] G4_TRIETHYL_PHOSPHATE  # scripted group (container) (typed FeaturePython)
  Dunit = g/cm3
  Dvalue = 1.07
  Group = -> [C_element116,H_element106,O_element099,P_element012]
  conduct = 2
  density = 1
  expand = 3
  formula = G4_TRIETHYL_PHOSPHATE
  name = G4_TRIETHYL_PHOSPHATE
  specific = 4
FEATURE [App::DocumentObjectGroupPython] W_element003  label="W_element : 003"  # scripted group (container) (typed FeaturePython)
  n = 1
  ref = W_element
FEATURE [App::DocumentObjectGroupPython] F_element017  label="F_element : 6"  # scripted group (container) (typed FeaturePython)
  n = 6
  ref = F_element
FEATURE [App::DocumentObjectGroupPython] G4_TUNGSTEN_HEXAFLUORIDE  # scripted group (container) (typed FeaturePython)
  Dunit = g/cm3
  Dvalue = 2.4
  Group = -> [W_element003,F_element017]
  conduct = 2
  density = 1
  expand = 3
  formula = G4_TUNGSTEN_HEXAFLUORIDE
  name = G4_TUNGSTEN_HEXAFLUORIDE
  specific = 4
FEATURE [App::DocumentObjectGroupPython] U_element001  label="U_element : 1"  # scripted group (container) (typed FeaturePython)
  n = 1
  ref = U_element
FEATURE [App::DocumentObjectGroupPython] C_element117  label="C_element : 064"  # scripted group (container) (typed FeaturePython)
  n = 2
  ref = C_element
FEATURE [App::DocumentObjectGroupPython] G4_URANIUM_DICARBIDE  # scripted group (container) (typed FeaturePython)
  Dunit = g/cm3
  Dvalue = 11.28
  Group = -> [U_element001,C_element117]
  conduct = 2
  density = 1
  expand = 3
  formula = G4_URANIUM_DICARBIDE
  name = G4_URANIUM_DICARBIDE
  specific = 4
FEATURE [App::DocumentObjectGroupPython] U_element002  label="U_element : 002"  # scripted group (container) (typed FeaturePython)
  n = 1
  ref = U_element
FEATURE [App::DocumentObjectGroupPython] C_element118  label="C_element : 065"  # scripted group (container) (typed FeaturePython)
  n = 1
  ref = C_element
FEATURE [App::DocumentObjectGroupPython] G4_URANIUM_MONOCARBIDE  # scripted group (container) (typed FeaturePython)
  Dunit = g/cm3
  Dvalue = 13.63
  Group = -> [U_element002,C_element118]
  conduct = 2
  density = 1
  expand = 3
  formula = G4_URANIUM_MONOCARBIDE
  name = G4_URANIUM_MONOCARBIDE
  specific = 4
FEATURE [App::DocumentObjectGroupPython] U_element003  label="U_element : 003"  # scripted group (container) (typed FeaturePython)
  n = 1
  ref = U_element
FEATURE [App::DocumentObjectGroupPython] O_element100  label="O_element : 054"  # scripted group (container) (typed FeaturePython)
  n = 2
  ref = O_element
FEATURE [App::DocumentObjectGroupPython] G4_URANIUM_OXIDE  # scripted group (container) (typed FeaturePython)
  Dunit = g/cm3
  Dvalue = 10.96
  Group = -> [U_element003,O_element100]
  conduct = 2
  density = 1
  expand = 3
  formula = G4_URANIUM_OXIDE
  name = G4_URANIUM_OXIDE
  specific = 4
FEATURE [App::DocumentObjectGroupPython] C_element119  label="C_element : 066"  # scripted group (container) (typed FeaturePython)
  n = 1
  ref = C_element
FEATURE [App::DocumentObjectGroupPython] H_element107  label="H_element : 057"  # scripted group (container) (typed FeaturePython)
  n = 4
  ref = H_element
FEATURE [App::DocumentObjectGroupPython] N_element046  label="N_element : 019"  # scripted group (container) (typed FeaturePython)
  n = 2
  ref = N_element
FEATURE [App::DocumentObjectGroupPython] O_element101  label="O_element : 055"  # scripted group (container) (typed FeaturePython)
  n = 1
  ref = O_element
FEATURE [App::DocumentObjectGroupPython] G4_UREA  # scripted group (container) (typed FeaturePython)
  Dunit = g/cm3
  Dvalue = 1.323
  Group = -> [C_element119,H_element107,N_element046,O_element101]
  conduct = 2
  density = 1
  expand = 3
  formula = G4_UREA
  name = G4_UREA
  specific = 4
FEATURE [App::DocumentObjectGroupPython] C_element120  label="C_element : 067"  # scripted group (container) (typed FeaturePython)
  n = 5
  ref = C_element
FEATURE [App::DocumentObjectGroupPython] H_element108  label="H_element : 058"  # scripted group (container) (typed FeaturePython)
  n = 11
  ref = H_element
FEATURE [App::DocumentObjectGroupPython] N_element047  label="N_element : 020"  # scripted group (container) (typed FeaturePython)
  n = 1
  ref = N_element
FEATURE [App::DocumentObjectGroupPython] O_element102  label="O_element : 056"  # scripted group (container) (typed FeaturePython)
  n = 2
  ref = O_element
FEATURE [App::DocumentObjectGroupPython] G4_VALINE  # scripted group (container) (typed FeaturePython)
  Dunit = g/cm3
  Dvalue = 1.23
  Group = -> [C_element120,H_element108,N_element047,O_element102]
  conduct = 2
  density = 1
  expand = 3
  formula = G4_VALINE
  name = G4_VALINE
  specific = 4
FEATURE [App::DocumentObjectGroupPython] H_element109  label="H_element : 0.009"  # scripted group (container) (typed FeaturePython)
  n = 0.009417
FEATURE [App::DocumentObjectGroupPython] C_element121  label="C_element : 0.281"  # scripted group (container) (typed FeaturePython)
  n = 0.280555
FEATURE [App::DocumentObjectGroupPython] F_element018  label="F_element : 0.710"  # scripted group (container) (typed FeaturePython)
  n = 0.710028
FEATURE [App::DocumentObjectGroupPython] G4_VITON  # scripted group (container) (typed FeaturePython)
  Dunit = g/cm3
  Dvalue = 1.8
  Group = -> [H_element109,C_element121,F_element018]
  conduct = 2
  density = 1
  expand = 3
  formula = G4_VITON
  name = G4_VITON
  specific = 4
FEATURE [App::DocumentObjectGroupPython] H_element110  label="H_element : 059"  # scripted group (container) (typed FeaturePython)
  n = 2
  ref = H_element
FEATURE [App::DocumentObjectGroupPython] O_element103  label="O_element : 057"  # scripted group (container) (typed FeaturePython)
  n = 1
  ref = O_element
FEATURE [App::DocumentObjectGroupPython] G4_WATER  # scripted group (container) (typed FeaturePython)
  Dunit = g/cm3
  Dvalue = 1
  Group = -> [H_element110,O_element103]
  conduct = 2
  density = 1
  expand = 3
  formula = G4_WATER
  name = G4_WATER
  specific = 4
FEATURE [App::DocumentObjectGroupPython] H_element111  label="H_element : 060"  # scripted group (container) (typed FeaturePython)
  n = 2
  ref = H_element
FEATURE [App::DocumentObjectGroupPython] O_element104  label="O_element : 058"  # scripted group (container) (typed FeaturePython)
  n = 1
  ref = O_element
FEATURE [App::DocumentObjectGroupPython] G4_WATER_VAPOR  # scripted group (container) (typed FeaturePython)
  Dunit = g/cm3
  Dvalue = 0.000756182
  Group = -> [H_element111,O_element104]
  conduct = 2
  density = 1
  expand = 3
  formula = G4_WATER_VAPOR
  name = G4_WATER_VAPOR
  specific = 4
FEATURE [App::DocumentObjectGroupPython] C_element122  label="C_element : 068"  # scripted group (container) (typed FeaturePython)
  n = 8
  ref = C_element
FEATURE [App::DocumentObjectGroupPython] H_element112  label="H_element : 061"  # scripted group (container) (typed FeaturePython)
  n = 10
  ref = H_element
FEATURE [App::DocumentObjectGroupPython] G4_XYLENE  # scripted group (container) (typed FeaturePython)
  Dunit = g/cm3
  Dvalue = 0.87
  Group = -> [C_element122,H_element112]
  conduct = 2
  density = 1
  expand = 3
  formula = G4_XYLENE
  name = G4_XYLENE
  specific = 4
FEATURE [App::DocumentObjectGroupPython] C_element123  label="C_element : 069"  # scripted group (container) (typed FeaturePython)
  n = 1
  ref = C_element
FEATURE [App::DocumentObjectGroupPython] G4_GRAPHITE  # scripted group (container) (typed FeaturePython)
  Dunit = g/cm3
  Dvalue = 2.21
  Group = -> [C_element123]
  conduct = 2
  density = 1
  expand = 3
  formula = G4_GRAPHITE
  name = G4_GRAPHITE
  specific = 4
FEATURE [App::DocumentObjectGroupPython] NIST  # scripted group (container) (typed FeaturePython)
  Group = -> [G4_A_150_TISSUE,G4_ACETONE,G4_ACETYLENE,G4_ADENINE,G4_ADIPOSE_TISSUE_ICRP,G4_AIR,G4_ALANINE,G4_ALUMINUM_OXIDE,G4_AMBER,G4_AMMONIA,G4_ANILINE,G4_ANTHRACENE,G4_B_100_BONE,G4_BAKELITE,G4_BARIUM_FLUORIDE,G4_BARIUM_SULFATE,G4_BENZENE,G4_BERYLLIUM_OXIDE,G4_BGO,G4_BLOOD_ICRP,G4_BONE_COMPACT_ICRU,G4_BONE_CORTICAL_ICRP,G4_BORON_CARBIDE,G4_BORON_OXIDE,G4_BRAIN_ICRP,G4_BUTANE,G4_N_BUTYL_ALCOHOL,G4_C_552,+152 more]
FEATURE [App::DocumentObjectGroupPython] H_element113  label="H_element : 062"  # scripted group (container) (typed FeaturePython)
  n = 1
  ref = H_element
FEATURE [App::DocumentObjectGroupPython] G4_H  # scripted group (container) (typed FeaturePython)
  Dunit = g/cm3
  Dvalue = 8.3748e-05
  Group = -> [H_element113]
  conduct = 2
  density = 1
  expand = 3
  formula = H
  name = G4_H
  specific = 4
FEATURE [App::DocumentObjectGroupPython] He_element001  label="He_element : 1"  # scripted group (container) (typed FeaturePython)
  n = 1
  ref = He_element
FEATURE [App::DocumentObjectGroupPython] G4_He  # scripted group (container) (typed FeaturePython)
  Dunit = g/cm3
  Dvalue = 0.000166322
  Group = -> [He_element001]
  conduct = 2
  density = 1
  expand = 3
  formula = He
  name = G4_He
  specific = 4
FEATURE [App::DocumentObjectGroupPython] Li_element008  label="Li_element : 008"  # scripted group (container) (typed FeaturePython)
  n = 1
  ref = Li_element
FEATURE [App::DocumentObjectGroupPython] G4_Li  # scripted group (container) (typed FeaturePython)
  Dunit = g/cm3
  Dvalue = 0.534
  Group = -> [Li_element008]
  conduct = 2
  density = 1
  expand = 3
  formula = Li
  name = G4_Li
  specific = 4
FEATURE [App::DocumentObjectGroupPython] Be_element002  label="Be_element : 002"  # scripted group (container) (typed FeaturePython)
  n = 1
  ref = Be_element
FEATURE [App::DocumentObjectGroupPython] G4_Be  # scripted group (container) (typed FeaturePython)
  Dunit = g/cm3
  Dvalue = 1.848
  Group = -> [Be_element002]
  conduct = 2
  density = 1
  expand = 3
  formula = Be
  name = G4_Be
  specific = 4
FEATURE [App::DocumentObjectGroupPython] B_element007  label="B_element : 007"  # scripted group (container) (typed FeaturePython)
  n = 1
  ref = B_element
FEATURE [App::DocumentObjectGroupPython] G4_B  # scripted group (container) (typed FeaturePython)
  Dunit = g/cm3
  Dvalue = 2.37
  Group = -> [B_element007]
  conduct = 2
  density = 1
  expand = 3
  formula = B
  name = G4_B
  specific = 4
FEATURE [App::DocumentObjectGroupPython] C_element124  label="C_element : 070"  # scripted group (container) (typed FeaturePython)
  n = 1
  ref = C_element
FEATURE [App::DocumentObjectGroupPython] G4_C  # scripted group (container) (typed FeaturePython)
  Dunit = g/cm3
  Dvalue = 2
  Group = -> [C_element124]
  conduct = 2
  density = 1
  expand = 3
  formula = C
  name = G4_C
  specific = 4
FEATURE [App::DocumentObjectGroupPython] N_element048  label="N_element : 021"  # scripted group (container) (typed FeaturePython)
  n = 1
  ref = N_element
FEATURE [App::DocumentObjectGroupPython] G4_N  # scripted group (container) (typed FeaturePython)
  Dunit = g/cm3
  Dvalue = 0.0011652
  Group = -> [N_element048]
  conduct = 2
  density = 1
  expand = 3
  formula = N
  name = G4_N
  specific = 4
FEATURE [App::DocumentObjectGroupPython] O_element105  label="O_element : 059"  # scripted group (container) (typed FeaturePython)
  n = 1
  ref = O_element
FEATURE [App::DocumentObjectGroupPython] G4_O  # scripted group (container) (typed FeaturePython)
  Dunit = g/cm3
  Dvalue = 0.00133151
  Group = -> [O_element105]
  conduct = 2
  density = 1
  expand = 3
  formula = O
  name = G4_O
  specific = 4
FEATURE [App::DocumentObjectGroupPython] F_element019  label="F_element : 008"  # scripted group (container) (typed FeaturePython)
  n = 1
  ref = F_element
FEATURE [App::DocumentObjectGroupPython] G4_F  # scripted group (container) (typed FeaturePython)
  Dunit = g/cm3
  Dvalue = 0.00158029
  Group = -> [F_element019]
  conduct = 2
  density = 1
  expand = 3
  formula = F
  name = G4_F
  specific = 4
FEATURE [App::DocumentObjectGroupPython] Ne_element001  label="Ne_element : 1"  # scripted group (container) (typed FeaturePython)
  n = 1
  ref = Ne_element
FEATURE [App::DocumentObjectGroupPython] G4_Ne  # scripted group (container) (typed FeaturePython)
  Dunit = g/cm3
  Dvalue = 0.000838505
  Group = -> [Ne_element001]
  conduct = 2
  density = 1
  expand = 3
  formula = Ne
  name = G4_Ne
  specific = 4
FEATURE [App::DocumentObjectGroupPython] Na_element020  label="Na_element : 005"  # scripted group (container) (typed FeaturePython)
  n = 1
  ref = Na_element
FEATURE [App::DocumentObjectGroupPython] G4_Na  # scripted group (container) (typed FeaturePython)
  Dunit = g/cm3
  Dvalue = 0.971
  Group = -> [Na_element020]
  conduct = 2
  density = 1
  expand = 3
  formula = Na
  name = G4_Na
  specific = 4
FEATURE [App::DocumentObjectGroupPython] Mg_element011  label="Mg_element : 005"  # scripted group (container) (typed FeaturePython)
  n = 1
  ref = Mg_element
FEATURE [App::DocumentObjectGroupPython] G4_Mg  # scripted group (container) (typed FeaturePython)
  Dunit = g/cm3
  Dvalue = 1.74
  Group = -> [Mg_element011]
  conduct = 2
  density = 1
  expand = 3
  formula = Mg
  name = G4_Mg
  specific = 4
FEATURE [App::DocumentObjectGroupPython] Al_element004  label="Al_element : 1"  # scripted group (container) (typed FeaturePython)
  n = 1
  ref = Al_element
FEATURE [App::DocumentObjectGroupPython] G4_Al  # scripted group (container) (typed FeaturePython)
  Dunit = g/cm3
  Dvalue = 2.699
  Group = -> [Al_element004]
  conduct = 2
  density = 1
  expand = 3
  formula = Al
  name = G4_Al
  specific = 4
FEATURE [App::DocumentObjectGroupPython] Si_element007  label="Si_element : 002"  # scripted group (container) (typed FeaturePython)
  n = 1
  ref = Si_element
FEATURE [App::DocumentObjectGroupPython] G4_Si  # scripted group (container) (typed FeaturePython)
  Dunit = g/cm3
  Dvalue = 2.33
  Group = -> [Si_element007]
  conduct = 2
  density = 1
  expand = 3
  formula = Si
  name = G4_Si
  specific = 4
FEATURE [App::DocumentObjectGroupPython] P_element013  label="P_element : 002"  # scripted group (container) (typed FeaturePython)
  n = 1
  ref = P_element
FEATURE [App::DocumentObjectGroupPython] G4_P  # scripted group (container) (typed FeaturePython)
  Dunit = g/cm3
  Dvalue = 2.2
  Group = -> [P_element013]
  conduct = 2
  density = 1
  expand = 3
  formula = P
  name = G4_P
  specific = 4
FEATURE [App::DocumentObjectGroupPython] S_element023  label="S_element : 007"  # scripted group (container) (typed FeaturePython)
  n = 1
  ref = S_element
FEATURE [App::DocumentObjectGroupPython] G4_S  # scripted group (container) (typed FeaturePython)
  Dunit = g/cm3
  Dvalue = 2
  Group = -> [S_element023]
  conduct = 2
  density = 1
  expand = 3
  formula = S
  name = G4_S
  specific = 4
FEATURE [App::DocumentObjectGroupPython] Cl_element029  label="Cl_element : 015"  # scripted group (container) (typed FeaturePython)
  n = 1
  ref = Cl_element
FEATURE [App::DocumentObjectGroupPython] G4_Cl  # scripted group (container) (typed FeaturePython)
  Dunit = g/cm3
  Dvalue = 0.00299473
  Group = -> [Cl_element029]
  conduct = 2
  density = 1
  expand = 3
  formula = Cl
  name = G4_Cl
  specific = 4
FEATURE [App::DocumentObjectGroupPython] Ar_element002  label="Ar_element : 1"  # scripted group (container) (typed FeaturePython)
  n = 1
  ref = Ar_element
FEATURE [App::DocumentObjectGroupPython] G4_Ar  # scripted group (container) (typed FeaturePython)
  Dunit = g/cm3
  Dvalue = 0.00166201
  Group = -> [Ar_element002]
  conduct = 2
  density = 1
  expand = 3
  formula = Ar
  name = G4_Ar
  specific = 4
FEATURE [App::DocumentObjectGroupPython] K_element013  label="K_element : 003"  # scripted group (container) (typed FeaturePython)
  n = 1
  ref = K_element
FEATURE [App::DocumentObjectGroupPython] G4_K  # scripted group (container) (typed FeaturePython)
  Dunit = g/cm3
  Dvalue = 0.862
  Group = -> [K_element013]
  conduct = 2
  density = 1
  expand = 3
  formula = K
  name = G4_K
  specific = 4
FEATURE [App::DocumentObjectGroupPython] Ca_element014  label="Ca_element : 007"  # scripted group (container) (typed FeaturePython)
  n = 1
  ref = Ca_element
FEATURE [App::DocumentObjectGroupPython] G4_Ca  # scripted group (container) (typed FeaturePython)
  Dunit = g/cm3
  Dvalue = 1.55
  Group = -> [Ca_element014]
  conduct = 2
  density = 1
  expand = 3
  formula = Ca
  name = G4_Ca
  specific = 4
FEATURE [App::DocumentObjectGroupPython] Sc_element001  label="Sc_element : 1"  # scripted group (container) (typed FeaturePython)
  n = 1
  ref = Sc_element
FEATURE [App::DocumentObjectGroupPython] G4_Sc  # scripted group (container) (typed FeaturePython)
  Dunit = g/cm3
  Dvalue = 2.989
  Group = -> [Sc_element001]
  conduct = 2
  density = 1
  expand = 3
  formula = Sc
  name = G4_Sc
  specific = 4
FEATURE [App::DocumentObjectGroupPython] Ti_element004  label="Ti_element : 002"  # scripted group (container) (typed FeaturePython)
  n = 1
  ref = Ti_element
FEATURE [App::DocumentObjectGroupPython] G4_Ti  # scripted group (container) (typed FeaturePython)
  Dunit = g/cm3
  Dvalue = 4.54
  Group = -> [Ti_element004]
  conduct = 2
  density = 1
  expand = 3
  formula = Ti
  name = G4_Ti
  specific = 4
FEATURE [App::DocumentObjectGroupPython] V_element001  label="V_element : 1"  # scripted group (container) (typed FeaturePython)
  n = 1
  ref = V_element
FEATURE [App::DocumentObjectGroupPython] G4_V  # scripted group (container) (typed FeaturePython)
  Dunit = g/cm3
  Dvalue = 6.11
  Group = -> [V_element001]
  conduct = 2
  density = 1
  expand = 3
  formula = V
  name = G4_V
  specific = 4
FEATURE [App::DocumentObjectGroupPython] Cr_element001  label="Cr_element : 1"  # scripted group (container) (typed FeaturePython)
  n = 1
  ref = Cr_element
FEATURE [App::DocumentObjectGroupPython] G4_Cr  # scripted group (container) (typed FeaturePython)
  Dunit = g/cm3
  Dvalue = 7.18
  Group = -> [Cr_element001]
  conduct = 2
  density = 1
  expand = 3
  formula = Cr
  name = G4_Cr
  specific = 4
FEATURE [App::DocumentObjectGroupPython] Mn_element001  label="Mn_element : 1"  # scripted group (container) (typed FeaturePython)
  n = 1
  ref = Mn_element
FEATURE [App::DocumentObjectGroupPython] G4_Mn  # scripted group (container) (typed FeaturePython)
  Dunit = g/cm3
  Dvalue = 7.44
  Group = -> [Mn_element001]
  conduct = 2
  density = 1
  expand = 3
  formula = Mn
  name = G4_Mn
  specific = 4
FEATURE [App::DocumentObjectGroupPython] Fe_element007  label="Fe_element : 004"  # scripted group (container) (typed FeaturePython)
  n = 1
  ref = Fe_element
FEATURE [App::DocumentObjectGroupPython] G4_Fe  # scripted group (container) (typed FeaturePython)
  Dunit = g/cm3
  Dvalue = 7.874
  Group = -> [Fe_element007]
  conduct = 2
  density = 1
  expand = 3
  formula = Fe
  name = G4_Fe
  specific = 4
FEATURE [App::DocumentObjectGroupPython] Co_element001  label="Co_element : 1"  # scripted group (container) (typed FeaturePython)
  n = 1
  ref = Co_element
FEATURE [App::DocumentObjectGroupPython] G4_Co  # scripted group (container) (typed FeaturePython)
  Dunit = g/cm3
  Dvalue = 8.9
  Group = -> [Co_element001]
  conduct = 2
  density = 1
  expand = 3
  formula = Co
  name = G4_Co
  specific = 4
FEATURE [App::DocumentObjectGroupPython] Ni_element001  label="Ni_element : 1"  # scripted group (container) (typed FeaturePython)
  n = 1
  ref = Ni_element
FEATURE [App::DocumentObjectGroupPython] G4_Ni  # scripted group (container) (typed FeaturePython)
  Dunit = g/cm3
  Dvalue = 8.902
  Group = -> [Ni_element001]
  conduct = 2
  density = 1
  expand = 3
  formula = Ni
  name = G4_Ni
  specific = 4
FEATURE [App::DocumentObjectGroupPython] Cu_element001  label="Cu_element : 1"  # scripted group (container) (typed FeaturePython)
  n = 1
  ref = Cu_element
FEATURE [App::DocumentObjectGroupPython] G4_Cu  # scripted group (container) (typed FeaturePython)
  Dunit = g/cm3
  Dvalue = 8.96
  Group = -> [Cu_element001]
  conduct = 2
  density = 1
  expand = 3
  formula = Cu
  name = G4_Cu
  specific = 4
FEATURE [App::DocumentObjectGroupPython] Zn_element001  label="Zn_element : 1"  # scripted group (container) (typed FeaturePython)
  n = 1
  ref = Zn_element
FEATURE [App::DocumentObjectGroupPython] G4_Zn  # scripted group (container) (typed FeaturePython)
  Dunit = g/cm3
  Dvalue = 7.133
  Group = -> [Zn_element001]
  conduct = 2
  density = 1
  expand = 3
  formula = Zn
  name = G4_Zn
  specific = 4
FEATURE [App::DocumentObjectGroupPython] Ga_element002  label="Ga_element : 002"  # scripted group (container) (typed FeaturePython)
  n = 1
  ref = Ga_element
FEATURE [App::DocumentObjectGroupPython] G4_Ga  # scripted group (container) (typed FeaturePython)
  Dunit = g/cm3
  Dvalue = 5.904
  Group = -> [Ga_element002]
  conduct = 2
  density = 1
  expand = 3
  formula = Ga
  name = G4_Ga
  specific = 4
FEATURE [App::DocumentObjectGroupPython] Ge_element002  label="Ge_element : 1"  # scripted group (container) (typed FeaturePython)
  n = 1
  ref = Ge_element
FEATURE [App::DocumentObjectGroupPython] G4_Ge  # scripted group (container) (typed FeaturePython)
  Dunit = g/cm3
  Dvalue = 5.323
  Group = -> [Ge_element002]
  conduct = 2
  density = 1
  expand = 3
  formula = Ge
  name = G4_Ge
  specific = 4
FEATURE [App::DocumentObjectGroupPython] As_element003  label="As_element : 002"  # scripted group (container) (typed FeaturePython)
  n = 1
  ref = As_element
FEATURE [App::DocumentObjectGroupPython] G4_As  # scripted group (container) (typed FeaturePython)
  Dunit = g/cm3
  Dvalue = 5.73
  Group = -> [As_element003]
  conduct = 2
  density = 1
  expand = 3
  formula = As
  name = G4_As
  specific = 4
FEATURE [App::DocumentObjectGroupPython] Se_element001  label="Se_element : 1"  # scripted group (container) (typed FeaturePython)
  n = 1
  ref = Se_element
FEATURE [App::DocumentObjectGroupPython] G4_Se  # scripted group (container) (typed FeaturePython)
  Dunit = g/cm3
  Dvalue = 4.5
  Group = -> [Se_element001]
  conduct = 2
  density = 1
  expand = 3
  formula = Se
  name = G4_Se
  specific = 4
FEATURE [App::DocumentObjectGroupPython] Br_element007  label="Br_element : 004"  # scripted group (container) (typed FeaturePython)
  n = 1
  ref = Br_element
FEATURE [App::DocumentObjectGroupPython] G4_Br  # scripted group (container) (typed FeaturePython)
  Dunit = g/cm3
  Dvalue = 0.0070721
  Group = -> [Br_element007]
  conduct = 2
  density = 1
  expand = 3
  formula = Br
  name = G4_Br
  specific = 4
FEATURE [App::DocumentObjectGroupPython] Kr_element001  label="Kr_element : 1"  # scripted group (container) (typed FeaturePython)
  n = 1
  ref = Kr_element
FEATURE [App::DocumentObjectGroupPython] G4_Kr  # scripted group (container) (typed FeaturePython)
  Dunit = g/cm3
  Dvalue = 0.00347832
  Group = -> [Kr_element001]
  conduct = 2
  density = 1
  expand = 3
  formula = Kr
  name = G4_Kr
  specific = 4
FEATURE [App::DocumentObjectGroupPython] Rb_element001  label="Rb_element : 1"  # scripted group (container) (typed FeaturePython)
  n = 1
  ref = Rb_element
FEATURE [App::DocumentObjectGroupPython] G4_Rb  # scripted group (container) (typed FeaturePython)
  Dunit = g/cm3
  Dvalue = 1.532
  Group = -> [Rb_element001]
  conduct = 2
  density = 1
  expand = 3
  formula = Rb
  name = G4_Rb
  specific = 4
FEATURE [App::DocumentObjectGroupPython] Sr_element001  label="Sr_element : 1"  # scripted group (container) (typed FeaturePython)
  n = 1
  ref = Sr_element
FEATURE [App::DocumentObjectGroupPython] G4_Sr  # scripted group (container) (typed FeaturePython)
  Dunit = g/cm3
  Dvalue = 2.54
  Group = -> [Sr_element001]
  conduct = 2
  density = 1
  expand = 3
  formula = Sr
  name = G4_Sr
  specific = 4
FEATURE [App::DocumentObjectGroupPython] Y_element001  label="Y_element : 1"  # scripted group (container) (typed FeaturePython)
  n = 1
  ref = Y_element
FEATURE [App::DocumentObjectGroupPython] G4_Y  # scripted group (container) (typed FeaturePython)
  Dunit = g/cm3
  Dvalue = 4.469
  Group = -> [Y_element001]
  conduct = 2
  density = 1
  expand = 3
  formula = Y
  name = G4_Y
  specific = 4
FEATURE [App::DocumentObjectGroupPython] Zr_element001  label="Zr_element : 1"  # scripted group (container) (typed FeaturePython)
  n = 1
  ref = Zr_element
FEATURE [App::DocumentObjectGroupPython] G4_Zr  # scripted group (container) (typed FeaturePython)
  Dunit = g/cm3
  Dvalue = 6.506
  Group = -> [Zr_element001]
  conduct = 2
  density = 1
  expand = 3
  formula = Zr
  name = G4_Zr
  specific = 4
FEATURE [App::DocumentObjectGroupPython] Nb_element001  label="Nb_element : 1"  # scripted group (container) (typed FeaturePython)
  n = 1
  ref = Nb_element
FEATURE [App::DocumentObjectGroupPython] G4_Nb  # scripted group (container) (typed FeaturePython)
  Dunit = g/cm3
  Dvalue = 8.57
  Group = -> [Nb_element001]
  conduct = 2
  density = 1
  expand = 3
  formula = Nb
  name = G4_Nb
  specific = 4
FEATURE [App::DocumentObjectGroupPython] Mo_element001  label="Mo_element : 1"  # scripted group (container) (typed FeaturePython)
  n = 1
  ref = Mo_element
FEATURE [App::DocumentObjectGroupPython] G4_Mo  # scripted group (container) (typed FeaturePython)
  Dunit = g/cm3
  Dvalue = 10.22
  Group = -> [Mo_element001]
  conduct = 2
  density = 1
  expand = 3
  formula = Mo
  name = G4_Mo
  specific = 4
FEATURE [App::DocumentObjectGroupPython] Tc_element001  label="Tc_element : 1"  # scripted group (container) (typed FeaturePython)
  n = 1
  ref = Tc_element
FEATURE [App::DocumentObjectGroupPython] G4_Tc  # scripted group (container) (typed FeaturePython)
  Dunit = g/cm3
  Dvalue = 11.5
  Group = -> [Tc_element001]
  conduct = 2
  density = 1
  expand = 3
  formula = Tc
  name = G4_Tc
  specific = 4
FEATURE [App::DocumentObjectGroupPython] Ru_element001  label="Ru_element : 1"  # scripted group (container) (typed FeaturePython)
  n = 1
  ref = Ru_element
FEATURE [App::DocumentObjectGroupPython] G4_Ru  # scripted group (container) (typed FeaturePython)
  Dunit = g/cm3
  Dvalue = 12.41
  Group = -> [Ru_element001]
  conduct = 2
  density = 1
  expand = 3
  formula = Ru
  name = G4_Ru
  specific = 4
FEATURE [App::DocumentObjectGroupPython] Rh_element001  label="Rh_element : 1"  # scripted group (container) (typed FeaturePython)
  n = 1
  ref = Rh_element
FEATURE [App::DocumentObjectGroupPython] G4_Rh  # scripted group (container) (typed FeaturePython)
  Dunit = g/cm3
  Dvalue = 12.41
  Group = -> [Rh_element001]
  conduct = 2
  density = 1
  expand = 3
  formula = Rh
  name = G4_Rh
  specific = 4
FEATURE [App::DocumentObjectGroupPython] Pd_element001  label="Pd_element : 1"  # scripted group (container) (typed FeaturePython)
  n = 1
  ref = Pd_element
FEATURE [App::DocumentObjectGroupPython] G4_Pd  # scripted group (container) (typed FeaturePython)
  Dunit = g/cm3
  Dvalue = 12.02
  Group = -> [Pd_element001]
  conduct = 2
  density = 1
  expand = 3
  formula = Pd
  name = G4_Pd
  specific = 4
FEATURE [App::DocumentObjectGroupPython] Ag_element006  label="Ag_element : 004"  # scripted group (container) (typed FeaturePython)
  n = 1
  ref = Ag_element
FEATURE [App::DocumentObjectGroupPython] G4_Ag  # scripted group (container) (typed FeaturePython)
  Dunit = g/cm3
  Dvalue = 10.5
  Group = -> [Ag_element006]
  conduct = 2
  density = 1
  expand = 3
  formula = Ag
  name = G4_Ag
  specific = 4
FEATURE [App::DocumentObjectGroupPython] Cd_element003  label="Cd_element : 003"  # scripted group (container) (typed FeaturePython)
  n = 1
  ref = Cd_element
FEATURE [App::DocumentObjectGroupPython] G4_Cd  # scripted group (container) (typed FeaturePython)
  Dunit = g/cm3
  Dvalue = 8.65
  Group = -> [Cd_element003]
  conduct = 2
  density = 1
  expand = 3
  formula = Cd
  name = G4_Cd
  specific = 4
FEATURE [App::DocumentObjectGroupPython] In_element001  label="In_element : 1"  # scripted group (container) (typed FeaturePython)
  n = 1
  ref = In_element
FEATURE [App::DocumentObjectGroupPython] G4_In  # scripted group (container) (typed FeaturePython)
  Dunit = g/cm3
  Dvalue = 7.31
  Group = -> [In_element001]
  conduct = 2
  density = 1
  expand = 3
  formula = In
  name = G4_In
  specific = 4
FEATURE [App::DocumentObjectGroupPython] Sn_element001  label="Sn_element : 1"  # scripted group (container) (typed FeaturePython)
  n = 1
  ref = Sn_element
FEATURE [App::DocumentObjectGroupPython] G4_Sn  # scripted group (container) (typed FeaturePython)
  Dunit = g/cm3
  Dvalue = 7.31
  Group = -> [Sn_element001]
  conduct = 2
  density = 1
  expand = 3
  formula = Sn
  name = G4_Sn
  specific = 4
FEATURE [App::DocumentObjectGroupPython] Sb_element001  label="Sb_element : 1"  # scripted group (container) (typed FeaturePython)
  n = 1
  ref = Sb_element
FEATURE [App::DocumentObjectGroupPython] G4_Sb  # scripted group (container) (typed FeaturePython)
  Dunit = g/cm3
  Dvalue = 6.691
  Group = -> [Sb_element001]
  conduct = 2
  density = 1
  expand = 3
  formula = Sb
  name = G4_Sb
  specific = 4
FEATURE [App::DocumentObjectGroupPython] Te_element002  label="Te_element : 002"  # scripted group (container) (typed FeaturePython)
  n = 1
  ref = Te_element
FEATURE [App::DocumentObjectGroupPython] G4_Te  # scripted group (container) (typed FeaturePython)
  Dunit = g/cm3
  Dvalue = 6.24
  Group = -> [Te_element002]
  conduct = 2
  density = 1
  expand = 3
  formula = Te
  name = G4_Te
  specific = 4
FEATURE [App::DocumentObjectGroupPython] I_element010  label="I_element : 006"  # scripted group (container) (typed FeaturePython)
  n = 1
  ref = I_element
FEATURE [App::DocumentObjectGroupPython] G4_I  # scripted group (container) (typed FeaturePython)
  Dunit = g/cm3
  Dvalue = 4.93
  Group = -> [I_element010]
  conduct = 2
  density = 1
  expand = 3
  formula = I
  name = G4_I
  specific = 4
FEATURE [App::DocumentObjectGroupPython] Xe_element001  label="Xe_element : 1"  # scripted group (container) (typed FeaturePython)
  n = 1
  ref = Xe_element
FEATURE [App::DocumentObjectGroupPython] G4_Xe  # scripted group (container) (typed FeaturePython)
  Dunit = g/cm3
  Dvalue = 0.00548536
  Group = -> [Xe_element001]
  conduct = 2
  density = 1
  expand = 3
  formula = Xe
  name = G4_Xe
  specific = 4
FEATURE [App::DocumentObjectGroupPython] Cs_element003  label="Cs_element : 003"  # scripted group (container) (typed FeaturePython)
  n = 1
  ref = Cs_element
FEATURE [App::DocumentObjectGroupPython] G4_Cs  # scripted group (container) (typed FeaturePython)
  Dunit = g/cm3
  Dvalue = 1.873
  Group = -> [Cs_element003]
  conduct = 2
  density = 1
  expand = 3
  formula = Cs
  name = G4_Cs
  specific = 4
FEATURE [App::DocumentObjectGroupPython] Ba_element003  label="Ba_element : 003"  # scripted group (container) (typed FeaturePython)
  n = 1
  ref = Ba_element
FEATURE [App::DocumentObjectGroupPython] G4_Ba  # scripted group (container) (typed FeaturePython)
  Dunit = g/cm3
  Dvalue = 3.5
  Group = -> [Ba_element003]
  conduct = 2
  density = 1
  expand = 3
  formula = Ba
  name = G4_Ba
  specific = 4
FEATURE [App::DocumentObjectGroupPython] La_element003  label="La_element : 003"  # scripted group (container) (typed FeaturePython)
  n = 1
  ref = La_element
FEATURE [App::DocumentObjectGroupPython] G4_La  # scripted group (container) (typed FeaturePython)
  Dunit = g/cm3
  Dvalue = 6.154
  Group = -> [La_element003]
  conduct = 2
  density = 1
  expand = 3
  formula = La
  name = G4_La
  specific = 4
FEATURE [App::DocumentObjectGroupPython] Ce_element002  label="Ce_element : 1"  # scripted group (container) (typed FeaturePython)
  n = 1
  ref = Ce_element
FEATURE [App::DocumentObjectGroupPython] G4_Ce  # scripted group (container) (typed FeaturePython)
  Dunit = g/cm3
  Dvalue = 6.657
  Group = -> [Ce_element002]
  conduct = 2
  density = 1
  expand = 3
  formula = Ce
  name = G4_Ce
  specific = 4
FEATURE [App::DocumentObjectGroupPython] Pr_element001  label="Pr_element : 1"  # scripted group (container) (typed FeaturePython)
  n = 1
  ref = Pr_element
FEATURE [App::DocumentObjectGroupPython] G4_Pr  # scripted group (container) (typed FeaturePython)
  Dunit = g/cm3
  Dvalue = 6.71
  Group = -> [Pr_element001]
  conduct = 2
  density = 1
  expand = 3
  formula = Pr
  name = G4_Pr
  specific = 4
FEATURE [App::DocumentObjectGroupPython] Nd_element001  label="Nd_element : 1"  # scripted group (container) (typed FeaturePython)
  n = 1
  ref = Nd_element
FEATURE [App::DocumentObjectGroupPython] G4_Nd  # scripted group (container) (typed FeaturePython)
  Dunit = g/cm3
  Dvalue = 6.9
  Group = -> [Nd_element001]
  conduct = 2
  density = 1
  expand = 3
  formula = Nd
  name = G4_Nd
  specific = 4
FEATURE [App::DocumentObjectGroupPython] Pm_element001  label="Pm_element : 1"  # scripted group (container) (typed FeaturePython)
  n = 1
  ref = Pm_element
FEATURE [App::DocumentObjectGroupPython] G4_Pm  # scripted group (container) (typed FeaturePython)
  Dunit = g/cm3
  Dvalue = 7.22
  Group = -> [Pm_element001]
  conduct = 2
  density = 1
  expand = 3
  formula = Pm
  name = G4_Pm
  specific = 4
FEATURE [App::DocumentObjectGroupPython] Sm_element001  label="Sm_element : 1"  # scripted group (container) (typed FeaturePython)
  n = 1
  ref = Sm_element
FEATURE [App::DocumentObjectGroupPython] G4_Sm  # scripted group (container) (typed FeaturePython)
  Dunit = g/cm3
  Dvalue = 7.46
  Group = -> [Sm_element001]
  conduct = 2
  density = 1
  expand = 3
  formula = Sm
  name = G4_Sm
  specific = 4
FEATURE [App::DocumentObjectGroupPython] Eu_element001  label="Eu_element : 1"  # scripted group (container) (typed FeaturePython)
  n = 1
  ref = Eu_element
FEATURE [App::DocumentObjectGroupPython] G4_Eu  # scripted group (container) (typed FeaturePython)
  Dunit = g/cm3
  Dvalue = 5.243
  Group = -> [Eu_element001]
  conduct = 2
  density = 1
  expand = 3
  formula = Eu
  name = G4_Eu
  specific = 4
FEATURE [App::DocumentObjectGroupPython] Gd_element002  label="Gd_element : 1"  # scripted group (container) (typed FeaturePython)
  n = 1
  ref = Gd_element
FEATURE [App::DocumentObjectGroupPython] G4_Gd  # scripted group (container) (typed FeaturePython)
  Dunit = g/cm3
  Dvalue = 7.9004
  Group = -> [Gd_element002]
  conduct = 2
  density = 1
  expand = 3
  formula = Gd
  name = G4_Gd
  specific = 4
FEATURE [App::DocumentObjectGroupPython] Tb_element001  label="Tb_element : 1"  # scripted group (container) (typed FeaturePython)
  n = 1
  ref = Tb_element
FEATURE [App::DocumentObjectGroupPython] G4_Tb  # scripted group (container) (typed FeaturePython)
  Dunit = g/cm3
  Dvalue = 8.229
  Group = -> [Tb_element001]
  conduct = 2
  density = 1
  expand = 3
  formula = Tb
  name = G4_Tb
  specific = 4
FEATURE [App::DocumentObjectGroupPython] Dy_element001  label="Dy_element : 1"  # scripted group (container) (typed FeaturePython)
  n = 1
  ref = Dy_element
FEATURE [App::DocumentObjectGroupPython] G4_Dy  # scripted group (container) (typed FeaturePython)
  Dunit = g/cm3
  Dvalue = 8.55
  Group = -> [Dy_element001]
  conduct = 2
  density = 1
  expand = 3
  formula = Dy
  name = G4_Dy
  specific = 4
FEATURE [App::DocumentObjectGroupPython] Ho_element001  label="Ho_element : 1"  # scripted group (container) (typed FeaturePython)
  n = 1
  ref = Ho_element
FEATURE [App::DocumentObjectGroupPython] G4_Ho  # scripted group (container) (typed FeaturePython)
  Dunit = g/cm3
  Dvalue = 8.795
  Group = -> [Ho_element001]
  conduct = 2
  density = 1
  expand = 3
  formula = Ho
  name = G4_Ho
  specific = 4
FEATURE [App::DocumentObjectGroupPython] Er_element001  label="Er_element : 1"  # scripted group (container) (typed FeaturePython)
  n = 1
  ref = Er_element
FEATURE [App::DocumentObjectGroupPython] G4_Er  # scripted group (container) (typed FeaturePython)
  Dunit = g/cm3
  Dvalue = 9.066
  Group = -> [Er_element001]
  conduct = 2
  density = 1
  expand = 3
  formula = Er
  name = G4_Er
  specific = 4
FEATURE [App::DocumentObjectGroupPython] Tm_element001  label="Tm_element : 1"  # scripted group (container) (typed FeaturePython)
  n = 1
  ref = Tm_element
FEATURE [App::DocumentObjectGroupPython] G4_Tm  # scripted group (container) (typed FeaturePython)
  Dunit = g/cm3
  Dvalue = 9.321
  Group = -> [Tm_element001]
  conduct = 2
  density = 1
  expand = 3
  formula = Tm
  name = G4_Tm
  specific = 4
FEATURE [App::DocumentObjectGroupPython] Yb_element001  label="Yb_element : 1"  # scripted group (container) (typed FeaturePython)
  n = 1
  ref = Yb_element
FEATURE [App::DocumentObjectGroupPython] G4_Yb  # scripted group (container) (typed FeaturePython)
  Dunit = g/cm3
  Dvalue = 6.73
  Group = -> [Yb_element001]
  conduct = 2
  density = 1
  expand = 3
  formula = Yb
  name = G4_Yb
  specific = 4
FEATURE [App::DocumentObjectGroupPython] Lu_element001  label="Lu_element : 1"  # scripted group (container) (typed FeaturePython)
  n = 1
  ref = Lu_element
FEATURE [App::DocumentObjectGroupPython] G4_Lu  # scripted group (container) (typed FeaturePython)
  Dunit = g/cm3
  Dvalue = 9.84
  Group = -> [Lu_element001]
  conduct = 2
  density = 1
  expand = 3
  formula = Lu
  name = G4_Lu
  specific = 4
FEATURE [App::DocumentObjectGroupPython] Hf_element001  label="Hf_element : 1"  # scripted group (container) (typed FeaturePython)
  n = 1
  ref = Hf_element
FEATURE [App::DocumentObjectGroupPython] G4_Hf  # scripted group (container) (typed FeaturePython)
  Dunit = g/cm3
  Dvalue = 13.31
  Group = -> [Hf_element001]
  conduct = 2
  density = 1
  expand = 3
  formula = Hf
  name = G4_Hf
  specific = 4
FEATURE [App::DocumentObjectGroupPython] Ta_element001  label="Ta_element : 1"  # scripted group (container) (typed FeaturePython)
  n = 1
  ref = Ta_element
FEATURE [App::DocumentObjectGroupPython] G4_Ta  # scripted group (container) (typed FeaturePython)
  Dunit = g/cm3
  Dvalue = 16.654
  Group = -> [Ta_element001]
  conduct = 2
  density = 1
  expand = 3
  formula = Ta
  name = G4_Ta
  specific = 4
FEATURE [App::DocumentObjectGroupPython] W_element004  label="W_element : 004"  # scripted group (container) (typed FeaturePython)
  n = 1
  ref = W_element
FEATURE [App::DocumentObjectGroupPython] G4_W  # scripted group (container) (typed FeaturePython)
  Dunit = g/cm3
  Dvalue = 19.3
  Group = -> [W_element004]
  conduct = 2
  density = 1
  expand = 3
  formula = W
  name = G4_W
  specific = 4
FEATURE [App::DocumentObjectGroupPython] Re_element001  label="Re_element : 1"  # scripted group (container) (typed FeaturePython)
  n = 1
  ref = Re_element
FEATURE [App::DocumentObjectGroupPython] G4_Re  # scripted group (container) (typed FeaturePython)
  Dunit = g/cm3
  Dvalue = 21.02
  Group = -> [Re_element001]
  conduct = 2
  density = 1
  expand = 3
  formula = Re
  name = G4_Re
  specific = 4
FEATURE [App::DocumentObjectGroupPython] Os_element001  label="Os_element : 1"  # scripted group (container) (typed FeaturePython)
  n = 1
  ref = Os_element
FEATURE [App::DocumentObjectGroupPython] G4_Os  # scripted group (container) (typed FeaturePython)
  Dunit = g/cm3
  Dvalue = 22.57
  Group = -> [Os_element001]
  conduct = 2
  density = 1
  expand = 3
  formula = Os
  name = G4_Os
  specific = 4
FEATURE [App::DocumentObjectGroupPython] Ir_element001  label="Ir_element : 1"  # scripted group (container) (typed FeaturePython)
  n = 1
  ref = Ir_element
FEATURE [App::DocumentObjectGroupPython] G4_Ir  # scripted group (container) (typed FeaturePython)
  Dunit = g/cm3
  Dvalue = 22.42
  Group = -> [Ir_element001]
  conduct = 2
  density = 1
  expand = 3
  formula = Ir
  name = G4_Ir
  specific = 4
FEATURE [App::DocumentObjectGroupPython] Pt_element001  label="Pt_element : 1"  # scripted group (container) (typed FeaturePython)
  n = 1
  ref = Pt_element
FEATURE [App::DocumentObjectGroupPython] G4_Pt  # scripted group (container) (typed FeaturePython)
  Dunit = g/cm3
  Dvalue = 21.45
  Group = -> [Pt_element001]
  conduct = 2
  density = 1
  expand = 3
  formula = Pt
  name = G4_Pt
  specific = 4
FEATURE [App::DocumentObjectGroupPython] Au_element001  label="Au_element : 1"  # scripted group (container) (typed FeaturePython)
  n = 1
  ref = Au_element
FEATURE [App::DocumentObjectGroupPython] G4_Au  # scripted group (container) (typed FeaturePython)
  Dunit = g/cm3
  Dvalue = 19.32
  Group = -> [Au_element001]
  conduct = 2
  density = 1
  expand = 3
  formula = Au
  name = G4_Au
  specific = 4
FEATURE [App::DocumentObjectGroupPython] Hg_element002  label="Hg_element : 002"  # scripted group (container) (typed FeaturePython)
  n = 1
  ref = Hg_element
FEATURE [App::DocumentObjectGroupPython] G4_Hg  # scripted group (container) (typed FeaturePython)
  Dunit = g/cm3
  Dvalue = 13.546
  Group = -> [Hg_element002]
  conduct = 2
  density = 1
  expand = 3
  formula = Hg
  name = G4_Hg
  specific = 4
FEATURE [App::DocumentObjectGroupPython] Tl_element002  label="Tl_element : 002"  # scripted group (container) (typed FeaturePython)
  n = 1
  ref = Tl_element
FEATURE [App::DocumentObjectGroupPython] G4_Tl  # scripted group (container) (typed FeaturePython)
  Dunit = g/cm3
  Dvalue = 11.72
  Group = -> [Tl_element002]
  conduct = 2
  density = 1
  expand = 3
  formula = Tl
  name = G4_Tl
  specific = 4
FEATURE [App::DocumentObjectGroupPython] Pb_element003  label="Pb_element : 1"  # scripted group (container) (typed FeaturePython)
  n = 1
  ref = Pb_element
FEATURE [App::DocumentObjectGroupPython] G4_Pb  # scripted group (container) (typed FeaturePython)
  Dunit = g/cm3
  Dvalue = 11.35
  Group = -> [Pb_element003]
  conduct = 2
  density = 1
  expand = 3
  formula = Pb
  name = G4_Pb
  specific = 4
FEATURE [App::DocumentObjectGroupPython] Bi_element002  label="Bi_element : 1"  # scripted group (container) (typed FeaturePython)
  n = 1
  ref = Bi_element
FEATURE [App::DocumentObjectGroupPython] G4_Bi  # scripted group (container) (typed FeaturePython)
  Dunit = g/cm3
  Dvalue = 9.747
  Group = -> [Bi_element002]
  conduct = 2
  density = 1
  expand = 3
  formula = Bi
  name = G4_Bi
  specific = 4
FEATURE [App::DocumentObjectGroupPython] Po_element001  label="Po_element : 1"  # scripted group (container) (typed FeaturePython)
  n = 1
  ref = Po_element
FEATURE [App::DocumentObjectGroupPython] G4_Po  # scripted group (container) (typed FeaturePython)
  Dunit = g/cm3
  Dvalue = 9.32
  Group = -> [Po_element001]
  conduct = 2
  density = 1
  expand = 3
  formula = Po
  name = G4_Po
  specific = 4
FEATURE [App::DocumentObjectGroupPython] At_element001  label="At_element : 1"  # scripted group (container) (typed FeaturePython)
  n = 1
  ref = At_element
FEATURE [App::DocumentObjectGroupPython] G4_At  # scripted group (container) (typed FeaturePython)
  Dunit = g/cm3
  Dvalue = 9.32
  Group = -> [At_element001]
  conduct = 2
  density = 1
  expand = 3
  formula = At
  name = G4_At
  specific = 4
FEATURE [App::DocumentObjectGroupPython] Rn_element001  label="Rn_element : 1"  # scripted group (container) (typed FeaturePython)
  n = 1
  ref = Rn_element
FEATURE [App::DocumentObjectGroupPython] G4_Rn  # scripted group (container) (typed FeaturePython)
  Dunit = g/cm3
  Dvalue = 0.00900662
  Group = -> [Rn_element001]
  conduct = 2
  density = 1
  expand = 3
  formula = Rn
  name = G4_Rn
  specific = 4
FEATURE [App::DocumentObjectGroupPython] Fr_element001  label="Fr_element : 1"  # scripted group (container) (typed FeaturePython)
  n = 1
  ref = Fr_element
FEATURE [App::DocumentObjectGroupPython] G4_Fr  # scripted group (container) (typed FeaturePython)
  Dunit = g/cm3
  Dvalue = 1
  Group = -> [Fr_element001]
  conduct = 2
  density = 1
  expand = 3
  formula = Fr
  name = G4_Fr
  specific = 4
FEATURE [App::DocumentObjectGroupPython] Ra_element001  label="Ra_element : 1"  # scripted group (container) (typed FeaturePython)
  n = 1
  ref = Ra_element
FEATURE [App::DocumentObjectGroupPython] G4_Ra  # scripted group (container) (typed FeaturePython)
  Dunit = g/cm3
  Dvalue = 5
  Group = -> [Ra_element001]
  conduct = 2
  density = 1
  expand = 3
  formula = Ra
  name = G4_Ra
  specific = 4
FEATURE [App::DocumentObjectGroupPython] Ac_element001  label="Ac_element : 1"  # scripted group (container) (typed FeaturePython)
  n = 1
  ref = Ac_element
FEATURE [App::DocumentObjectGroupPython] G4_Ac  # scripted group (container) (typed FeaturePython)
  Dunit = g/cm3
  Dvalue = 10.07
  Group = -> [Ac_element001]
  conduct = 2
  density = 1
  expand = 3
  formula = Ac
  name = G4_Ac
  specific = 4
FEATURE [App::DocumentObjectGroupPython] Th_element001  label="Th_element : 1"  # scripted group (container) (typed FeaturePython)
  n = 1
  ref = Th_element
FEATURE [App::DocumentObjectGroupPython] G4_Th  # scripted group (container) (typed FeaturePython)
  Dunit = g/cm3
  Dvalue = 11.72
  Group = -> [Th_element001]
  conduct = 2
  density = 1
  expand = 3
  formula = Th
  name = G4_Th
  specific = 4
FEATURE [App::DocumentObjectGroupPython] Pa_element001  label="Pa_element : 1"  # scripted group (container) (typed FeaturePython)
  n = 1
  ref = Pa_element
FEATURE [App::DocumentObjectGroupPython] G4_Pa  # scripted group (container) (typed FeaturePython)
  Dunit = g/cm3
  Dvalue = 15.37
  Group = -> [Pa_element001]
  conduct = 2
  density = 1
  expand = 3
  formula = Pa
  name = G4_Pa
  specific = 4
FEATURE [App::DocumentObjectGroupPython] U_element004  label="U_element : 004"  # scripted group (container) (typed FeaturePython)
  n = 1
  ref = U_element
FEATURE [App::DocumentObjectGroupPython] G4_U  # scripted group (container) (typed FeaturePython)
  Dunit = g/cm3
  Dvalue = 18.95
  Group = -> [U_element004]
  conduct = 2
  density = 1
  expand = 3
  formula = U
  name = G4_U
  specific = 4
FEATURE [App::DocumentObjectGroupPython] Np_element001  label="Np_element : 1"  # scripted group (container) (typed FeaturePython)
  n = 1
  ref = Np_element
FEATURE [App::DocumentObjectGroupPython] G4_Np  # scripted group (container) (typed FeaturePython)
  Dunit = g/cm3
  Dvalue = 20.25
  Group = -> [Np_element001]
  conduct = 2
  density = 1
  expand = 3
  formula = Np
  name = G4_Np
  specific = 4
FEATURE [App::DocumentObjectGroupPython] Pu_element002  label="Pu_element : 002"  # scripted group (container) (typed FeaturePython)
  n = 1
  ref = Pu_element
FEATURE [App::DocumentObjectGroupPython] G4_Pu  # scripted group (container) (typed FeaturePython)
  Dunit = g/cm3
  Dvalue = 19.84
  Group = -> [Pu_element002]
  conduct = 2
  density = 1
  expand = 3
  formula = Pu
  name = G4_Pu
  specific = 4
FEATURE [App::DocumentObjectGroupPython] Am_element001  label="Am_element : 1"  # scripted group (container) (typed FeaturePython)
  n = 1
  ref = Am_element
FEATURE [App::DocumentObjectGroupPython] G4_Am  # scripted group (container) (typed FeaturePython)
  Dunit = g/cm3
  Dvalue = 13.67
  Group = -> [Am_element001]
  conduct = 2
  density = 1
  expand = 3
  formula = Am
  name = G4_Am
  specific = 4
FEATURE [App::DocumentObjectGroupPython] Cm_element001  label="Cm_element : 1"  # scripted group (container) (typed FeaturePython)
  n = 1
  ref = Cm_element
FEATURE [App::DocumentObjectGroupPython] G4_Cm  # scripted group (container) (typed FeaturePython)
  Dunit = g/cm3
  Dvalue = 13.51
  Group = -> [Cm_element001]
  conduct = 2
  density = 1
  expand = 3
  formula = Cm
  name = G4_Cm
  specific = 4
FEATURE [App::DocumentObjectGroupPython] Bk_element001  label="Bk_element : 1"  # scripted group (container) (typed FeaturePython)
  n = 1
  ref = Bk_element
FEATURE [App::DocumentObjectGroupPython] G4_Bk  # scripted group (container) (typed FeaturePython)
  Dunit = g/cm3
  Dvalue = 14
  Group = -> [Bk_element001]
  conduct = 2
  density = 1
  expand = 3
  formula = Bk
  name = G4_Bk
  specific = 4
FEATURE [App::DocumentObjectGroupPython] Cf_element001  label="Cf_element : 1"  # scripted group (container) (typed FeaturePython)
  n = 1
  ref = Cf_element
FEATURE [App::DocumentObjectGroupPython] G4_Cf  # scripted group (container) (typed FeaturePython)
  Dunit = g/cm3
  Dvalue = 10
  Group = -> [Cf_element001]
  conduct = 2
  density = 1
  expand = 3
  formula = Cf
  name = G4_Cf
  specific = 4
FEATURE [App::DocumentObjectGroupPython] Element  # scripted group (container) (typed FeaturePython)
  Group = -> [G4_H,G4_He,G4_Li,G4_Be,G4_B,G4_C,G4_N,G4_O,G4_F,G4_Ne,G4_Na,G4_Mg,G4_Al,G4_Si,G4_P,G4_S,G4_Cl,G4_Ar,G4_K,G4_Ca,G4_Sc,G4_Ti,G4_V,G4_Cr,G4_Mn,G4_Fe,G4_Co,G4_Ni,G4_Cu,G4_Zn,G4_Ga,G4_Ge,G4_As,G4_Se,G4_Br,G4_Kr,G4_Rb,G4_Sr,G4_Y,G4_Zr,G4_Nb,G4_Mo,G4_Tc,G4_Ru,G4_Rh,G4_Pd,G4_Ag,G4_Cd,G4_In,G4_Sn,G4_Sb,G4_Te,G4_I,G4_Xe,G4_Cs,G4_Ba,G4_La,G4_Ce,G4_Pr,G4_Nd,G4_Pm,G4_Sm,G4_Eu,G4_Gd,G4_Tb,G4_Dy,G4_Ho,G4_Er,+30 more]
FEATURE [App::DocumentObjectGroupPython] H_element114  label="H_element : 063"  # scripted group (container) (typed FeaturePython)
  n = 2
  ref = H_element
FEATURE [App::DocumentObjectGroupPython] G4_lH2  # scripted group (container) (typed FeaturePython)
  Dunit = g/cm3
  Dvalue = 0.0708
  Group = -> [H_element114]
  conduct = 2
  density = 1
  expand = 3
  formula = G4_lH2
  name = G4_lH2
  specific = 4
FEATURE [App::DocumentObjectGroupPython] N_element049  label="N_element : 022"  # scripted group (container) (typed FeaturePython)
  n = 2
  ref = N_element
FEATURE [App::DocumentObjectGroupPython] G4_lN2  # scripted group (container) (typed FeaturePython)
  Dunit = g/cm3
  Dvalue = 0.807
  Group = -> [N_element049]
  conduct = 2
  density = 1
  expand = 3
  formula = G4_lN2
  name = G4_lN2
  specific = 4
FEATURE [App::DocumentObjectGroupPython] O_element106  label="O_element : 060"  # scripted group (container) (typed FeaturePython)
  n = 2
  ref = O_element
FEATURE [App::DocumentObjectGroupPython] G4_lO2  # scripted group (container) (typed FeaturePython)
  Dunit = g/cm3
  Dvalue = 1.141
  Group = -> [O_element106]
  conduct = 2
  density = 1
  expand = 3
  formula = G4_lO2
  name = G4_lO2
  specific = 4
FEATURE [App::DocumentObjectGroupPython] Ar  label="Ar : 1"  # scripted group (container) (typed FeaturePython)
  n = 1
  ref = Ar
FEATURE [App::DocumentObjectGroupPython] G4_lAr  # scripted group (container) (typed FeaturePython)
  Dunit = g/cm3
  Dvalue = 1.396
  Group = -> [Ar]
  conduct = 2
  density = 1
  expand = 3
  formula = G4_lAr
  name = G4_lAr
  specific = 4
FEATURE [App::DocumentObjectGroupPython] Br  label="Br : 1"  # scripted group (container) (typed FeaturePython)
  n = 1
  ref = Br
FEATURE [App::DocumentObjectGroupPython] G4_lBr  # scripted group (container) (typed FeaturePython)
  Dunit = g/cm3
  Dvalue = 3.1028
  Group = -> [Br]
  conduct = 2
  density = 1
  expand = 3
  formula = G4_lBr
  name = G4_lBr
  specific = 4
FEATURE [App::DocumentObjectGroupPython] Kr  label="Kr : 1"  # scripted group (container) (typed FeaturePython)
  n = 1
  ref = Kr
FEATURE [App::DocumentObjectGroupPython] G4_lKr  # scripted group (container) (typed FeaturePython)
  Dunit = g/cm3
  Dvalue = 2.418
  Group = -> [Kr]
  conduct = 2
  density = 1
  expand = 3
  formula = G4_lKr
  name = G4_lKr
  specific = 4
FEATURE [App::DocumentObjectGroupPython] Xe  label="Xe : 1"  # scripted group (container) (typed FeaturePython)
  n = 1
  ref = Xe
FEATURE [App::DocumentObjectGroupPython] G4_lXe  # scripted group (container) (typed FeaturePython)
  Dunit = g/cm3
  Dvalue = 2.953
  Group = -> [Xe]
  conduct = 2
  density = 1
  expand = 3
  formula = G4_lXe
  name = G4_lXe
  specific = 4
FEATURE [App::DocumentObjectGroupPython] O_element107  label="O_element : 061"  # scripted group (container) (typed FeaturePython)
  n = 4
  ref = O_element
FEATURE [App::DocumentObjectGroupPython] Pb_element004  label="Pb_element : 002"  # scripted group (container) (typed FeaturePython)
  n = 1
  ref = Pb_element
FEATURE [App::DocumentObjectGroupPython] W_element005  label="W_element : 005"  # scripted group (container) (typed FeaturePython)
  n = 1
  ref = W_element
FEATURE [App::DocumentObjectGroupPython] G4_PbWO4  # scripted group (container) (typed FeaturePython)
  Dunit = g/cm3
  Dvalue = 8.28
  Group = -> [O_element107,Pb_element004,W_element005]
  conduct = 2
  density = 1
  expand = 3
  formula = G4_PbWO4
  name = G4_PbWO4
  specific = 4
FEATURE [App::DocumentObjectGroupPython] alactic  label="alactic : 1"  # scripted group (container) (typed FeaturePython)
  n = 1
  ref = alactic
FEATURE [App::DocumentObjectGroupPython] G4_Galactic  # scripted group (container) (typed FeaturePython)
  Dunit = g/cm3
  Dvalue = 0
  Group = -> [alactic]
  conduct = 2
  density = 1
  expand = 3
  formula = G4_Galactic
  name = G4_Galactic
  specific = 4
FEATURE [App::DocumentObjectGroupPython] RAPHITE_POROUS  label="RAPHITE_POROUS : 1"  # scripted group (container) (typed FeaturePython)
  n = 1
  ref = RAPHITE_POROUS
FEATURE [App::DocumentObjectGroupPython] G4_GRAPHITE_POROUS  # scripted group (container) (typed FeaturePython)
  Dunit = g/cm3
  Dvalue = 1.7
  Group = -> [RAPHITE_POROUS]
  conduct = 2
  density = 1
  expand = 3
  formula = G4_GRAPHITE_POROUS
  name = G4_GRAPHITE_POROUS
  specific = 4
FEATURE [App::DocumentObjectGroupPython] H_element115  label="H_element : 0.150"  # scripted group (container) (typed FeaturePython)
  n = 0.080538
FEATURE [App::DocumentObjectGroupPython] C_element125  label="C_element : 0.600"  # scripted group (container) (typed FeaturePython)
  n = 0.599848
FEATURE [App::DocumentObjectGroupPython] O_element108  label="O_element : 0.320"  # scripted group (container) (typed FeaturePython)
  n = 0.319614
FEATURE [App::DocumentObjectGroupPython] G4_LUCITE  # scripted group (container) (typed FeaturePython)
  Dunit = g/cm3
  Dvalue = 1.19
  Group = -> [H_element115,C_element125,O_element108]
  conduct = 2
  density = 1
  expand = 3
  formula = G4_LUCITE
  name = G4_LUCITE
  specific = 4
FEATURE [App::DocumentObjectGroupPython] Cu_element002  label="Cu_element : 62"  # scripted group (container) (typed FeaturePython)
  n = 62
  ref = Cu_element
FEATURE [App::DocumentObjectGroupPython] Zn_element002  label="Zn_element : 35"  # scripted group (container) (typed FeaturePython)
  n = 35
  ref = Zn_element
FEATURE [App::DocumentObjectGroupPython] Pb_element005  label="Pb_element : 3"  # scripted group (container) (typed FeaturePython)
  n = 3
  ref = Pb_element
FEATURE [App::DocumentObjectGroupPython] G4_BRASS  # scripted group (container) (typed FeaturePython)
  Dunit = g/cm3
  Dvalue = 8.52
  Group = -> [Cu_element002,Zn_element002,Pb_element005]
  conduct = 2
  density = 1
  expand = 3
  formula = G4_BRASS
  name = G4_BRASS
  specific = 4
FEATURE [App::DocumentObjectGroupPython] Cu_element003  label="Cu_element : 89"  # scripted group (container) (typed FeaturePython)
  n = 89
  ref = Cu_element
FEATURE [App::DocumentObjectGroupPython] Zn_element003  label="Zn_element : 9"  # scripted group (container) (typed FeaturePython)
  n = 9
  ref = Zn_element
FEATURE [App::DocumentObjectGroupPython] Pb_element006  label="Pb_element : 2"  # scripted group (container) (typed FeaturePython)
  n = 2
  ref = Pb_element
FEATURE [App::DocumentObjectGroupPython] G4_BRONZE  # scripted group (container) (typed FeaturePython)
  Dunit = g/cm3
  Dvalue = 8.82
  Group = -> [Cu_element003,Zn_element003,Pb_element006]
  conduct = 2
  density = 1
  expand = 3
  formula = G4_BRONZE
  name = G4_BRONZE
  specific = 4
FEATURE [App::DocumentObjectGroupPython] Fe_element008  label="Fe_element : 74"  # scripted group (container) (typed FeaturePython)
  n = 74
  ref = Fe_element
FEATURE [App::DocumentObjectGroupPython] Cr_element002  label="Cr_element : 18"  # scripted group (container) (typed FeaturePython)
  n = 18
  ref = Cr_element
FEATURE [App::DocumentObjectGroupPython] Ni_element002  label="Ni_element : 8"  # scripted group (container) (typed FeaturePython)
  n = 8
  ref = Ni_element
FEATURE [App::DocumentObjectGroupPython] G4_STAINLESS_STEEL  label="G4_STAINLESS-STEEL"  # scripted group (container) (typed FeaturePython)
  Dunit = g/cm3
  Dvalue = 8
  Group = -> [Fe_element008,Cr_element002,Ni_element002]
  conduct = 2
  density = 1
  expand = 3
  formula = G4_STAINLESS-STEEL
  name = G4_STAINLESS-STEEL
  specific = 4
FEATURE [App::DocumentObjectGroupPython] H_element116  label="H_element : 064"  # scripted group (container) (typed FeaturePython)
  n = 18
  ref = H_element
FEATURE [App::DocumentObjectGroupPython] C_element126  label="C_element : 071"  # scripted group (container) (typed FeaturePython)
  n = 12
  ref = C_element
FEATURE [App::DocumentObjectGroupPython] O_element109  label="O_element : 062"  # scripted group (container) (typed FeaturePython)
  n = 7
  ref = O_element
FEATURE [App::DocumentObjectGroupPython] G4_CR39  # scripted group (container) (typed FeaturePython)
  Dunit = g/cm3
  Dvalue = 1.32
  Group = -> [H_element116,C_element126,O_element109]
  conduct = 2
  density = 1
  expand = 3
  formula = G4_CR39
  name = G4_CR39
  specific = 4
FEATURE [App::DocumentObjectGroupPython] H_element117  label="H_element : 38"  # scripted group (container) (typed FeaturePython)
  n = 38
  ref = H_element
FEATURE [App::DocumentObjectGroupPython] C_element127  label="C_element : 072"  # scripted group (container) (typed FeaturePython)
  n = 18
  ref = C_element
FEATURE [App::DocumentObjectGroupPython] O_element110  label="O_element : 063"  # scripted group (container) (typed FeaturePython)
  n = 1
  ref = O_element
FEATURE [App::DocumentObjectGroupPython] G4_OCTADECANOL  # scripted group (container) (typed FeaturePython)
  Dunit = g/cm3
  Dvalue = 0.812
  Group = -> [H_element117,C_element127,O_element110]
  conduct = 2
  density = 1
  expand = 3
  formula = G4_OCTADECANOL
  name = G4_OCTADECANOL
  specific = 4
FEATURE [App::DocumentObjectGroupPython] HEP  # scripted group (container) (typed FeaturePython)
  Group = -> [G4_lH2,G4_lN2,G4_lO2,G4_lAr,G4_lBr,G4_lKr,G4_lXe,G4_PbWO4,G4_Galactic,G4_GRAPHITE_POROUS,G4_LUCITE,G4_BRASS,G4_BRONZE,G4_STAINLESS_STEEL,G4_CR39,G4_OCTADECANOL]
FEATURE [App::DocumentObjectGroupPython] C_element128  label="C_element : 073"  # scripted group (container) (typed FeaturePython)
  n = 14
  ref = C_element
FEATURE [App::DocumentObjectGroupPython] H_element118  label="H_element : 065"  # scripted group (container) (typed FeaturePython)
  n = 10
  ref = H_element
FEATURE [App::DocumentObjectGroupPython] O_element111  label="O_element : 064"  # scripted group (container) (typed FeaturePython)
  n = 2
  ref = O_element
FEATURE [App::DocumentObjectGroupPython] N_element050  label="N_element : 023"  # scripted group (container) (typed FeaturePython)
  n = 2
  ref = N_element
FEATURE [App::DocumentObjectGroupPython] G4_KEVLAR  # scripted group (container) (typed FeaturePython)
  Dunit = g/cm3
  Dvalue = 1.44
  Group = -> [C_element128,H_element118,O_element111,N_element050]
  conduct = 2
  density = 1
  expand = 3
  formula = G4_KEVLAR
  name = G4_KEVLAR
  specific = 4
FEATURE [App::DocumentObjectGroupPython] C_element129  label="C_element : 074"  # scripted group (container) (typed FeaturePython)
  n = 10
  ref = C_element
FEATURE [App::DocumentObjectGroupPython] H_element119  label="H_element : 066"  # scripted group (container) (typed FeaturePython)
  n = 8
  ref = H_element
FEATURE [App::DocumentObjectGroupPython] O_element112  label="O_element : 065"  # scripted group (container) (typed FeaturePython)
  n = 4
  ref = O_element
FEATURE [App::DocumentObjectGroupPython] G4_DACRON  # scripted group (container) (typed FeaturePython)
  Dunit = g/cm3
  Dvalue = 1.4
  Group = -> [C_element129,H_element119,O_element112]
  conduct = 2
  density = 1
  expand = 3
  formula = G4_DACRON
  name = G4_DACRON
  specific = 4
FEATURE [App::DocumentObjectGroupPython] C_element130  label="C_element : 075"  # scripted group (container) (typed FeaturePython)
  n = 4
  ref = C_element
FEATURE [App::DocumentObjectGroupPython] H_element120  label="H_element : 067"  # scripted group (container) (typed FeaturePython)
  n = 5
  ref = H_element
FEATURE [App::DocumentObjectGroupPython] Cl_element030  label="Cl_element : 016"  # scripted group (container) (typed FeaturePython)
  n = 1
  ref = Cl_element
FEATURE [App::DocumentObjectGroupPython] G4_NEOPRENE  # scripted group (container) (typed FeaturePython)
  Dunit = g/cm3
  Dvalue = 1.23
  Group = -> [C_element130,H_element120,Cl_element030]
  conduct = 2
  density = 1
  expand = 3
  formula = G4_NEOPRENE
  name = G4_NEOPRENE
  specific = 4
FEATURE [App::DocumentObjectGroupPython] Space  # scripted group (container) (typed FeaturePython)
  Group = -> [G4_KEVLAR,G4_DACRON,G4_NEOPRENE]
FEATURE [App::DocumentObjectGroupPython] H_element121  label="H_element : 068"  # scripted group (container) (typed FeaturePython)
  n = 5
  ref = H_element
FEATURE [App::DocumentObjectGroupPython] C_element131  label="C_element : 076"  # scripted group (container) (typed FeaturePython)
  n = 4
  ref = C_element
FEATURE [App::DocumentObjectGroupPython] N_element051  label="N_element : 3"  # scripted group (container) (typed FeaturePython)
  n = 3
  ref = N_element
FEATURE [App::DocumentObjectGroupPython] O_element113  label="O_element : 066"  # scripted group (container) (typed FeaturePython)
  n = 1
  ref = O_element
FEATURE [App::DocumentObjectGroupPython] G4_CYTOSINE  # scripted group (container) (typed FeaturePython)
  Dunit = g/cm3
  Dvalue = 1.55
  Group = -> [H_element121,C_element131,N_element051,O_element113]
  conduct = 2
  density = 1
  expand = 3
  formula = G4_CYTOSINE
  name = G4_CYTOSINE
  specific = 4
FEATURE [App::DocumentObjectGroupPython] H_element122  label="H_element : 069"  # scripted group (container) (typed FeaturePython)
  n = 6
  ref = H_element
FEATURE [App::DocumentObjectGroupPython] C_element132  label="C_element : 077"  # scripted group (container) (typed FeaturePython)
  n = 5
  ref = C_element
FEATURE [App::DocumentObjectGroupPython] N_element052  label="N_element : 024"  # scripted group (container) (typed FeaturePython)
  n = 2
  ref = N_element
FEATURE [App::DocumentObjectGroupPython] O_element114  label="O_element : 067"  # scripted group (container) (typed FeaturePython)
  n = 2
  ref = O_element
FEATURE [App::DocumentObjectGroupPython] G4_THYMINE  # scripted group (container) (typed FeaturePython)
  Dunit = g/cm3
  Dvalue = 1.23
  Group = -> [H_element122,C_element132,N_element052,O_element114]
  conduct = 2
  density = 1
  expand = 3
  formula = G4_THYMINE
  name = G4_THYMINE
  specific = 4
FEATURE [App::DocumentObjectGroupPython] H_element123  label="H_element : 070"  # scripted group (container) (typed FeaturePython)
  n = 4
  ref = H_element
FEATURE [App::DocumentObjectGroupPython] C_element133  label="C_element : 078"  # scripted group (container) (typed FeaturePython)
  n = 4
  ref = C_element
FEATURE [App::DocumentObjectGroupPython] N_element053  label="N_element : 025"  # scripted group (container) (typed FeaturePython)
  n = 2
  ref = N_element
FEATURE [App::DocumentObjectGroupPython] O_element115  label="O_element : 068"  # scripted group (container) (typed FeaturePython)
  n = 2
  ref = O_element
FEATURE [App::DocumentObjectGroupPython] G4_URACIL  # scripted group (container) (typed FeaturePython)
  Dunit = g/cm3
  Dvalue = 1.32
  Group = -> [H_element123,C_element133,N_element053,O_element115]
  conduct = 2
  density = 1
  expand = 3
  formula = G4_URACIL
  name = G4_URACIL
  specific = 4
FEATURE [App::DocumentObjectGroupPython] H_element124  label="H_element : 071"  # scripted group (container) (typed FeaturePython)
  n = 4
  ref = H_element
FEATURE [App::DocumentObjectGroupPython] C_element134  label="C_element : 079"  # scripted group (container) (typed FeaturePython)
  n = 5
  ref = C_element
FEATURE [App::DocumentObjectGroupPython] N_element054  label="N_element : 026"  # scripted group (container) (typed FeaturePython)
  n = 5
  ref = N_element
FEATURE [App::DocumentObjectGroupPython] G4_DNA_ADENINE  # scripted group (container) (typed FeaturePython)
  Dunit = g/cm3
  Dvalue = 1
  Group = -> [H_element124,C_element134,N_element054]
  conduct = 2
  density = 1
  expand = 3
  formula = G4_DNA_ADENINE
  name = G4_DNA_ADENINE
  specific = 4
FEATURE [App::DocumentObjectGroupPython] H_element125  label="H_element : 072"  # scripted group (container) (typed FeaturePython)
  n = 4
  ref = H_element
FEATURE [App::DocumentObjectGroupPython] C_element135  label="C_element : 080"  # scripted group (container) (typed FeaturePython)
  n = 5
  ref = C_element
FEATURE [App::DocumentObjectGroupPython] N_element055  label="N_element : 027"  # scripted group (container) (typed FeaturePython)
  n = 5
  ref = N_element
FEATURE [App::DocumentObjectGroupPython] O_element116  label="O_element : 069"  # scripted group (container) (typed FeaturePython)
  n = 1
  ref = O_element
FEATURE [App::DocumentObjectGroupPython] G4_DNA_GUANINE  # scripted group (container) (typed FeaturePython)
  Dunit = g/cm3
  Dvalue = 1
  Group = -> [H_element125,C_element135,N_element055,O_element116]
  conduct = 2
  density = 1
  expand = 3
  formula = G4_DNA_GUANINE
  name = G4_DNA_GUANINE
  specific = 4
FEATURE [App::DocumentObjectGroupPython] H_element126  label="H_element : 073"  # scripted group (container) (typed FeaturePython)
  n = 4
  ref = H_element
FEATURE [App::DocumentObjectGroupPython] C_element136  label="C_element : 081"  # scripted group (container) (typed FeaturePython)
  n = 4
  ref = C_element
FEATURE [App::DocumentObjectGroupPython] N_element056  label="N_element : 028"  # scripted group (container) (typed FeaturePython)
  n = 3
  ref = N_element
FEATURE [App::DocumentObjectGroupPython] O_element117  label="O_element : 070"  # scripted group (container) (typed FeaturePython)
  n = 1
  ref = O_element
FEATURE [App::DocumentObjectGroupPython] G4_DNA_CYTOSINE  # scripted group (container) (typed FeaturePython)
  Dunit = g/cm3
  Dvalue = 1
  Group = -> [H_element126,C_element136,N_element056,O_element117]
  conduct = 2
  density = 1
  expand = 3
  formula = G4_DNA_CYTOSINE
  name = G4_DNA_CYTOSINE
  specific = 4
FEATURE [App::DocumentObjectGroupPython] H_element127  label="H_element : 074"  # scripted group (container) (typed FeaturePython)
  n = 5
  ref = H_element
FEATURE [App::DocumentObjectGroupPython] C_element137  label="C_element : 082"  # scripted group (container) (typed FeaturePython)
  n = 5
  ref = C_element
FEATURE [App::DocumentObjectGroupPython] N_element057  label="N_element : 029"  # scripted group (container) (typed FeaturePython)
  n = 2
  ref = N_element
FEATURE [App::DocumentObjectGroupPython] O_element118  label="O_element : 071"  # scripted group (container) (typed FeaturePython)
  n = 2
  ref = O_element
FEATURE [App::DocumentObjectGroupPython] G4_DNA_THYMINE  # scripted group (container) (typed FeaturePython)
  Dunit = g/cm3
  Dvalue = 1
  Group = -> [H_element127,C_element137,N_element057,O_element118]
  conduct = 2
  density = 1
  expand = 3
  formula = G4_DNA_THYMINE
  name = G4_DNA_THYMINE
  specific = 4
FEATURE [App::DocumentObjectGroupPython] H_element128  label="H_element : 075"  # scripted group (container) (typed FeaturePython)
  n = 3
  ref = H_element
FEATURE [App::DocumentObjectGroupPython] C_element138  label="C_element : 083"  # scripted group (container) (typed FeaturePython)
  n = 4
  ref = C_element
FEATURE [App::DocumentObjectGroupPython] N_element058  label="N_element : 030"  # scripted group (container) (typed FeaturePython)
  n = 2
  ref = N_element
FEATURE [App::DocumentObjectGroupPython] O_element119  label="O_element : 072"  # scripted group (container) (typed FeaturePython)
  n = 2
  ref = O_element
FEATURE [App::DocumentObjectGroupPython] G4_DNA_URACIL  # scripted group (container) (typed FeaturePython)
  Dunit = g/cm3
  Dvalue = 1
  Group = -> [H_element128,C_element138,N_element058,O_element119]
  conduct = 2
  density = 1
  expand = 3
  formula = G4_DNA_URACIL
  name = G4_DNA_URACIL
  specific = 4
FEATURE [App::DocumentObjectGroupPython] H_element129  label="H_element : 076"  # scripted group (container) (typed FeaturePython)
  n = 10
  ref = H_element
FEATURE [App::DocumentObjectGroupPython] C_element139  label="C_element : 084"  # scripted group (container) (typed FeaturePython)
  n = 10
  ref = C_element
FEATURE [App::DocumentObjectGroupPython] N_element059  label="N_element : 031"  # scripted group (container) (typed FeaturePython)
  n = 5
  ref = N_element
FEATURE [App::DocumentObjectGroupPython] O_element120  label="O_element : 073"  # scripted group (container) (typed FeaturePython)
  n = 4
  ref = O_element
FEATURE [App::DocumentObjectGroupPython] G4_DNA_ADENOSINE  # scripted group (container) (typed FeaturePython)
  Dunit = g/cm3
  Dvalue = 1
  Group = -> [H_element129,C_element139,N_element059,O_element120]
  conduct = 2
  density = 1
  expand = 3
  formula = G4_DNA_ADENOSINE
  name = G4_DNA_ADENOSINE
  specific = 4
FEATURE [App::DocumentObjectGroupPython] H_element130  label="H_element : 077"  # scripted group (container) (typed FeaturePython)
  n = 10
  ref = H_element
FEATURE [App::DocumentObjectGroupPython] C_element140  label="C_element : 085"  # scripted group (container) (typed FeaturePython)
  n = 10
  ref = C_element
FEATURE [App::DocumentObjectGroupPython] N_element060  label="N_element : 032"  # scripted group (container) (typed FeaturePython)
  n = 5
  ref = N_element
FEATURE [App::DocumentObjectGroupPython] O_element121  label="O_element : 074"  # scripted group (container) (typed FeaturePython)
  n = 5
  ref = O_element
FEATURE [App::DocumentObjectGroupPython] G4_DNA_GUANOSINE  # scripted group (container) (typed FeaturePython)
  Dunit = g/cm3
  Dvalue = 1
  Group = -> [H_element130,C_element140,N_element060,O_element121]
  conduct = 2
  density = 1
  expand = 3
  formula = G4_DNA_GUANOSINE
  name = G4_DNA_GUANOSINE
  specific = 4
FEATURE [App::DocumentObjectGroupPython] H_element131  label="H_element : 078"  # scripted group (container) (typed FeaturePython)
  n = 10
  ref = H_element
FEATURE [App::DocumentObjectGroupPython] C_element141  label="C_element : 086"  # scripted group (container) (typed FeaturePython)
  n = 9
  ref = C_element
FEATURE [App::DocumentObjectGroupPython] N_element061  label="N_element : 033"  # scripted group (container) (typed FeaturePython)
  n = 3
  ref = N_element
FEATURE [App::DocumentObjectGroupPython] O_element122  label="O_element : 075"  # scripted group (container) (typed FeaturePython)
  n = 5
  ref = O_element
FEATURE [App::DocumentObjectGroupPython] G4_DNA_CYTIDINE  # scripted group (container) (typed FeaturePython)
  Dunit = g/cm3
  Dvalue = 1
  Group = -> [H_element131,C_element141,N_element061,O_element122]
  conduct = 2
  density = 1
  expand = 3
  formula = G4_DNA_CYTIDINE
  name = G4_DNA_CYTIDINE
  specific = 4
FEATURE [App::DocumentObjectGroupPython] H_element132  label="H_element : 079"  # scripted group (container) (typed FeaturePython)
  n = 9
  ref = H_element
FEATURE [App::DocumentObjectGroupPython] C_element142  label="C_element : 087"  # scripted group (container) (typed FeaturePython)
  n = 9
  ref = C_element
FEATURE [App::DocumentObjectGroupPython] N_element062  label="N_element : 034"  # scripted group (container) (typed FeaturePython)
  n = 2
  ref = N_element
FEATURE [App::DocumentObjectGroupPython] O_element123  label="O_element : 076"  # scripted group (container) (typed FeaturePython)
  n = 6
  ref = O_element
FEATURE [App::DocumentObjectGroupPython] G4_DNA_URIDINE  # scripted group (container) (typed FeaturePython)
  Dunit = g/cm3
  Dvalue = 1
  Group = -> [H_element132,C_element142,N_element062,O_element123]
  conduct = 2
  density = 1
  expand = 3
  formula = G4_DNA_URIDINE
  name = G4_DNA_URIDINE
  specific = 4
FEATURE [App::DocumentObjectGroupPython] H_element133  label="H_element : 080"  # scripted group (container) (typed FeaturePython)
  n = 11
  ref = H_element
FEATURE [App::DocumentObjectGroupPython] C_element143  label="C_element : 088"  # scripted group (container) (typed FeaturePython)
  n = 10
  ref = C_element
FEATURE [App::DocumentObjectGroupPython] N_element063  label="N_element : 035"  # scripted group (container) (typed FeaturePython)
  n = 2
  ref = N_element
FEATURE [App::DocumentObjectGroupPython] O_element124  label="O_element : 077"  # scripted group (container) (typed FeaturePython)
  n = 6
  ref = O_element
FEATURE [App::DocumentObjectGroupPython] G4_DNA_METHYLURIDINE  # scripted group (container) (typed FeaturePython)
  Dunit = g/cm3
  Dvalue = 1
  Group = -> [H_element133,C_element143,N_element063,O_element124]
  conduct = 2
  density = 1
  expand = 3
  formula = G4_DNA_METHYLURIDINE
  name = G4_DNA_METHYLURIDINE
  specific = 4
FEATURE [App::DocumentObjectGroupPython] P_element014  label="P_element : 003"  # scripted group (container) (typed FeaturePython)
  n = 1
  ref = P_element
FEATURE [App::DocumentObjectGroupPython] O_element125  label="O_element : 078"  # scripted group (container) (typed FeaturePython)
  n = 3
  ref = O_element
FEATURE [App::DocumentObjectGroupPython] G4_DNA_MONOPHOSPHATE  # scripted group (container) (typed FeaturePython)
  Dunit = g/cm3
  Dvalue = 1
  Group = -> [P_element014,O_element125]
  conduct = 2
  density = 1
  expand = 3
  formula = G4_DNA_MONOPHOSPHATE
  name = G4_DNA_MONOPHOSPHATE
  specific = 4
FEATURE [App::DocumentObjectGroupPython] H_element134  label="H_element : 081"  # scripted group (container) (typed FeaturePython)
  n = 10
  ref = H_element
FEATURE [App::DocumentObjectGroupPython] C_element144  label="C_element : 089"  # scripted group (container) (typed FeaturePython)
  n = 10
  ref = C_element
FEATURE [App::DocumentObjectGroupPython] N_element064  label="N_element : 036"  # scripted group (container) (typed FeaturePython)
  n = 5
  ref = N_element
FEATURE [App::DocumentObjectGroupPython] O_element126  label="O_element : 079"  # scripted group (container) (typed FeaturePython)
  n = 7
  ref = O_element
FEATURE [App::DocumentObjectGroupPython] P_element015  label="P_element : 004"  # scripted group (container) (typed FeaturePython)
  n = 1
  ref = P_element
FEATURE [App::DocumentObjectGroupPython] G4_DNA_A  # scripted group (container) (typed FeaturePython)
  Dunit = g/cm3
  Dvalue = 1
  Group = -> [H_element134,C_element144,N_element064,O_element126,P_element015]
  conduct = 2
  density = 1
  expand = 3
  formula = G4_DNA_A
  name = G4_DNA_A
  specific = 4
FEATURE [App::DocumentObjectGroupPython] H_element135  label="H_element : 082"  # scripted group (container) (typed FeaturePython)
  n = 10
  ref = H_element
FEATURE [App::DocumentObjectGroupPython] C_element145  label="C_element : 090"  # scripted group (container) (typed FeaturePython)
  n = 10
  ref = C_element
FEATURE [App::DocumentObjectGroupPython] N_element065  label="N_element : 037"  # scripted group (container) (typed FeaturePython)
  n = 5
  ref = N_element
FEATURE [App::DocumentObjectGroupPython] O_element127  label="O_element : 8"  # scripted group (container) (typed FeaturePython)
  n = 8
  ref = O_element
FEATURE [App::DocumentObjectGroupPython] P_element016  label="P_element : 005"  # scripted group (container) (typed FeaturePython)
  n = 1
  ref = P_element
FEATURE [App::DocumentObjectGroupPython] G4_DNA_G  # scripted group (container) (typed FeaturePython)
  Dunit = g/cm3
  Dvalue = 1
  Group = -> [H_element135,C_element145,N_element065,O_element127,P_element016]
  conduct = 2
  density = 1
  expand = 3
  formula = G4_DNA_G
  name = G4_DNA_G
  specific = 4
FEATURE [App::DocumentObjectGroupPython] H_element136  label="H_element : 083"  # scripted group (container) (typed FeaturePython)
  n = 10
  ref = H_element
FEATURE [App::DocumentObjectGroupPython] C_element146  label="C_element : 091"  # scripted group (container) (typed FeaturePython)
  n = 9
  ref = C_element
FEATURE [App::DocumentObjectGroupPython] N_element066  label="N_element : 038"  # scripted group (container) (typed FeaturePython)
  n = 3
  ref = N_element
FEATURE [App::DocumentObjectGroupPython] O_element128  label="O_element : 080"  # scripted group (container) (typed FeaturePython)
  n = 8
  ref = O_element
FEATURE [App::DocumentObjectGroupPython] P_element017  label="P_element : 006"  # scripted group (container) (typed FeaturePython)
  n = 1
  ref = P_element
FEATURE [App::DocumentObjectGroupPython] G4_DNA_C  # scripted group (container) (typed FeaturePython)
  Dunit = g/cm3
  Dvalue = 1
  Group = -> [H_element136,C_element146,N_element066,O_element128,P_element017]
  conduct = 2
  density = 1
  expand = 3
  formula = G4_DNA_C
  name = G4_DNA_C
  specific = 4
FEATURE [App::DocumentObjectGroupPython] H_element137  label="H_element : 084"  # scripted group (container) (typed FeaturePython)
  n = 9
  ref = H_element
FEATURE [App::DocumentObjectGroupPython] C_element147  label="C_element : 092"  # scripted group (container) (typed FeaturePython)
  n = 9
  ref = C_element
FEATURE [App::DocumentObjectGroupPython] N_element067  label="N_element : 039"  # scripted group (container) (typed FeaturePython)
  n = 2
  ref = N_element
FEATURE [App::DocumentObjectGroupPython] O_element129  label="O_element : 9"  # scripted group (container) (typed FeaturePython)
  n = 9
  ref = O_element
FEATURE [App::DocumentObjectGroupPython] P_element018  label="P_element : 007"  # scripted group (container) (typed FeaturePython)
  n = 1
  ref = P_element
FEATURE [App::DocumentObjectGroupPython] G4_DNA_U  # scripted group (container) (typed FeaturePython)
  Dunit = g/cm3
  Dvalue = 1
  Group = -> [H_element137,C_element147,N_element067,O_element129,P_element018]
  conduct = 2
  density = 1
  expand = 3
  formula = G4_DNA_U
  name = G4_DNA_U
  specific = 4
FEATURE [App::DocumentObjectGroupPython] H_element138  label="H_element : 085"  # scripted group (container) (typed FeaturePython)
  n = 11
  ref = H_element
FEATURE [App::DocumentObjectGroupPython] C_element148  label="C_element : 093"  # scripted group (container) (typed FeaturePython)
  n = 10
  ref = C_element
FEATURE [App::DocumentObjectGroupPython] N_element068  label="N_element : 040"  # scripted group (container) (typed FeaturePython)
  n = 2
  ref = N_element
FEATURE [App::DocumentObjectGroupPython] O_element130  label="O_element : 081"  # scripted group (container) (typed FeaturePython)
  n = 9
  ref = O_element
FEATURE [App::DocumentObjectGroupPython] P_element019  label="P_element : 008"  # scripted group (container) (typed FeaturePython)
  n = 1
  ref = P_element
FEATURE [App::DocumentObjectGroupPython] G4_DNA_MU  # scripted group (container) (typed FeaturePython)
  Dunit = g/cm3
  Dvalue = 1
  Group = -> [H_element138,C_element148,N_element068,O_element130,P_element019]
  conduct = 2
  density = 1
  expand = 3
  formula = G4_DNA_MU
  name = G4_DNA_MU
  specific = 4
FEATURE [App::DocumentObjectGroupPython] BioChemical  # scripted group (container) (typed FeaturePython)
  Group = -> [G4_CYTOSINE,G4_THYMINE,G4_URACIL,G4_DNA_ADENINE,G4_DNA_GUANINE,G4_DNA_CYTOSINE,G4_DNA_THYMINE,G4_DNA_URACIL,G4_DNA_ADENOSINE,G4_DNA_GUANOSINE,G4_DNA_CYTIDINE,G4_DNA_URIDINE,G4_DNA_METHYLURIDINE,G4_DNA_MONOPHOSPHATE,G4_DNA_A,G4_DNA_G,G4_DNA_C,G4_DNA_U,G4_DNA_MU]
FEATURE [App::DocumentObjectGroupPython] G4Materials  # scripted group (container) (typed FeaturePython)
  Group = -> [NIST,Element,HEP,Space,BioChemical]
  version = 1
FEATURE [App::DocumentObjectGroupPython] Geant4  # scripted group (container) (typed FeaturePython)
  Group = -> [G4Isotopes,G4Elements,G4Materials]
FEATURE [App::DocumentObjectGroupPython] Materials  # scripted group (container) (typed FeaturePython)
  Group = -> [Geant4]
FEATURE [Part::FeaturePython] GDMLBox_WorldBox  # WARN: FeaturePython — macro-defined, semantics opaque (R4)
  lunit = 3
  material = 288
  x = 500
  y = 500
  z = 1200
FEATURE [Sketcher::SketchObject] Sketch001
  FullyConstrained = false
  MapMode = 5
  Placement = pos=(0,0,0) rot=(0.57735,0.57735,0.57735;2.0944rad)
  Support = -> [YZ_Plane001]
  sketch-geometry (36):
    g0: LineSegment StartX=345.196 StartY=1207.39 StartZ=0 EndX=345.196 EndY=4779.1 EndZ=0
    g1: LineSegment StartX=910.487 StartY=4896.42 StartZ=0 EndX=910.487 EndY=5006.42 EndZ=0
    g2: LineSegment StartX=435.196 StartY=4869.1 StartZ=0 EndX=445.196 EndY=4869.1 EndZ=0
    g3: LineSegment StartX=445.196 StartY=4869.1 StartZ=0 EndX=445.196 EndY=4896.42 EndZ=0
    g4: LineSegment StartX=445.196 StartY=4896.42 StartZ=0 EndX=910.487 EndY=4896.42 EndZ=0
    g5: LineSegment StartX=318.538 StartY=5006.42 StartZ=0 EndX=910.487 EndY=5006.42 EndZ=0
    g6: LineSegment StartX=175.531 StartY=1234.96 StartZ=0 EndX=318.538 EndY=1234.96 EndZ=0
    g7: LineSegment StartX=318.538 StartY=5006.42 StartZ=0 EndX=318.538 EndY=1234.96 EndZ=0
    g8: LineSegment StartX=0 StartY=39.215 StartZ=0 EndX=0 EndY=0 EndZ=0
    g9-g16: Circle x8 (B-spline internal-alignment scaffolding for g17; pole/knot coordinates omitted)
    g17: BSplineCurve PolesCount=8 KnotsCount=6 Degree=3 IsPeriodic=0
    g18-g23: GeomPoint x6 (B-spline internal-alignment scaffolding for g17; pole/knot coordinates omitted)
    g24: LineSegment StartX=175.531 StartY=1234.96 StartZ=0 EndX=175.531 EndY=838.896 EndZ=0
    g25-g29: Circle x5 (B-spline internal-alignment scaffolding for g30; pole/knot coordinates omitted)
    g30: BSplineCurve PolesCount=5 KnotsCount=3 Degree=3 IsPeriodic=0
    g31: GeomPoint X=175.531 Y=838.896 Z=0
    g32: GeomPoint X=165.058 Y=242.363 Z=0
    g33: GeomPoint X=0 Y=39.215 Z=0
    g34: ArcOfCircle CenterX=435.196 CenterY=4779.1 CenterZ=0 NormalX=0 NormalY=0 NormalZ=1 AngleXU=0 Radius=90 StartAngle=1.5708 EndAngle=3.14159
    g35: GeomPoint X=345.196 Y=4869.1 Z=0
  constraints (38):
    c: Vertical(g1)
    c: Horizontal(g2)
    c: Coincident(g2,g3)
    c: Vertical(g3)
    c: Coincident(g3,g4)
    c: Coincident(g4,g1)
    c: Horizontal(g4)
    c: Coincident(g5,g1)
    c: Horizontal(g5)
    c: Horizontal(g6)
    c: Coincident(g7,g5)
    c: Coincident(g7,g6)
    c: Vertical(g7)
    c: DistanceX(g35,g2) = 100
    c: Vertical(g8)
    c: Vertical(g0)
    c: Coincident(g17,g0)
    c: Weight(g9) = 1
    c: Equal(g9, g10-g16) x7
    c: Coincident(g17,g8)
    c: InternalAlignment(g9-g16 -> g17) x8
    c: InternalAlignment(g18-g23 -> g17) x6
    c: Coincident(g24,g6)
    c: Vertical(g24)
    c: Coincident(g30,g24)
    c: Weight(g25) = 1
    c: Equal(g25, g26-g29) x4
    c: Coincident(g30,g8)
    c: InternalAlignment(g25-g29 -> g30) x5
    c: InternalAlignment(g31,g30)
    c: InternalAlignment(g32,g30)
    c: InternalAlignment(g33,g30)
    c: Coincident(g8,g-1)
    c: PointOnObject(g35,g2)
    c: PointOnObject(g35,g0)
    c: Tangent(g2,g34) = 1.5708
    c: Tangent(g0,g34) = 1.5708
    c: Radius(g34) = 90
FEATURE [Part::Revolution] Revolve
  Angle = 360
  Axis = (0,0,1)
  Base = (0,0,0)
  FaceMakerClass = Part::FaceMakerBullseye
  Solid = true
  Source = -> Sketch001
  Symmetric = false
  material = 176
FEATURE [Part::Cylinder] Cylinder
  Angle = 360
  AttacherType = Attacher::AttachEngine3D
  FirstAngle = 0
  Height = 200
  Placement = pos=(474,0,4850) rot=(0,0,1;0rad)
  Radius = 60
  SecondAngle = 0
FEATURE [Part::Mirroring] Part__Mirroring  label="Cylinder (Mirror #1)"
  Base = (0,0,0)
  Normal = (1,0,0)
  Source = -> Cylinder
FEATURE [Part::FeaturePython] Array  # Draft array (typed FeaturePython)
  Angle = 360
  ArrayType = 1
  Axis = (0,0,1)
  Base = -> Cylinder
  Center = (0,0,0)
  Count = 6
  Fuse = false
  IntervalAxis = (0,0,0)
  IntervalX = (50,0,0)
  IntervalY = (0,50,0)
  IntervalZ = (0,0,50)
  NumberCircles = 3
  NumberPolar = 6
  NumberX = 2
  NumberY = 2
  NumberZ = 1
  RadialDistance = 50
  Symmetry = 1
  TangentialDistance = 25
FEATURE [Part::Cut] Cut
  Base = -> Revolve
  Tool = -> Array
FEATURE [App::Part] Bool_Cut
  Group = -> [Sketch001,Revolve,Cylinder,Cut]
  Origin = -> Origin004
FEATURE [App::Part] worldVOL
  Group = -> [GDMLBox_WorldBox,Bool_Cut]
  Origin = -> Origin
